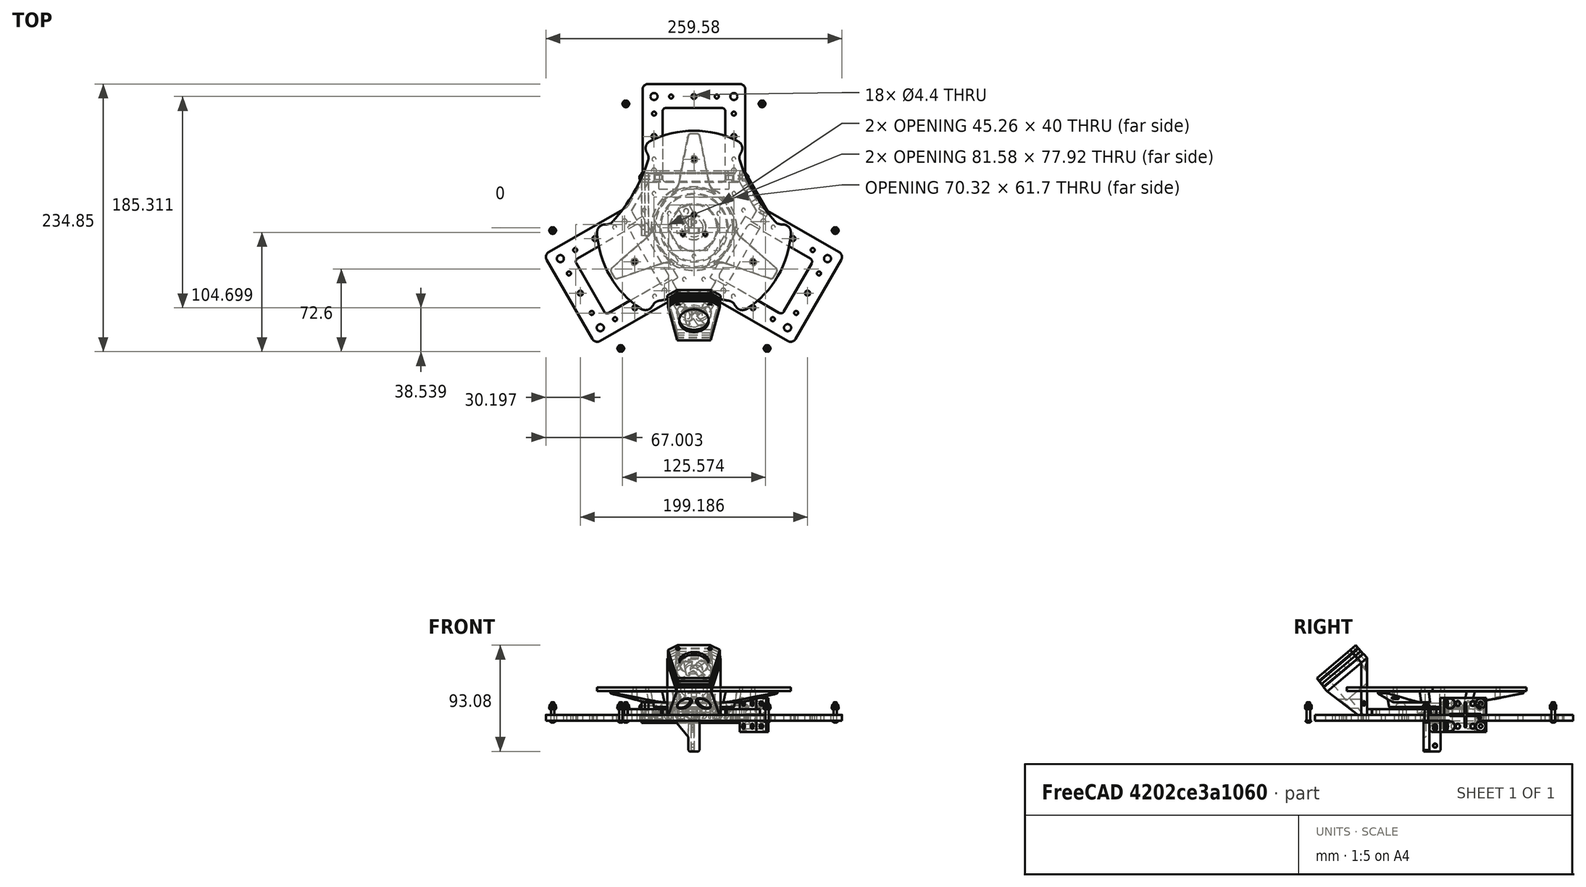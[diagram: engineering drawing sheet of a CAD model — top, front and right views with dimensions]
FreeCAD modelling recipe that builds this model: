
FCSTD DOCUMENT  (FreeCAD 2023.131R26244 +5365 (Git))
Label: structures
License: Creative Commons Attribution-NoDerivatives
LicenseURL: http://creativecommons.org/licenses/by-nd/4.0/
objects: Sketcher::SketchObject×48, PartDesign::Pad×27, PartDesign::Pocket×26, PartDesign::Chamfer×25, PartDesign::Fillet×20, PartDesign::Body×19, Part::FeaturePython×16, App::Link×15, TechDraw::DrawProjGroupItem×12, TechDraw::DrawProjGroup×12, App::Part×11, TechDraw::DrawSVGTemplate×9, TechDraw::DrawPage×9, PartDesign::Mirrored×7, PartDesign::SubShapeBinder×7, PartDesign::PolarPattern×6, App::DocumentObjectGroup×6, TechDraw::DrawViewDimension×5, Part::Mirroring×2, PartDesign::Draft×2, +8 more types
note: 505 computed .brp shape members not serialized (recipe doc carries the construction recipe); baked Part::Feature solids carry a one-line shape summary decoded from their .brp
EXTERNAL_REF file=generic-hardware.FCStd obj=Part035
EXTERNAL_REF file=generic-hardware.FCStd obj=Part036

FEATURE [Sketcher::SketchObject] Sketch032
  ArcFitTolerance = 0
  AttachmentSupport = -> [XY_Plane026]
  ExternalBSplineMaxDegree = 0
  ExternalBSplineTolerance = 0
  FullyConstrained = true
  InternalTolerance = 1e-06
  InvalidShape = false
  MakeInternals = false
  MapMode = 5
  Support = -> [XY_Plane026]
  TreeRank = 0
  ValidateShape = true
  sketch-geometry (56):
    g0: LineSegment StartX=-131.619 StartY=-24.0289 StartZ=0 EndX=-58.007 EndY=18.4711 EndZ=0
    g1: LineSegment StartX=-58.007 StartY=18.4711 StartZ=0 EndX=-45 EndY=41 EndZ=0
    g2: LineSegment StartX=-45 StartY=41 StartZ=0 EndX=-45 EndY=126 EndZ=0
    g3: LineSegment StartX=-45 StartY=126 StartZ=0 EndX=45 EndY=126 EndZ=0
    g4: LineSegment StartX=45 StartY=126 StartZ=0 EndX=45 EndY=41 EndZ=0
    g5: LineSegment StartX=45 StartY=41 StartZ=0 EndX=58.007 EndY=18.4711 EndZ=0
    g6: LineSegment StartX=58.007 StartY=18.4711 StartZ=0 EndX=131.619 EndY=-24.0289 EndZ=0
    g7: LineSegment StartX=131.619 StartY=-24.0289 StartZ=0 EndX=86.6192 EndY=-101.971 EndZ=0
    g8: LineSegment StartX=86.6192 StartY=-101.971 StartZ=0 EndX=13.007 EndY=-59.4711 EndZ=0
    g9: LineSegment StartX=13.007 StartY=-59.4711 StartZ=0 EndX=-13.007 EndY=-59.4711 EndZ=0
    g10: LineSegment StartX=-13.007 StartY=-59.4711 StartZ=0 EndX=-86.6192 EndY=-101.971 EndZ=0
    g11: LineSegment StartX=-86.6192 StartY=-101.971 StartZ=0 EndX=-131.619 EndY=-24.0289 EndZ=0
    g12: LineSegment [constr] StartX=-1e-16 StartY=1e-16 StartZ=0 EndX=-1e-16 EndY=126 EndZ=0
    g13: LineSegment [constr] StartX=-1e-16 StartY=1e-16 StartZ=0 EndX=-109.119 EndY=-63 EndZ=0
    g14: LineSegment [constr] StartX=-1e-16 StartY=1e-16 StartZ=0 EndX=109.119 EndY=-63 EndZ=0
    g15: LineSegment StartX=-27.5 StartY=40 StartZ=0 EndX=27.5 EndY=40 EndZ=0
    g16: LineSegment StartX=27.5 StartY=40 StartZ=0 EndX=27.5 EndY=105 EndZ=0
    g17: LineSegment StartX=27.5 StartY=105 StartZ=0 EndX=-27.5 EndY=105 EndZ=0
    g18: LineSegment StartX=-27.5 StartY=105 StartZ=0 EndX=-27.5 EndY=40 EndZ=0
    g19: LineSegment StartX=20.891 StartY=-43.8157 StartZ=0 EndX=48.391 EndY=3.8157 EndZ=0
    g20: LineSegment StartX=48.391 StartY=3.8157 StartZ=0 EndX=104.683 EndY=-28.6843 EndZ=0
    g21: LineSegment StartX=104.683 StartY=-28.6843 StartZ=0 EndX=77.1827 EndY=-76.3157 EndZ=0
    g22: LineSegment StartX=77.1827 StartY=-76.3157 StartZ=0 EndX=20.891 EndY=-43.8157 EndZ=0
    g23: LineSegment StartX=-104.683 StartY=-28.6843 StartZ=0 EndX=-77.1827 EndY=-76.3157 EndZ=0
    g24: LineSegment StartX=-77.1827 StartY=-76.3157 StartZ=0 EndX=-20.891 EndY=-43.8157 EndZ=0
    g25: LineSegment StartX=-20.891 StartY=-43.8157 StartZ=0 EndX=-48.391 EndY=3.8157 EndZ=0
    g26: LineSegment StartX=-48.391 StartY=3.8157 StartZ=0 EndX=-104.683 EndY=-28.6843 EndZ=0
    g27: Circle [constr] CenterX=-1e-16 CenterY=1e-16 CenterZ=0 NormalX=0 NormalY=0 NormalZ=1 AngleXU=0 Radius=48.5412
    g28: LineSegment StartX=-11.547 StartY=-20 StartZ=0 EndX=-23.094 EndY=0 EndZ=0
    g29: LineSegment StartX=-23.094 StartY=-1.3e-15 StartZ=0 EndX=-11.547 EndY=20 EndZ=0
    g30: LineSegment StartX=-11.547 StartY=20 StartZ=0 EndX=11.547 EndY=20 EndZ=0
    g31: LineSegment StartX=11.547 StartY=20 StartZ=0 EndX=23.094 EndY=0 EndZ=0
    g32: LineSegment StartX=23.094 StartY=9e-16 StartZ=0 EndX=11.547 EndY=-20 EndZ=0
    g33: LineSegment StartX=11.547 StartY=-20 StartZ=0 EndX=-11.547 EndY=-20 EndZ=0
    g34: Circle [constr] CenterX=-1e-16 CenterY=1e-16 CenterZ=0 NormalX=0 NormalY=0 NormalZ=1 AngleXU=0 Radius=23.094
    g35: Circle CenterX=-21.6506 CenterY=12.5 CenterZ=0 NormalX=0 NormalY=0 NormalZ=1 AngleXU=0 Radius=1.6
    g36: Circle CenterX=21.6506 CenterY=12.5 CenterZ=0 NormalX=0 NormalY=0 NormalZ=1 AngleXU=0 Radius=1.6
    g37: Circle CenterX=0 CenterY=-25 CenterZ=0 NormalX=0 NormalY=0 NormalZ=1 AngleXU=0 Radius=1.6
    g38: LineSegment [constr] StartX=0 StartY=-25 StartZ=0 EndX=-1e-16 EndY=0 EndZ=0
    g39: LineSegment [constr] StartX=-1e-16 StartY=1e-16 StartZ=0 EndX=21.6506 EndY=12.5 EndZ=0
    g40: LineSegment [constr] StartX=-1e-16 StartY=1e-16 StartZ=0 EndX=-21.6506 EndY=12.5 EndZ=0
    g41: LineSegment [constr] StartX=-45 StartY=126 StartZ=0 EndX=-131.619 EndY=-24.0289 EndZ=0
    g42: LineSegment [constr] StartX=-86.6192 StartY=-101.971 StartZ=0 EndX=86.6192 EndY=-101.971 EndZ=0
    g43: LineSegment [constr] StartX=131.619 StartY=-24.0289 StartZ=0 EndX=45 EndY=126 EndZ=0
    g44: LineSegment [constr] StartX=-45 StartY=126 StartZ=0 EndX=-55 EndY=108.679 EndZ=0
    g45: LineSegment [constr] StartX=-55 StartY=108.679 StartZ=0 EndX=-45 EndY=41 EndZ=0
    g46: LineSegment [constr] StartX=-58.007 StartY=18.4711 StartZ=0 EndX=-121.619 EndY=-6.70835 EndZ=0
    g47: LineSegment [constr] StartX=-121.619 StartY=-6.70835 StartZ=0 EndX=-131.619 EndY=-24.0289 EndZ=0
    g48: LineSegment [constr] StartX=-86.6192 StartY=-101.971 StartZ=0 EndX=-66.6192 EndY=-101.971 EndZ=0
    g49: LineSegment [constr] StartX=-66.6192 StartY=-101.971 StartZ=0 EndX=-13.007 EndY=-59.4711 EndZ=0
    g50: LineSegment [constr] StartX=13.007 StartY=-59.4711 StartZ=0 EndX=66.6192 EndY=-101.971 EndZ=0
    g51: LineSegment [constr] StartX=66.6192 StartY=-101.971 StartZ=0 EndX=86.6192 EndY=-101.971 EndZ=0
    g52: LineSegment [constr] StartX=131.619 StartY=-24.0289 StartZ=0 EndX=121.619 EndY=-6.70835 EndZ=0
    g53: LineSegment [constr] StartX=121.619 StartY=-6.70835 StartZ=0 EndX=58.007 EndY=18.4711 EndZ=0
    g54: LineSegment [constr] StartX=45 StartY=41 StartZ=0 EndX=55 EndY=108.679 EndZ=0
    g55: LineSegment [constr] StartX=55 StartY=108.679 StartZ=0 EndX=45 EndY=126 EndZ=0
  constraints (151):
    c: Coincident(g0,g1)
    c: Coincident(g1,g2)
    c: Vertical(g2)
    c: Coincident(g2,g3)
    c: Horizontal(g3)
    c: Coincident(g3,g4)
    c: Vertical(g4)
    c: Coincident(g4,g5)
    c: Coincident(g5,g6)
    c: Coincident(g6,g7)
    c: Coincident(g7,g8)
    c: Coincident(g8,g9)
    c: Horizontal(g9)
    c: Coincident(g9,g10)
    c: Coincident(g10,g11)
    c: Coincident(g11,g0)
    c: Parallel(g8,g6)
    c: Parallel(g10,g0)
    c: Equal(g4,g6)
    c: Equal(g6,g8)
    c: Equal(g8,g10)
    c: Equal(g10,g0)
    c: Equal(g0,g2)
    c: Perpendicular(g6,g7)
    c: Perpendicular(g11,g10)
    c: Coincident(g12,g-1)
    c: PointOnObject(g12,g3)
    c: Vertical(g12)
    c: Coincident(g13,g12)
    c: Coincident(g14,g12)
    c: Symmetric(g6,g7,g14)
    c: Symmetric(g10,g0,g13)
    c: Perpendicular(g13,g11)
    c: Perpendicular(g7,g14)
    c: DistanceX(g3,g3) = 90
    c: Equal(g9,g5)
    c: Equal(g5,g1)
    c: Angle(g14,g12) = 2.0944
    c: Angle(g12,g13) = 2.0944
    c: DistanceY(g12,g2) = 126
    c: DistanceX(g9,g9) = 26.0141
    c: Coincident(g15,g16)
    c: Coincident(g16,g17)
    c: Coincident(g17,g18)
    c: Coincident(g18,g15)
    c: Horizontal(g15)
    c: Vertical(g16)
    c: Vertical(g18)
    c: Symmetric(g16,g17,g12)
    c: DistanceX(g17,g17) = 55
    c: DistanceY(g16,g16) = 65
    c: Coincident(g19,g20)
    c: Coincident(g20,g21)
    c: Coincident(g21,g22)
    c: Coincident(g22,g19)
    c: Coincident(g23,g24)
    c: Coincident(g24,g25)
    c: Coincident(g25,g26)
    c: Coincident(g26,g23)
    c: Equal(g25,g23)
    c: Equal(g23,g19)
    c: Equal(g19,g21)
    c: Equal(g21,g15)
    c: Equal(g22,g20)
    c: Equal(g20,g16)
    c: Equal(g16,g26)
    c: Equal(g26,g24)
    c: Parallel(g24,g13)
    c: Parallel(g22,g14)
    c: Symmetric(g23,g23,g13)
    c: Symmetric(g21,g20,g14)
    c: Coincident(g27,g12)
    c: PointOnObject(g19,g27)
    c: PointOnObject(g24,g27)
    c: PointOnObject(g15,g27)
    c: Equal(g11,g7)
    c: Equal(g7,g3)
    c: Coincident(g28,g29)
    c: Coincident(g29,g30)
    c: Coincident(g30,g31)
    c: Coincident(g31,g32)
    c: Coincident(g32,g33)
    c: Coincident(g33,g28)
    c: Horizontal(g33)
    c: Horizontal(g30)
    c: Equal(g29,g30)
    c: Equal(g30,g31)
    c: Equal(g31,g32)
    c: Equal(g32,g33)
    c: Equal(g33,g28)
    c: Coincident(g34,g12)
    c: PointOnObject(g30,g34)
    c: PointOnObject(g31,g34)
    c: PointOnObject(g32,g34)
    c: PointOnObject(g28,g34)
    c: PointOnObject(g28,g34)
    c: DistanceY(g12,g30) = 20
    c: PointOnObject(g37,g-2)
    c: Equal(g37,g36)
    c: Equal(g36,g35)
    c: Diameter(g35) = 3.2
    c: Coincident(g38,g37)
    c: Coincident(g38,g12)
    c: Coincident(g39,g12)
    c: Coincident(g39,g36)
    c: Coincident(g40,g12)
    c: Coincident(g40,g35)
    c: Perpendicular(g29,g40)
    c: Perpendicular(g31,g39)
    c: Equal(g40,g38)
    c: Equal(g38,g39)
    c: DistanceY(g38,g38) = 25
    c: Coincident(g41,g3)
    c: Coincident(g41,g11)
    c: Coincident(g42,g11)
    c: Coincident(g42,g7)
    c: Coincident(g43,g7)
    c: Coincident(g43,g3)
    c: Coincident(g3,g44)
    c: PointOnObject(g44,g41)
    c: Coincident(g44,g45)
    c: Coincident(g45,g1)
    c: Coincident(g1,g46)
    c: PointOnObject(g46,g41)
    c: Coincident(g46,g47)
    c: Coincident(g47,g11)
    c: Coincident(g11,g48)
    c: Horizontal(g48)
    c: Coincident(g48,g49)
    c: Coincident(g49,g9)
    c: Coincident(g9,g50)
    c: PointOnObject(g50,g42)
    c: Coincident(g50,g51)
    c: Coincident(g51,g7)
    c: Coincident(g7,g52)
    c: PointOnObject(g52,g43)
    c: Coincident(g52,g53)
    c: Coincident(g53,g5)
    c: Coincident(g5,g54)
    c: PointOnObject(g54,g43)
    c: Coincident(g54,g55)
    c: Coincident(g55,g3)
    c: Equal(g55,g44)
    c: Equal(g44,g47)
    c: Equal(g47,g48)
    c: Equal(g48,g51)
    c: Equal(g55,g52)
    c: DistanceX(g48,g48) = 20
    c: DistanceY(g16) = 105
    c: DistanceY(g50,g12) = 101.971
    c: DistanceY(g4,g4) = 85
FEATURE [PartDesign::Pad] Pad020
  AddSubType = 0
  AutoTaperInnerAngle = false
  CheckUpToFaceLimits = true
  ClaimChildren = false
  Direction = (0,0,1)
  Fit = 0
  FitJoin = 0
  InnerFit = 0
  InnerFitJoin = 0
  InvalidShape = false
  Length = 5
  Length2 = 100
  Linearize = true
  NewSolid = false
  Profile = -> Sketch032
  Refine = true
  Reversed = true
  Suppress = false
  TaperInnerAngle = 0
  TaperInnerAngleRev = 0
  TreeRank = 0
  Type = 0
  ValidateShape = true
  _ProfileBasedVersion = 1
FEATURE [PartDesign::Fillet] Fillet008
  AddSubType = 0
  Base = -> Pad020 [Edge41,Edge44,Edge37,Edge38,Edge65,Edge62,Edge61,Edge68,Edge49,Edge50,Edge53,Edge56]
  BaseFeature = -> Pad020
  InvalidShape = false
  NewSolid = false
  Radius = 3
  Refine = true
  SupportTransform = false
  Suppress = false
  TreeRank = 0
  ValidateShape = true
FEATURE [PartDesign::Fillet] Fillet009
  AddSubType = 0
  Base = -> Fillet008 [Edge110,Edge99,Edge107,Edge106,Edge102,Edge103]
  BaseFeature = -> Fillet008
  InvalidShape = false
  NewSolid = false
  Radius = 5
  Refine = true
  SupportTransform = false
  Suppress = false
  TreeRank = 0
  ValidateShape = true
FEATURE [PartDesign::Fillet] Fillet010
  AddSubType = 0
  Base = -> Fillet009 [Edge53,Edge57,Edge67,Edge71,Edge77,Edge81]
  BaseFeature = -> Fillet009
  InvalidShape = false
  NewSolid = false
  Radius = 5
  Refine = true
  SupportTransform = false
  Suppress = false
  TreeRank = 0
  ValidateShape = true
FEATURE [Sketcher::SketchObject] Sketch033
  ArcFitTolerance = 0
  AttachmentSupport = -> [XY_Plane026]
  ExternalBSplineMaxDegree = 0
  ExternalBSplineTolerance = 0
  FullyConstrained = true
  InternalTolerance = 1e-06
  InvalidShape = false
  MakeInternals = false
  MapMode = 5
  Support = -> [XY_Plane026]
  TreeRank = 0
  ValidateShape = true
  sketch-geometry (13):
    g0: Circle CenterX=-20 CenterY=115 CenterZ=0 NormalX=0 NormalY=0 NormalZ=1 AngleXU=0 Radius=1.75
    g1: Circle CenterX=20 CenterY=115 CenterZ=0 NormalX=0 NormalY=0 NormalZ=1 AngleXU=0 Radius=1.75
    g2: Circle CenterX=-35 CenterY=60 CenterZ=0 NormalX=0 NormalY=0 NormalZ=1 AngleXU=0 Radius=1.75
    g3: Circle CenterX=-35 CenterY=100 CenterZ=0 NormalX=0 NormalY=0 NormalZ=1 AngleXU=0 Radius=1.75
    g4: Circle CenterX=35 CenterY=100 CenterZ=0 NormalX=0 NormalY=0 NormalZ=1 AngleXU=0 Radius=1.75
    g5: Circle CenterX=35 CenterY=60 CenterZ=0 NormalX=0 NormalY=0 NormalZ=1 AngleXU=0 Radius=1.75
    g6: Circle CenterX=-35 CenterY=115 CenterZ=0 NormalX=0 NormalY=0 NormalZ=1 AngleXU=0 Radius=3.1
    g7: Circle CenterX=35 CenterY=115 CenterZ=0 NormalX=0 NormalY=0 NormalZ=1 AngleXU=0 Radius=3.1
    g8: Circle CenterX=-35 CenterY=80 CenterZ=0 NormalX=0 NormalY=0 NormalZ=1 AngleXU=0 Radius=2.2
    g9: Circle CenterX=35 CenterY=80 CenterZ=0 NormalX=0 NormalY=0 NormalZ=1 AngleXU=0 Radius=2.2
    g10: Circle CenterX=-35 CenterY=50 CenterZ=0 NormalX=0 NormalY=0 NormalZ=1 AngleXU=0 Radius=2.2
    g11: Circle CenterX=35 CenterY=50 CenterZ=0 NormalX=0 NormalY=0 NormalZ=1 AngleXU=0 Radius=2.2
    g12: Circle CenterX=-1.0206e-12 CenterY=115 CenterZ=0 NormalX=0 NormalY=0 NormalZ=1 AngleXU=0 Radius=2.2
  constraints (31):
    c: Equal(g0,g3)
    c: Equal(g3,g2)
    c: Equal(g2,g1)
    c: Equal(g1,g4)
    c: Equal(g4,g5)
    c: Diameter(g0) = 3.5
    c: Symmetric(g1,g0,g-2)
    c: Symmetric(g3,g4,g-2)
    c: Symmetric(g2,g5,g-2)
    c: Vertical(g3,g2)
    c: DistanceX(g3,g4) = 70
    c: DistanceX(g0,g1) = 40
    c: DistanceY(g4,g1) = 15
    c: DistanceY(g5,g4) = 40
    c: DistanceY(g-1,g1) = 115
    c: Symmetric(g7,g6,g-2)
    c: Horizontal(g6,g0)
    c: Diameter(g7) = 6.2
    c: Equal(g7,g6)
    c: Vertical(g7,g4)
    c: Equal(g9,g8)
    c: Symmetric(g8,g9,g-2)
    c: Symmetric(g5,g4,g9)
    c: Diameter(g9) = 4.4
    c: Symmetric(g1,g0,g12)
    c: Equal(g12,g11)
    c: Equal(g11,g10)
    c: Equal(g10,g9)
    c: Vertical(g11,g5)
    c: Symmetric(g11,g10,g-2)
    c: DistanceY(g11,g5) = 10
FEATURE [PartDesign::Pocket] Pocket012
  AddSubType = 1
  AutoTaperInnerAngle = false
  BaseFeature = -> Fillet010
  CheckUpToFaceLimits = true
  ClaimChildren = false
  Fit = 0
  FitJoin = 0
  InnerFit = 0
  InnerFitJoin = 0
  InvalidShape = false
  Length = 5
  Length2 = 100
  Linearize = true
  NewSolid = false
  Profile = -> Sketch033
  Refine = true
  Suppress = false
  TaperInnerAngle = 0
  TaperInnerAngleRev = 0
  TreeRank = 0
  Type = 1
  ValidateShape = true
  _ProfileBasedVersion = 1
  _Version = 0
FEATURE [PartDesign::PolarPattern] PolarPattern013
  AddSubType = 0
  Angle = 360
  Axis = -> Sketch033 [N_Axis]
  BaseFeature = -> Pocket012
  CopyShape = false
  InvalidShape = false
  NewSolid = false
  Occurrences = 3
  OriginalSubs = -> [Pocket012]
  Originals = -> [Pocket012]
  ParallelTransform = true
  Refine = true
  SubTransform = true
  Suppress = false
  TreeRank = 0
  ValidateShape = true
  _Version = 0
FEATURE [PartDesign::Fillet] Fillet011
  AddSubType = 0
  Base = -> PolarPattern013 [Edge190,Edge189,Edge192,Edge196,Edge198,Edge194]
  BaseFeature = -> PolarPattern013
  InvalidShape = false
  NewSolid = false
  Radius = 3
  Refine = true
  SupportTransform = false
  Suppress = false
  TreeRank = 0
  ValidateShape = true
FEATURE [PartDesign::Body] Body019  label="Semelle"
  AutoGroupSolids = false
  ClaimAllChildren = false
  ExportMode = 0
  Group = -> [Sketch032,Pad020,Fillet008,Fillet009,Fillet010,Sketch033,Pocket012,PolarPattern013,Fillet011]
  InvalidShape = false
  Origin = -> Origin029
  SingleSolid = true
  Tip = -> Fillet011
  TreeRank = 0
  ValidateShape = true
  _ExportChildren = -> [Pad020,Fillet008,Fillet009,Fillet010,Pocket012,PolarPattern013,Fillet011]
  _GroupVersion = 1
FEATURE [Sketcher::SketchObject] Sketch034
  ArcFitTolerance = 0
  AttachmentSupport = -> [XY_Plane027]
  ExternalBSplineMaxDegree = 0
  ExternalBSplineTolerance = 0
  FullyConstrained = true
  InternalTolerance = 1e-06
  InvalidShape = false
  MakeInternals = false
  MapMode = 5
  Support = -> [XY_Plane027]
  TreeRank = 0
  ValidateShape = true
  sketch-geometry (33):
    g0: LineSegment StartX=-54.641 StartY=14.641 StartZ=0 EndX=-40 EndY=40 EndZ=0
    g1: LineSegment StartX=-40 StartY=40 StartZ=0 EndX=-31 EndY=40 EndZ=0
    g2: LineSegment StartX=-31 StartY=40 StartZ=0 EndX=-31 EndY=34 EndZ=0
    g3: LineSegment StartX=-31 StartY=34 StartZ=0 EndX=31 EndY=34 EndZ=0
    g4: LineSegment StartX=31 StartY=34 StartZ=0 EndX=31 EndY=40 EndZ=0
    g5: LineSegment StartX=31 StartY=40 StartZ=0 EndX=40 EndY=40 EndZ=0
    g6: LineSegment StartX=40 StartY=40 StartZ=0 EndX=54.641 EndY=14.641 EndZ=0
    g7: LineSegment StartX=54.641 StartY=14.641 StartZ=0 EndX=50.141 EndY=6.84679 EndZ=0
    g8: LineSegment StartX=50.141 StartY=6.84679 StartZ=0 EndX=44.9449 EndY=9.84679 EndZ=0
    g9: LineSegment StartX=44.9449 StartY=9.84679 StartZ=0 EndX=13.9449 EndY=-43.8468 EndZ=0
    g10: LineSegment StartX=13.9449 StartY=-43.8468 StartZ=0 EndX=19.141 EndY=-46.8468 EndZ=0
    g11: LineSegment StartX=19.141 StartY=-46.8468 StartZ=0 EndX=14.641 EndY=-54.641 EndZ=0
    g12: LineSegment StartX=14.641 StartY=-54.641 StartZ=0 EndX=-14.641 EndY=-54.641 EndZ=0
    g13: LineSegment StartX=-14.641 StartY=-54.641 StartZ=0 EndX=-19.141 EndY=-46.8468 EndZ=0
    g14: LineSegment StartX=-19.141 StartY=-46.8468 StartZ=0 EndX=-13.9449 EndY=-43.8468 EndZ=0
    g15: LineSegment StartX=-13.9449 StartY=-43.8468 StartZ=0 EndX=-44.9449 EndY=9.84679 EndZ=0
    g16: LineSegment StartX=-44.9449 StartY=9.84679 StartZ=0 EndX=-50.141 EndY=6.84679 EndZ=0
    g17: LineSegment StartX=-50.141 StartY=6.84679 StartZ=0 EndX=-54.641 EndY=14.641 EndZ=0
    g18: Circle [constr] CenterX=0 CenterY=0 CenterZ=0 NormalX=0 NormalY=0 NormalZ=1 AngleXU=0 Radius=56.5685
    g19: Circle [constr] CenterX=0 CenterY=0 CenterZ=0 NormalX=0 NormalY=0 NormalZ=1 AngleXU=0 Radius=25
    g20: Circle CenterX=-21.6506 CenterY=12.5 CenterZ=0 NormalX=0 NormalY=0 NormalZ=1 AngleXU=0 Radius=1.6
    g21: Circle CenterX=21.6506 CenterY=12.5 CenterZ=0 NormalX=0 NormalY=0 NormalZ=1 AngleXU=0 Radius=1.6
    g22: Circle CenterX=0 CenterY=-25 CenterZ=0 NormalX=0 NormalY=0 NormalZ=1 AngleXU=0 Radius=1.6
    g23: LineSegment [constr] StartX=0 StartY=0 StartZ=0 EndX=21.6506 EndY=12.5 EndZ=0
    g24: LineSegment [constr] StartX=0 StartY=0 StartZ=0 EndX=0 EndY=-25 EndZ=0
    g25: LineSegment [constr] StartX=0 StartY=0 StartZ=0 EndX=-21.6506 EndY=12.5 EndZ=0
    g26: LineSegment StartX=11.547 StartY=20 StartZ=0 EndX=-11.547 EndY=20 EndZ=0
    g27: LineSegment StartX=-11.547 StartY=20 StartZ=0 EndX=-23.094 EndY=1.0409e-12 EndZ=0
    g28: LineSegment StartX=-23.094 StartY=1.0409e-12 StartZ=0 EndX=-11.547 EndY=-20 EndZ=0
    g29: LineSegment StartX=-11.547 StartY=-20 StartZ=0 EndX=11.547 EndY=-20 EndZ=0
    g30: LineSegment StartX=11.547 StartY=-20 StartZ=0 EndX=23.094 EndY=1.0374e-12 EndZ=0
    g31: LineSegment StartX=23.094 StartY=1.0374e-12 StartZ=0 EndX=11.547 EndY=20 EndZ=0
    g32: Circle [constr] CenterX=0 CenterY=0 CenterZ=0 NormalX=0 NormalY=0 NormalZ=1 AngleXU=0 Radius=23.094
  constraints (88):
    c: Coincident(g0,g1)
    c: Horizontal(g1)
    c: Coincident(g1,g2)
    c: Vertical(g2)
    c: Coincident(g2,g3)
    c: Coincident(g3,g4)
    c: Vertical(g4)
    c: Coincident(g4,g5)
    c: Horizontal(g5)
    c: Coincident(g5,g6)
    c: Coincident(g6,g7)
    c: Coincident(g7,g8)
    c: Coincident(g8,g9)
    c: Coincident(g9,g10)
    c: Coincident(g10,g11)
    c: Coincident(g11,g12)
    c: Horizontal(g12)
    c: Coincident(g12,g13)
    c: Coincident(g13,g14)
    c: Coincident(g14,g15)
    c: Coincident(g15,g16)
    c: Coincident(g16,g17)
    c: Coincident(g17,g0)
    c: DistanceY(g-1,g1) = 40
    c: DistanceX(g1,g1) = 9
    c: Equal(g5,g1)
    c: Equal(g1,g17)
    c: Equal(g17,g13)
    c: Equal(g13,g11)
    c: Equal(g11,g7)
    c: Perpendicular(g10,g11)
    c: Perpendicular(g14,g13)
    c: Perpendicular(g15,g14)
    c: Perpendicular(g9,g10)
    c: Perpendicular(g9,g8)
    c: Perpendicular(g8,g7)
    c: Perpendicular(g17,g16)
    c: Perpendicular(g15,g16)
    c: DistanceY(g2,g2) = 6
    c: Equal(g8,g4)
    c: Equal(g4,g16)
    c: Equal(g0,g6)
    c: Equal(g6,g12)
    c: Coincident(g18,g-1)
    c: PointOnObject(g5,g18)
    c: PointOnObject(g6,g18)
    c: PointOnObject(g11,g18)
    c: PointOnObject(g12,g18)
    c: PointOnObject(g0,g18)
    c: PointOnObject(g0,g18)
    c: Symmetric(g3,g2,g-2)
    c: DistanceX(g3,g3) = 62
    c: Angle(g15,g3) = 1.0472
    c: Angle(g3,g9) = 1.0472
    c: Equal(g10,g8)
    c: Coincident(g19,g18)
    c: PointOnObject(g20,g19)
    c: PointOnObject(g21,g19)
    c: PointOnObject(g22,g19)
    c: PointOnObject(g22,g-2)
    c: Coincident(g23,g18)
    c: Coincident(g23,g21)
    c: Coincident(g24,g18)
    c: Coincident(g24,g22)
    c: Coincident(g25,g18)
    c: Coincident(g25,g20)
    c: Angle(g23,g25) = 2.0944
    c: Angle(g24,g23) = 2.0944
    c: DistanceY(g24,g24) = 25
    c: Equal(g21,g22)
    c: Equal(g22,g20)
    c: Diameter(g21) = 3.2
    c: Coincident(g26,g27)
    c: Coincident(g27,g28)
    c: Coincident(g28,g29)
    c: Coincident(g29,g30)
    c: Coincident(g30,g31)
    c: Coincident(g31,g26)
    c: Equal(g26, g27-g31) x5
    c: PointOnObject(g26,g32)
    c: PointOnObject(g27,g32)
    c: PointOnObject(g28,g32)
    c: PointOnObject(g29,g32)
    c: PointOnObject(g30,g32)
    c: PointOnObject(g31,g32)
    c: Coincident(g32,g18)
    c: Horizontal(g26)
    c: DistanceY(g26) = 20
FEATURE [PartDesign::Pad] Pad021
  AddSubType = 0
  AutoTaperInnerAngle = false
  CheckUpToFaceLimits = true
  ClaimChildren = false
  Direction = (1,1,1)
  Fit = 0
  FitJoin = 0
  InnerFit = 0
  InnerFitJoin = 0
  InvalidShape = false
  Length = 5
  Length2 = 100
  Linearize = true
  NewSolid = false
  Profile = -> Sketch034
  Refine = true
  Suppress = false
  TaperInnerAngle = 0
  TaperInnerAngleRev = 0
  TreeRank = 0
  Type = 0
  ValidateShape = true
  _ProfileBasedVersion = 1
FEATURE [PartDesign::Fillet] Fillet012
  AddSubType = 0
  Base = -> Pad021 [Edge59,Edge56,Edge68,Edge55,Edge65,Edge62]
  BaseFeature = -> Pad021
  InvalidShape = false
  NewSolid = false
  Radius = 3
  Refine = true
  SupportTransform = false
  Suppress = false
  TreeRank = 0
  ValidateShape = true
FEATURE [PartDesign::Fillet] Fillet013
  AddSubType = 0
  Base = -> Fillet012 [Edge94,Edge93,Edge95,Edge96,Edge81,Edge82,Edge84,Edge83,Edge88,Edge87,Edge86,Edge85,Edge80,Edge79,Edge92,Edge91,Edge90,Edge89]
  BaseFeature = -> Fillet012
  InvalidShape = false
  NewSolid = false
  Radius = 0.5
  Refine = true
  SupportTransform = false
  Suppress = false
  TreeRank = 0
  ValidateShape = true
FEATURE [PartDesign::Body] Body020  label="CaleCentrale"
  AutoGroupSolids = false
  ClaimAllChildren = false
  ExportMode = 0
  Group = -> [Sketch034,Pad021,Fillet012,Fillet013]
  InvalidShape = false
  Origin = -> Origin030
  SingleSolid = true
  Tip = -> Fillet013
  TreeRank = 0
  ValidateShape = true
  _ExportChildren = -> [Pad021,Fillet012,Fillet013]
  _GroupVersion = 1
FEATURE [Sketcher::SketchObject] Sketch043
  ArcFitTolerance = 0
  AttachmentSupport = -> [XY_Plane031]
  ExternalBSplineMaxDegree = 0
  ExternalBSplineTolerance = 0
  FullyConstrained = true
  InternalTolerance = 1e-06
  InvalidShape = false
  MakeInternals = false
  MapMode = 5
  Support = -> [XY_Plane031]
  TreeRank = 0
  ValidateShape = true
  sketch-geometry (13):
    g0: LineSegment StartX=0 StartY=0 StartZ=0 EndX=0 EndY=-54.641 EndZ=0
    g1: LineSegment StartX=0 StartY=-54.641 StartZ=0 EndX=-14.641 EndY=-54.641 EndZ=0
    g2: LineSegment StartX=-14.641 StartY=-54.641 StartZ=0 EndX=-19.641 EndY=-45.9808 EndZ=0
    g3: LineSegment StartX=-19.641 StartY=-45.9808 StartZ=0 EndX=-28.3013 EndY=-50.9808 EndZ=0
    g4: LineSegment StartX=-28.3013 StartY=-50.9808 StartZ=0 EndX=-58.3013 EndY=0.980762 EndZ=0
    g5: LineSegment StartX=-58.3013 StartY=0.980762 StartZ=0 EndX=-49.641 EndY=5.98076 EndZ=0
    g6: LineSegment StartX=-49.641 StartY=5.98076 StartZ=0 EndX=-54.641 EndY=14.641 EndZ=0
    g7: LineSegment StartX=-54.641 StartY=14.641 StartZ=0 EndX=-47.3205 EndY=27.3205 EndZ=0
    g8: LineSegment StartX=-47.3205 StartY=27.3205 StartZ=0 EndX=0 EndY=0 EndZ=0
    g9: LineSegment [constr] StartX=-49.641 StartY=5.98076 StartZ=0 EndX=-19.641 EndY=-45.9808 EndZ=0
    g10: Circle CenterX=-43.4808 CenterY=15.3109 CenterZ=0 NormalX=0 NormalY=0 NormalZ=1 AngleXU=0 Radius=1.6
    g11: Circle CenterX=-8.48076 CenterY=-45.3109 CenterZ=0 NormalX=0 NormalY=0 NormalZ=1 AngleXU=0 Radius=1.6
    g12: LineSegment [constr] StartX=0 StartY=0 StartZ=0 EndX=-43.3013 EndY=-25 EndZ=0
  constraints (35):
    c: Coincident(g0,g-1)
    c: PointOnObject(g0,g-2)
    c: Coincident(g1,g0)
    c: Horizontal(g1)
    c: Coincident(g1,g2)
    c: Coincident(g2,g3)
    c: Coincident(g3,g4)
    c: Coincident(g4,g5)
    c: Coincident(g5,g6)
    c: Coincident(g6,g7)
    c: Coincident(g7,g8)
    c: Coincident(g8,g0)
    c: Angle(g8,g0) = 2.0944
    c: Perpendicular(g7,g8)
    c: Perpendicular(g3,g2)
    c: Perpendicular(g4,g3)
    c: Perpendicular(g4,g5)
    c: Perpendicular(g6,g5)
    c: Equal(g7,g1)
    c: Coincident(g9,g5)
    c: Tangent(g9,g2) = 1.5708
    c: Equal(g2,g3)
    c: Equal(g5,g6)
    c: Distance(g6) = 10
    c: Equal(g0,g8)
    c: Distance(g4) = 60
    c: Distance(g0,g9) = 40
    c: Coincident(g12,g0)
    c: PointOnObject(g12,g4)
    c: Perpendicular(g4,g12)
    c: Symmetric(g11,g10,g12)
    c: Diameter(g10) = 3.2
    c: Equal(g10,g11)
    c: Distance(g11,g2) = 10
    c: Distance(g11,g12) = 35
FEATURE [PartDesign::Pad] Pad027
  AddSubType = 0
  AutoTaperInnerAngle = false
  CheckUpToFaceLimits = true
  ClaimChildren = false
  Direction = (1,1,1)
  Fit = 0
  FitJoin = 0
  InnerFit = 0
  InnerFitJoin = 0
  InvalidShape = false
  Length = 5
  Length2 = 100
  Linearize = true
  NewSolid = false
  Profile = -> Sketch043
  Refine = true
  Suppress = false
  TaperInnerAngle = 0
  TaperInnerAngleRev = 0
  TreeRank = 0
  Type = 0
  ValidateShape = true
  _ProfileBasedVersion = 1
FEATURE [PartDesign::PolarPattern] PolarPattern014
  AddSubType = 0
  Angle = 360
  Axis = -> Sketch043 [N_Axis]
  BaseFeature = -> Pad027
  CopyShape = false
  InvalidShape = false
  NewSolid = false
  Occurrences = 3
  OriginalSubs = -> [Pad027]
  Originals = -> [Pad027]
  ParallelTransform = true
  Refine = true
  SubTransform = true
  Suppress = false
  TreeRank = 0
  ValidateShape = true
  _Version = 2
FEATURE [Sketcher::SketchObject] Sketch044
  ArcFitTolerance = 0
  AttachmentSupport = -> [XY_Plane031]
  ExternalBSplineMaxDegree = 0
  ExternalBSplineTolerance = 0
  FullyConstrained = true
  InternalTolerance = 1e-06
  InvalidShape = false
  MakeInternals = false
  MapMode = 5
  Support = -> [XY_Plane031]
  TreeRank = 0
  ValidateShape = true
  sketch-geometry (5):
    g0: LineSegment StartX=-35.6218 StartY=8.30127 StartZ=0 EndX=-10.6218 EndY=-35 EndZ=0
    g1: LineSegment StartX=-10.6218 StartY=-35 StartZ=0 EndX=0 EndY=-35 EndZ=0
    g2: LineSegment StartX=0 StartY=-35 StartZ=0 EndX=0 EndY=0 EndZ=0
    g3: LineSegment StartX=0 StartY=0 StartZ=0 EndX=-30.3109 EndY=17.5 EndZ=0
    g4: LineSegment StartX=-30.3109 StartY=17.5 StartZ=0 EndX=-35.6218 EndY=8.30127 EndZ=0
  constraints (14):
    c: Coincident(g0,g1)
    c: PointOnObject(g1,g-2)
    c: Horizontal(g1)
    c: Coincident(g1,g2)
    c: Coincident(g2,g-1)
    c: Coincident(g2,g3)
    c: Coincident(g3,g4)
    c: Coincident(g4,g0)
    c: Perpendicular(g4,g3)
    c: Equal(g4,g1)
    c: Equal(g2,g3)
    c: Angle(g3,g2) = 2.0944
    c: Distance(g0) = 50
    c: DistanceY(g2,g2) = 35
FEATURE [PartDesign::Pocket] Pocket017
  AddSubType = 1
  AutoTaperInnerAngle = false
  BaseFeature = -> PolarPattern014
  CheckUpToFaceLimits = true
  ClaimChildren = false
  Fit = 0
  FitJoin = 0
  InnerFit = 0
  InnerFitJoin = 0
  InvalidShape = false
  Length = 5
  Length2 = 100
  Linearize = true
  NewSolid = false
  Profile = -> Sketch044
  Refine = true
  Reversed = true
  Suppress = false
  TaperInnerAngle = 0
  TaperInnerAngleRev = 0
  TreeRank = 0
  Type = 1
  ValidateShape = true
  _ProfileBasedVersion = 1
  _Version = 0
FEATURE [PartDesign::PolarPattern] PolarPattern015
  AddSubType = 0
  Angle = 360
  Axis = -> Sketch044 [N_Axis]
  BaseFeature = -> Pocket017
  CopyShape = false
  InvalidShape = false
  NewSolid = false
  Occurrences = 3
  OriginalSubs = -> [Pocket017]
  Originals = -> [Pocket017]
  ParallelTransform = true
  Refine = true
  SubTransform = true
  Suppress = false
  TreeRank = 0
  ValidateShape = true
  _Version = 2
FEATURE [PartDesign::Chamfer] Chamfer007
  AddSubType = 0
  Angle = 45
  Base = -> PolarPattern015 [Edge8,Edge66,Edge67,Edge68,Edge77,Edge78]
  BaseFeature = -> PolarPattern015
  ChamferType = 0
  FlipDirection = false
  InvalidShape = false
  NewSolid = false
  Refine = true
  Size = 1
  Size2 = 1
  SupportTransform = false
  Suppress = false
  TreeRank = 0
  ValidateShape = true
FEATURE [PartDesign::Fillet] Fillet014
  AddSubType = 0
  Base = -> Chamfer007 [Edge101,Edge103,Edge104,Edge105,Edge106,Edge102]
  BaseFeature = -> Chamfer007
  InvalidShape = false
  NewSolid = false
  Radius = 3
  Refine = true
  SupportTransform = false
  Suppress = false
  TreeRank = 0
  ValidateShape = true
FEATURE [PartDesign::Body] Body024  label="PlaqueIntermediaire"
  AutoGroupSolids = false
  ClaimAllChildren = false
  ExportMode = 0
  Group = -> [Sketch043,Pad027,PolarPattern014,Sketch044,Pocket017,PolarPattern015,Chamfer007,Fillet014]
  InvalidShape = false
  Origin = -> Origin036
  SingleSolid = true
  Tip = -> Fillet014
  TreeRank = 0
  ValidateShape = true
  _ExportChildren = -> [Pad027,PolarPattern014,Pocket017,PolarPattern015,Chamfer007,Fillet014]
  _GroupVersion = 1
FEATURE [Sketcher::SketchObject] Sketch037
  ArcFitTolerance = 0
  AttachmentSupport = -> [XZ_Plane030]
  ExternalBSplineMaxDegree = 0
  ExternalBSplineTolerance = 0
  FullyConstrained = true
  InternalTolerance = 1e-06
  InvalidShape = false
  MakeInternals = false
  MapMode = 5
  Placement = pos=(0,0,0) rot=(1,0,0;1.5708rad)
  Support = -> [XZ_Plane030]
  TreeRank = 0
  ValidateShape = true
  sketch-geometry (6):
    g0: LineSegment StartX=-5 StartY=0 StartZ=0 EndX=15 EndY=0 EndZ=0
    g1: LineSegment StartX=15 StartY=0 StartZ=0 EndX=15 EndY=-7 EndZ=0
    g2: LineSegment StartX=15 StartY=-7 StartZ=0 EndX=5 EndY=-7 EndZ=0
    g3: LineSegment StartX=5 StartY=-7 StartZ=0 EndX=5 EndY=-32 EndZ=0
    g4: LineSegment StartX=5 StartY=-32 StartZ=0 EndX=-5 EndY=-32 EndZ=0
    g5: LineSegment StartX=-5 StartY=-32 StartZ=0 EndX=-5 EndY=0 EndZ=0
  constraints (18):
    c: PointOnObject(g0,g-1)
    c: Horizontal(g0)
    c: Coincident(g0,g1)
    c: Vertical(g1)
    c: Coincident(g1,g2)
    c: Horizontal(g2)
    c: Coincident(g2,g3)
    c: Vertical(g3)
    c: Coincident(g3,g4)
    c: Horizontal(g4)
    c: Coincident(g4,g5)
    c: Coincident(g5,g0)
    c: Vertical(g5)
    c: DistanceY(g1,g1) = 7
    c: DistanceX(g-1,g2) = 5
    c: DistanceX(g2,g2) = 10
    c: DistanceY(g3,g3) = 25
    c: DistanceX(g0,g-1) = 5
FEATURE [PartDesign::Pad] Pad024
  AddSubType = 0
  AutoTaperInnerAngle = false
  CheckUpToFaceLimits = true
  ClaimChildren = false
  Direction = (1,1,1)
  Fit = 0
  FitJoin = 0
  InnerFit = 0
  InnerFitJoin = 0
  InvalidShape = false
  Length = 10
  Length2 = 100
  Linearize = true
  NewSolid = false
  Placement = pos=(0,0,0) rot=(1,0,0;1.5708rad)
  Profile = -> Sketch037
  Refine = true
  Reversed = true
  Suppress = false
  TaperInnerAngle = 0
  TaperInnerAngleRev = 0
  TreeRank = 0
  Type = 0
  ValidateShape = true
  _ProfileBasedVersion = 1
FEATURE [PartDesign::Pad] Pad025
  AddSubType = 0
  AutoTaperInnerAngle = false
  BaseFeature = -> Pad024
  CheckUpToFaceLimits = true
  ClaimChildren = false
  Direction = (1,1,1)
  Fit = 0
  FitJoin = 0
  InnerFit = 0
  InnerFitJoin = 0
  InvalidShape = false
  Length = 5
  Length2 = 100
  Linearize = true
  NewSolid = false
  Placement = pos=(0,0,0) rot=(1,0,0;1.5708rad)
  Profile = -> Sketch037
  Refine = true
  Suppress = false
  TaperInnerAngle = 0
  TaperInnerAngleRev = 0
  TreeRank = 0
  Type = 0
  ValidateShape = true
  _ProfileBasedVersion = 1
FEATURE [Sketcher::SketchObject] Sketch038
  ArcFitTolerance = 0
  AttachmentSupport = -> [XZ_Plane030]
  ExternalBSplineMaxDegree = 0
  ExternalBSplineTolerance = 0
  ExternalGeometry = -> [Pad025]
  FullyConstrained = true
  InternalTolerance = 1e-06
  InvalidShape = false
  MakeInternals = false
  MapMode = 5
  Placement = pos=(0,0,0) rot=(1,0,0;1.5708rad)
  Support = -> [XZ_Plane030]
  TreeRank = 0
  ValidateShape = true
  sketch-geometry (4):
    g0: LineSegment StartX=0 StartY=0 StartZ=0 EndX=-5 EndY=0 EndZ=0
    g1: LineSegment StartX=-5 StartY=0 StartZ=0 EndX=-5 EndY=-32 EndZ=0
    g2: LineSegment StartX=-5 StartY=-32 StartZ=0 EndX=0 EndY=-32 EndZ=0
    g3: LineSegment StartX=0 StartY=-32 StartZ=0 EndX=0 EndY=0 EndZ=0
  constraints (10):
    c: Coincident(g0,g1)
    c: Coincident(g1,g2)
    c: Coincident(g2,g3)
    c: Coincident(g3,g0)
    c: Horizontal(g0)
    c: Horizontal(g2)
    c: Vertical(g1)
    c: Vertical(g3)
    c: Coincident(g0,g-1)
    c: Coincident(g-3,g1)
FEATURE [PartDesign::Pocket] Pocket013
  AddSubType = 1
  AutoTaperInnerAngle = false
  BaseFeature = -> Pad025
  CheckUpToFaceLimits = true
  ClaimChildren = false
  Fit = 0
  FitJoin = 0
  InnerFit = 0
  InnerFitJoin = 0
  InvalidShape = false
  Length = 5
  Length2 = 100
  Linearize = true
  NewSolid = false
  Placement = pos=(0,0,0) rot=(1,0,0;1.5708rad)
  Profile = -> Sketch038
  Refine = true
  Suppress = false
  TaperInnerAngle = 0
  TaperInnerAngleRev = 0
  TreeRank = 0
  Type = 1
  ValidateShape = true
  _ProfileBasedVersion = 1
  _Version = 0
FEATURE [Sketcher::SketchObject] Sketch039
  ArcFitTolerance = 0
  AttachmentSupport = -> [Pocket013]
  ExternalBSplineMaxDegree = 0
  ExternalBSplineTolerance = 0
  ExternalGeometry = -> [Pocket013]
  FullyConstrained = true
  InternalTolerance = 1e-06
  InvalidShape = false
  MakeInternals = false
  MapMode = 5
  Placement = pos=(0,-5,-1.1e-15) rot=(1,0,0;1.5708rad)
  Support = -> [Pocket013]
  TreeRank = 0
  ValidateShape = true
  sketch-geometry (3):
    g0: LineSegment StartX=15 StartY=-7 StartZ=0 EndX=5 EndY=-19.5 EndZ=0
    g1: LineSegment StartX=5 StartY=-7 StartZ=0 EndX=5 EndY=-19.5 EndZ=0
    g2: LineSegment StartX=5 StartY=-7 StartZ=0 EndX=15 EndY=-7 EndZ=0
  constraints (6):
    c: Coincident(g0,g-3)
    c: Coincident(g1,g-4)
    c: Coincident(g1,g0)
    c: Coincident(g2,g1)
    c: Coincident(g2,g0)
    c: Symmetric(g1,g-4,g0)
FEATURE [PartDesign::Pad] Pad026
  AddSubType = 0
  AutoTaperInnerAngle = false
  BaseFeature = -> Pocket013
  CheckUpToFaceLimits = true
  ClaimChildren = false
  Direction = (1,1,1)
  Fit = 0
  FitJoin = 0
  InnerFit = 0
  InnerFitJoin = 0
  InvalidShape = false
  Length = 2
  Length2 = 100
  Linearize = true
  NewSolid = false
  Placement = pos=(0,0,0) rot=(1,0,0;1.5708rad)
  Profile = -> Sketch039
  Refine = true
  Reversed = true
  Suppress = false
  TaperInnerAngle = 0
  TaperInnerAngleRev = 0
  TreeRank = 0
  Type = 0
  ValidateShape = true
  _ProfileBasedVersion = 1
FEATURE [Sketcher::SketchObject] Sketch040
  ArcFitTolerance = 0
  AttachmentSupport = -> [XY_Plane030]
  ExternalBSplineMaxDegree = 0
  ExternalBSplineTolerance = 0
  ExternalGeometry = -> [Pad026]
  FullyConstrained = true
  InternalTolerance = 1e-06
  InvalidShape = false
  MakeInternals = false
  MapMode = 5
  Support = -> [XY_Plane030]
  TreeRank = 0
  ValidateShape = true
  sketch-geometry (1):
    g0: Circle CenterX=10 CenterY=5 CenterZ=0 NormalX=0 NormalY=0 NormalZ=1 AngleXU=0 Radius=2.05
  constraints (3):
    c: DistanceX(g0,g-3) = 5
    c: DistanceY(g0,g-3) = 5
    c: Diameter(g0) = 4.1
FEATURE [PartDesign::Pocket] Pocket014
  AddSubType = 1
  AutoTaperInnerAngle = false
  BaseFeature = -> Pad026
  CheckUpToFaceLimits = true
  ClaimChildren = false
  Fit = 0
  FitJoin = 0
  InnerFit = 0
  InnerFitJoin = 0
  InvalidShape = false
  Length = 5
  Length2 = 100
  Linearize = true
  NewSolid = false
  Placement = pos=(0,0,0) rot=(1,0,0;1.5708rad)
  Profile = -> Sketch040
  Refine = true
  Suppress = false
  TaperInnerAngle = 0
  TaperInnerAngleRev = 0
  TreeRank = 0
  Type = 1
  ValidateShape = true
  _ProfileBasedVersion = 1
  _Version = 0
FEATURE [Sketcher::SketchObject] Sketch041
  ArcFitTolerance = 0
  AttachmentSupport = -> [Pocket014]
  ExternalBSplineMaxDegree = 0
  ExternalBSplineTolerance = 0
  ExternalGeometry = -> [Pocket014]
  FullyConstrained = true
  InternalTolerance = 1e-06
  InvalidShape = false
  MakeInternals = false
  MapMode = 5
  Placement = pos=(5,0,0) rot=(0.707107,0,0.707107;3.14159rad)
  Support = -> [Pocket014]
  TreeRank = 0
  ValidateShape = true
  sketch-geometry (4):
    g0: Circle CenterX=-27 CenterY=-5 CenterZ=0 NormalX=0 NormalY=0 NormalZ=1 AngleXU=0 Radius=1.6
    g1: Circle CenterX=-12 CenterY=-5 CenterZ=0 NormalX=0 NormalY=0 NormalZ=1 AngleXU=0 Radius=1.6
    g2: LineSegment [constr] StartX=-32 StartY=-5 StartZ=0 EndX=-7 EndY=-5 EndZ=0
    g3: GeomPoint [constr] X=-19.5 Y=-5 Z=0
  constraints (10):
    c: Diameter(g0) = 3.2
    c: Equal(g0,g1)
    c: Horizontal(g1,g0)
    c: PointOnObject(g2,g-4)
    c: PointOnObject(g2,g-3)
    c: Horizontal(g2)
    c: DistanceY(g-5,g2) = 5
    c: Symmetric(g2,g2,g3)
    c: Symmetric(g0,g1,g3)
    c: DistanceX(g2,g0) = 5
FEATURE [PartDesign::Pocket] Pocket015
  AddSubType = 1
  AutoTaperInnerAngle = false
  BaseFeature = -> Pocket014
  CheckUpToFaceLimits = true
  ClaimChildren = false
  Fit = 0
  FitJoin = 0
  InnerFit = 0
  InnerFitJoin = 0
  InvalidShape = false
  Length = 5
  Length2 = 100
  Linearize = true
  NewSolid = false
  Placement = pos=(0,0,0) rot=(1,0,0;1.5708rad)
  Profile = -> Sketch041
  Refine = true
  Suppress = false
  TaperInnerAngle = 0
  TaperInnerAngleRev = 0
  TreeRank = 0
  Type = 1
  ValidateShape = true
  _ProfileBasedVersion = 1
  _Version = 0
FEATURE [Sketcher::SketchObject] Sketch042
  ArcFitTolerance = 0
  AttachmentSupport = -> [Pocket015]
  ExternalBSplineMaxDegree = 0
  ExternalBSplineTolerance = 0
  ExternalGeometry = -> [Pocket015]
  FullyConstrained = true
  InternalTolerance = 1e-06
  InvalidShape = false
  MakeInternals = false
  MapMode = 5
  Placement = pos=(5,0,0) rot=(0.707107,0,0.707107;3.14159rad)
  Support = -> [Pocket015]
  TreeRank = 0
  ValidateShape = true
  sketch-geometry (5):
    g0: LineSegment StartX=-32 StartY=-10 StartZ=0 EndX=-32 EndY=-0.75 EndZ=0
    g1: LineSegment StartX=-32 StartY=-10 StartZ=0 EndX=-7.75 EndY=-10 EndZ=0
    g2: LineSegment StartX=-7.75 StartY=-10 StartZ=0 EndX=-7.75 EndY=-5 EndZ=0
    g3: ArcOfCircle CenterX=-12 CenterY=-5 CenterZ=0 NormalX=0 NormalY=0 NormalZ=1 AngleXU=0 Radius=4.25 StartAngle=0 EndAngle=1.5708
    g4: LineSegment StartX=-32 StartY=-0.75 StartZ=0 EndX=-12 EndY=-0.75 EndZ=0
  constraints (12):
    c: Coincident(g0,g-4)
    c: PointOnObject(g0,g-3)
    c: Coincident(g1,g0)
    c: PointOnObject(g1,g-4)
    c: Coincident(g2,g1)
    c: Vertical(g2)
    c: Coincident(g4,g0)
    c: Horizontal(g4)
    c: Tangent(g4,g3) = 1.5708
    c: Tangent(g3,g2) = -1.5708
    c: Coincident(g3,g-5)
    c: Diameter(g3) = 8.5
FEATURE [PartDesign::Pocket] Pocket016
  AddSubType = 1
  AutoTaperInnerAngle = false
  BaseFeature = -> Pocket015
  CheckUpToFaceLimits = true
  ClaimChildren = false
  Fit = 0
  FitJoin = 0
  InnerFit = 0
  InnerFitJoin = 0
  InvalidShape = false
  Length = 2.5
  Length2 = 100
  Linearize = true
  NewSolid = false
  Placement = pos=(0,0,0) rot=(1,0,0;1.5708rad)
  Profile = -> Sketch042
  Refine = true
  Suppress = false
  TaperInnerAngle = 0
  TaperInnerAngleRev = 0
  TreeRank = 0
  Type = 0
  ValidateShape = true
  _ProfileBasedVersion = 1
  _Version = 0
FEATURE [PartDesign::Chamfer] Chamfer006
  AddSubType = 0
  Angle = 45
  Base = -> Pocket016 [Edge46,Edge41,Edge42,Edge39,Edge40,Edge36]
  BaseFeature = -> Pocket016
  ChamferType = 0
  FlipDirection = false
  InvalidShape = false
  NewSolid = false
  Placement = pos=(0,0,0) rot=(1,0,0;1.5708rad)
  Refine = true
  Size = 0.2
  Size2 = 1
  SupportTransform = false
  Suppress = false
  TreeRank = 0
  ValidateShape = true
FEATURE [PartDesign::Chamfer] Chamfer005
  AddSubType = 0
  Angle = 45
  Base = -> Chamfer006 [Edge9,Edge36,Edge45,Edge21,Edge13]
  BaseFeature = -> Chamfer006
  ChamferType = 0
  FlipDirection = false
  InvalidShape = false
  NewSolid = false
  Placement = pos=(0,0,0) rot=(1,0,0;1.5708rad)
  Refine = true
  Size = 1
  Size2 = 1
  SupportTransform = false
  Suppress = false
  TreeRank = 0
  ValidateShape = true
FEATURE [PartDesign::Body] Body023  label="BodySupport3DInter"
  AutoGroupSolids = false
  ClaimAllChildren = false
  ExportMode = 0
  Group = -> [Sketch037,Pad024,Pad025,Sketch038,Pocket013,Sketch039,Pad026,Sketch040,Pocket014,Sketch041,Pocket015,Sketch042,Pocket016,Chamfer006,Chamfer005]
  InvalidShape = false
  Origin = -> Origin034
  SingleSolid = true
  Tip = -> Chamfer005
  TreeRank = 0
  ValidateShape = true
  _ExportChildren = -> [Pad024,Pad025,Pocket013,Pad026,Pocket014,Pocket015,Pocket016,Chamfer006,Chamfer005]
  _GroupVersion = 1
FEATURE [Part::Mirroring] Part__Mirroring  label="BodySupport3DInter (Mirror #1)"
  Base = (0,0,0)
  InvalidShape = false
  Normal = (1,0,0)
  Source = -> Body023
  TreeRank = 0
  ValidateShape = true
FEATURE [App::Part] Part004  label="SupportGauche3D"
  ClaimAllChildren = false
  ExportMode = 1
  Group = -> [Body023,Part__Mirroring]
  Origin = -> Origin033
  TreeRank = 0
  _ExportChildren = -> [Part__Mirroring]
  _GroupVersion = 1
FEATURE [App::Link] Link054  label="Link054(BodySupport3DInter)"
  AutoLinkLabel = true
  AutoPlacement = true
  LinkedObject = -> Body023
  SyncGroupVisibility = false
  TreeRank = 0
  _LinkVersion = 1
FEATURE [App::Part] Part005  label="SupportDroit3D"
  ClaimAllChildren = false
  ExportMode = 1
  Group = -> [Link054]
  Origin = -> Origin035
  TreeRank = 0
  _ExportChildren = -> [Link054]
  _GroupVersion = 1
FEATURE [Sketcher::SketchObject] Sketch049
  ArcFitTolerance = 0
  AttachmentSupport = -> [XY_Plane033]
  ExternalBSplineMaxDegree = 0
  ExternalBSplineTolerance = 0
  FullyConstrained = true
  InternalTolerance = 1e-06
  InvalidShape = false
  MakeInternals = false
  MapMode = 5
  Support = -> [XY_Plane033]
  TreeRank = 0
  ValidateShape = true
  sketch-geometry (13):
    g0: LineSegment [constr] StartX=0 StartY=0 StartZ=0 EndX=0 EndY=12.5 EndZ=0
    g1: LineSegment StartX=0 StartY=12.5 StartZ=0 EndX=5 EndY=21.1603 EndZ=0
    g2: LineSegment StartX=5 StartY=21.1603 StartZ=0 EndX=13.6603 EndY=16.1603 EndZ=0
    g3: LineSegment StartX=13.6603 StartY=16.1603 StartZ=0 EndX=4.33013 EndY=0 EndZ=0
    g4: LineSegment StartX=4.33013 StartY=0 StartZ=0 EndX=0 EndY=0 EndZ=0
    g5: LineSegment StartX=0 StartY=12.5 StartZ=0 EndX=-2 EndY=12.5 EndZ=0
    g6: LineSegment StartX=-2 StartY=12.5 StartZ=0 EndX=-2 EndY=10 EndZ=0
    g7: LineSegment StartX=-2 StartY=10 StartZ=0 EndX=0 EndY=10 EndZ=0
    g8: LineSegment StartX=0 StartY=10 StartZ=0 EndX=0 EndY=6.25 EndZ=0
    g9: LineSegment StartX=0 StartY=6.25 StartZ=0 EndX=-2 EndY=6.25 EndZ=0
    g10: LineSegment StartX=-2 StartY=6.25 StartZ=0 EndX=-2 EndY=3.75 EndZ=0
    g11: LineSegment StartX=-2 StartY=3.75 StartZ=0 EndX=0 EndY=3.75 EndZ=0
    g12: LineSegment StartX=0 StartY=3.75 StartZ=0 EndX=0 EndY=0 EndZ=0
  constraints (37):
    c: Coincident(g-1,g0)
    c: PointOnObject(g0,g-2)
    c: Coincident(g1,g2)
    c: Coincident(g2,g3)
    c: PointOnObject(g3,g-1)
    c: Coincident(g3,g4)
    c: Coincident(g4,g0)
    c: Perpendicular(g2,g1)
    c: Perpendicular(g2,g3)
    c: DistanceY(g0,g0) = 12.5
    c: Distance(g2) = 10
    c: Distance(g1) = 10
    c: Horizontal(g5)
    c: Coincident(g6,g5)
    c: Vertical(g6)
    c: Coincident(g7,g6)
    c: PointOnObject(g7,g0)
    c: Horizontal(g7)
    c: Coincident(g8,g7)
    c: PointOnObject(g8,g0)
    c: Coincident(g9,g8)
    c: Coincident(g10,g9)
    c: Coincident(g11,g10)
    c: PointOnObject(g11,g0)
    c: Coincident(g12,g11)
    c: Coincident(g12,g4)
    c: Perpendicular(g10,g9)
    c: Perpendicular(g10,g11)
    c: Parallel(g10,g8)
    c: Equal(g8,g12)
    c: DistanceY(g4,g7) = 10
    c: DistanceY(g10,g10) = 2.5
    c: DistanceX(g9,g9) = 2
    c: DistanceX(g5,g5) = 2
    c: Coincident(g1,g5)
    c: Coincident(g1,g0)
    c: Angle(g1,g5) = 2.0944
FEATURE [PartDesign::Pad] Pad029
  AddSubType = 0
  AutoTaperInnerAngle = false
  CheckUpToFaceLimits = true
  ClaimChildren = false
  Direction = (1,1,1)
  Fit = 0
  FitJoin = 0
  InnerFit = 0
  InnerFitJoin = 0
  InvalidShape = false
  Length = 7
  Length2 = 100
  Linearize = true
  NewSolid = false
  Profile = -> Sketch049
  Refine = true
  Suppress = false
  TaperInnerAngle = 0
  TaperInnerAngleRev = 0
  TreeRank = 0
  Type = 0
  ValidateShape = true
  _ProfileBasedVersion = 1
FEATURE [Sketcher::SketchObject] Sketch051
  ArcFitTolerance = 0
  AttachmentSupport = -> [XY_Plane033]
  ExternalBSplineMaxDegree = 0
  ExternalBSplineTolerance = 0
  ExternalGeometry = -> [Pad029]
  FullyConstrained = true
  InternalTolerance = 1e-06
  InvalidShape = false
  MakeInternals = false
  MapMode = 5
  Support = -> [XY_Plane033]
  TreeRank = 0
  ValidateShape = true
  sketch-geometry (4):
    g0: LineSegment StartX=4.33013 StartY=10 StartZ=0 EndX=4.33013 EndY=0 EndZ=0
    g1: LineSegment StartX=0 StartY=6.25 StartZ=0 EndX=0 EndY=3.75 EndZ=0
    g2: LineSegment StartX=4.33013 StartY=10 StartZ=0 EndX=0 EndY=12.5 EndZ=0
    g3: LineSegment StartX=0 StartY=12.5 StartZ=0 EndX=-2 EndY=12.5 EndZ=0
  constraints (10):
    c: Vertical(g0)
    c: Coincident(g1,g-8)
    c: Coincident(g1,g-5)
    c: Coincident(g0,g-11)
    c: Coincident(g2,g0)
    c: PointOnObject(g2,g-12)
    c: Coincident(g3,g-10)
    c: Coincident(g2,g3)
    c: Horizontal(g3)
    c: Perpendicular(g-12,g2)
FEATURE [PartDesign::Pad] Pad030
  AddSubType = 0
  AutoTaperInnerAngle = false
  BaseFeature = -> Pad029
  CheckUpToFaceLimits = true
  ClaimChildren = false
  Direction = (1,1,1)
  Fit = 0
  FitJoin = 0
  InnerFit = 0
  InnerFitJoin = 0
  InvalidShape = false
  Length = 15
  Length2 = 100
  Linearize = true
  NewSolid = false
  Profile = -> Sketch051
  Refine = true
  Reversed = true
  Suppress = false
  TaperInnerAngle = 0
  TaperInnerAngleRev = 0
  TreeRank = 0
  Type = 0
  ValidateShape = true
  _ProfileBasedVersion = 1
FEATURE [Sketcher::SketchObject] Sketch052
  ArcFitTolerance = 0
  AttachmentSupport = -> [YZ_Plane033]
  ExternalBSplineMaxDegree = 0
  ExternalBSplineTolerance = 0
  ExternalGeometry = -> [Pad030]
  FullyConstrained = true
  InternalTolerance = 1e-06
  InvalidShape = false
  MakeInternals = false
  MapMode = 5
  Placement = pos=(0,0,0) rot=(0.57735,0.57735,0.57735;2.0944rad)
  Support = -> [YZ_Plane033]
  TreeRank = 0
  ValidateShape = true
  sketch-geometry (1):
    g0: Circle CenterX=5 CenterY=-10 CenterZ=0 NormalX=0 NormalY=0 NormalZ=1 AngleXU=0 Radius=1.6
  constraints (3):
    c: DistanceX(g0) = 5
    c: Diameter(g0) = 3.2
    c: DistanceY(g-3,g0) = 5
FEATURE [PartDesign::Pocket] Pocket020
  AddSubType = 1
  AutoTaperInnerAngle = false
  BaseFeature = -> Pad030
  CheckUpToFaceLimits = true
  ClaimChildren = false
  Fit = 0
  FitJoin = 0
  InnerFit = 0
  InnerFitJoin = 0
  InvalidShape = false
  Length = 5
  Length2 = 100
  Linearize = true
  NewSolid = false
  Profile = -> Sketch052
  Refine = true
  Reversed = true
  Suppress = false
  TaperInnerAngle = 0
  TaperInnerAngleRev = 0
  TreeRank = 0
  Type = 1
  ValidateShape = true
  _ProfileBasedVersion = 1
  _Version = 0
FEATURE [Sketcher::SketchObject] Sketch054
  ArcFitTolerance = 0
  AttachmentSupport = -> [XY_Plane033]
  ExternalBSplineMaxDegree = 0
  ExternalBSplineTolerance = 0
  ExternalGeometry = -> [Pocket020]
  FullyConstrained = true
  InternalTolerance = 1e-06
  InvalidShape = false
  MakeInternals = false
  MapMode = 5
  Support = -> [XY_Plane033]
  TreeRank = 0
  ValidateShape = true
  sketch-geometry (3):
    g0: Circle CenterX=6.83013 CenterY=14.3301 CenterZ=0 NormalX=0 NormalY=0 NormalZ=1 AngleXU=0 Radius=2.1
    g1: LineSegment [constr] StartX=9.33013 StartY=18.6603 StartZ=0 EndX=6.83013 EndY=14.3301 EndZ=0
    g2: LineSegment [constr] StartX=6.83013 StartY=14.3301 StartZ=0 EndX=11.1603 EndY=11.8301 EndZ=0
  constraints (11):
    c: Diameter(g0) = 4.2
    c: Coincident(g1,g0)
    c: Coincident(g1,g2)
    c: Perpendicular(g1,g2)
    c: Distance(g1) = 5
    c: Distance(g2) = 5
    c: PointOnObject(g2,g-4)
    c: PointOnObject(g1,g-3)
    c: Perpendicular(g-3,g1)
    c: DistanceX(g-1,g0) = 6.83013
    c: DistanceY(g-1,g0) = 14.3301
FEATURE [PartDesign::Pocket] Pocket022
  AddSubType = 1
  AutoTaperInnerAngle = false
  BaseFeature = -> Pocket020
  CheckUpToFaceLimits = true
  ClaimChildren = false
  Fit = 0
  FitJoin = 0
  InnerFit = 0
  InnerFitJoin = 0
  InvalidShape = false
  Length = 5
  Length2 = 100
  Linearize = true
  NewSolid = false
  Profile = -> Sketch054
  Refine = true
  Reversed = true
  Suppress = false
  TaperInnerAngle = 0
  TaperInnerAngleRev = 0
  TreeRank = 0
  Type = 1
  ValidateShape = true
  _ProfileBasedVersion = 1
  _Version = 0
FEATURE [Sketcher::SketchObject] Sketch055
  ArcFitTolerance = 0
  AttachmentSupport = -> [Pocket022]
  ExternalBSplineMaxDegree = 0
  ExternalBSplineTolerance = 0
  ExternalGeometry = -> [Pocket022]
  FullyConstrained = true
  InternalTolerance = 1e-06
  InvalidShape = false
  MakeInternals = false
  MapMode = 5
  Placement = pos=(4.33013,0,0) rot=(0.57735,0.57735,0.57735;2.0944rad)
  Support = -> [Pocket022]
  TreeRank = 0
  ValidateShape = true
  sketch-geometry (4):
    g0: LineSegment StartX=0 StartY=-15 StartZ=0 EndX=12.5 EndY=-15 EndZ=0
    g1: LineSegment StartX=12.5 StartY=-15 StartZ=0 EndX=12.5 EndY=-5 EndZ=0
    g2: LineSegment StartX=12.5 StartY=-5 StartZ=0 EndX=0 EndY=-5 EndZ=0
    g3: LineSegment StartX=0 StartY=-5 StartZ=0 EndX=0 EndY=-15 EndZ=0
  constraints (11):
    c: Coincident(g0,g1)
    c: Coincident(g1,g2)
    c: Coincident(g2,g3)
    c: Coincident(g3,g0)
    c: Horizontal(g0)
    c: Horizontal(g2)
    c: Vertical(g1)
    c: Vertical(g3)
    c: PointOnObject(g1,g-4)
    c: Coincident(g0,g-3)
    c: DistanceY(g3,g3) = 10
FEATURE [PartDesign::Pocket] Pocket023
  AddSubType = 1
  AutoTaperInnerAngle = false
  BaseFeature = -> Pocket022
  CheckUpToFaceLimits = true
  ClaimChildren = false
  Fit = 0
  FitJoin = 0
  InnerFit = 0
  InnerFitJoin = 0
  InvalidShape = false
  Length = 1.9
  Length2 = 100
  Linearize = true
  NewSolid = false
  Profile = -> Sketch055
  Refine = true
  Suppress = false
  TaperInnerAngle = 0
  TaperInnerAngleRev = 0
  TreeRank = 0
  Type = 0
  ValidateShape = true
  _ProfileBasedVersion = 1
  _Version = 0
FEATURE [Sketcher::SketchObject] Sketch056
  ArcFitTolerance = 0
  AttachmentSupport = -> [XY_Plane033]
  ExternalBSplineMaxDegree = 0
  ExternalBSplineTolerance = 0
  ExternalGeometry = -> [Pocket023]
  FullyConstrained = true
  InternalTolerance = 1e-06
  InvalidShape = false
  MakeInternals = false
  MapMode = 5
  Support = -> [XY_Plane033]
  TreeRank = 0
  ValidateShape = true
  sketch-geometry (3):
    g0: LineSegment StartX=4.33013 StartY=10 StartZ=0 EndX=4.33013 EndY=0 EndZ=0
    g1: LineSegment StartX=4.33013 StartY=0 StartZ=0 EndX=8.66025 EndY=7.5 EndZ=0
    g2: LineSegment StartX=8.66025 StartY=7.5 StartZ=0 EndX=4.33013 EndY=10 EndZ=0
  constraints (7):
    c: Coincident(g-5,g0)
    c: Coincident(g0,g-4)
    c: Coincident(g0,g1)
    c: PointOnObject(g1,g-4)
    c: Coincident(g1,g2)
    c: Coincident(g2,g0)
    c: Parallel(g2,g-5)
FEATURE [PartDesign::Pad] Pad031
  AddSubType = 0
  AutoTaperInnerAngle = false
  BaseFeature = -> Pocket023
  CheckUpToFaceLimits = true
  ClaimChildren = false
  Direction = (1,1,1)
  Fit = 0
  FitJoin = 0
  InnerFit = 0
  InnerFitJoin = 0
  InvalidShape = false
  Length = 10
  Length2 = 100
  Linearize = true
  NewSolid = false
  Profile = -> Sketch056
  Refine = true
  Reversed = true
  Suppress = false
  TaperInnerAngle = 0
  TaperInnerAngleRev = 0
  TreeRank = 0
  Type = 3
  UpToFace = -> Pocket023 [Face19]
  ValidateShape = true
  _ProfileBasedVersion = 1
FEATURE [PartDesign::Draft] Draft
  AddSubType = 0
  Angle = 38.5
  Base = -> Pad031 [Face20]
  BaseFeature = -> Pad031
  InvalidShape = false
  NeutralPlane = -> Pad031 [Face15]
  NewSolid = false
  Refine = true
  SupportTransform = false
  Suppress = false
  TreeRank = 0
  ValidateShape = true
FEATURE [PartDesign::Chamfer] Chamfer009
  AddSubType = 0
  Angle = 45
  Base = -> Draft [Edge26]
  BaseFeature = -> Draft
  ChamferType = 0
  FlipDirection = false
  InvalidShape = false
  NewSolid = false
  Refine = true
  Size = 2
  Size2 = 1
  SupportTransform = false
  Suppress = false
  TreeRank = 0
  ValidateShape = true
FEATURE [PartDesign::Draft] Draft001
  AddSubType = 0
  Angle = 66.5
  Base = -> Chamfer009 [Face16]
  BaseFeature = -> Chamfer009
  InvalidShape = false
  NeutralPlane = -> Chamfer009 [Face21]
  NewSolid = false
  Refine = true
  Reversed = true
  SupportTransform = false
  Suppress = false
  TreeRank = 0
  ValidateShape = true
FEATURE [PartDesign::Chamfer] Chamfer010
  AddSubType = 0
  Angle = 45
  Base = -> Draft001 [Edge51,Edge50,Edge54,Edge53]
  BaseFeature = -> Draft001
  ChamferType = 0
  FlipDirection = false
  InvalidShape = false
  NewSolid = false
  Refine = true
  Size = 0.4
  Size2 = 1
  SupportTransform = false
  Suppress = false
  TreeRank = 0
  ValidateShape = true
FEATURE [PartDesign::Chamfer] Chamfer011
  AddSubType = 0
  Angle = 45
  Base = -> Chamfer010 [Edge45]
  BaseFeature = -> Chamfer010
  ChamferType = 0
  FlipDirection = false
  InvalidShape = false
  NewSolid = false
  Refine = true
  Size = 1
  Size2 = 1
  SupportTransform = false
  Suppress = false
  TreeRank = 0
  ValidateShape = true
FEATURE [PartDesign::Chamfer] Chamfer012
  AddSubType = 0
  Angle = 45
  Base = -> Chamfer011 [Edge10,Edge19]
  BaseFeature = -> Chamfer011
  ChamferType = 0
  FlipDirection = false
  InvalidShape = false
  NewSolid = false
  Refine = true
  Size = 0.2
  Size2 = 1
  SupportTransform = false
  Suppress = false
  TreeRank = 0
  ValidateShape = true
FEATURE [PartDesign::Chamfer] Chamfer013
  AddSubType = 0
  Angle = 45
  Base = -> Chamfer012 [Edge64,Edge38]
  BaseFeature = -> Chamfer012
  ChamferType = 0
  FlipDirection = false
  InvalidShape = false
  NewSolid = false
  Refine = true
  Size = 1
  Size2 = 1
  SupportTransform = false
  Suppress = false
  TreeRank = 0
  ValidateShape = true
FEATURE [PartDesign::Fillet] Fillet016
  AddSubType = 0
  Base = -> Chamfer013 [Edge37]
  BaseFeature = -> Chamfer013
  InvalidShape = false
  NewSolid = false
  Radius = 2
  Refine = true
  SupportTransform = false
  Suppress = false
  TreeRank = 0
  ValidateShape = true
FEATURE [PartDesign::Chamfer] Chamfer014
  AddSubType = 0
  Angle = 45
  Base = -> Fillet016 [Edge20,Edge70,Edge79,Edge44]
  BaseFeature = -> Fillet016
  ChamferType = 0
  FlipDirection = false
  InvalidShape = false
  NewSolid = false
  Refine = true
  Size = 0.2
  Size2 = 1
  SupportTransform = false
  Suppress = false
  TreeRank = 0
  ValidateShape = true
FEATURE [Sketcher::SketchObject] Sketch057
  ArcFitTolerance = 0
  AttachmentSupport = -> [XY_Plane033]
  ExternalBSplineMaxDegree = 0
  ExternalBSplineTolerance = 0
  FullyConstrained = false
  InternalTolerance = 1e-06
  InvalidShape = false
  MakeInternals = false
  MapMode = 5
  Support = -> [XY_Plane033]
  TreeRank = 0
  ValidateShape = true
  sketch-geometry (4):
    g0: LineSegment StartX=0 StartY=15.6465 StartZ=0 EndX=-3.55109 EndY=15.6465 EndZ=0
    g1: LineSegment StartX=-3.55109 StartY=15.6465 StartZ=0 EndX=-3.55109 EndY=7.42705 EndZ=0
    g2: LineSegment StartX=-3.55109 StartY=7.42705 StartZ=0 EndX=0 EndY=7.42705 EndZ=0
    g3: LineSegment StartX=0 StartY=7.42705 StartZ=0 EndX=0 EndY=15.6465 EndZ=0
  constraints (9):
    c: Coincident(g0,g1)
    c: Coincident(g1,g2)
    c: Coincident(g2,g3)
    c: Coincident(g3,g0)
    c: Horizontal(g0)
    c: Horizontal(g2)
    c: Vertical(g1)
    c: Vertical(g3)
    c: PointOnObject(g0,g-2)
FEATURE [PartDesign::Pocket] Pocket024
  AddSubType = 1
  AutoTaperInnerAngle = false
  BaseFeature = -> Chamfer014
  CheckUpToFaceLimits = true
  ClaimChildren = false
  Fit = 0
  FitJoin = 0
  InnerFit = 0
  InnerFitJoin = 0
  InvalidShape = false
  Length = 39
  Length2 = 100
  Linearize = true
  Midplane = true
  NewSolid = false
  Profile = -> Sketch057
  Refine = true
  Suppress = false
  TaperInnerAngle = 0
  TaperInnerAngleRev = 0
  TreeRank = 0
  Type = 1
  ValidateShape = true
  _ProfileBasedVersion = 1
  _Version = 0
FEATURE [PartDesign::Chamfer] Chamfer015
  AddSubType = 0
  Angle = 45
  Base = -> Pocket024 [Edge69,Edge58,Edge54]
  BaseFeature = -> Pocket024
  ChamferType = 0
  FlipDirection = false
  InvalidShape = false
  NewSolid = false
  Refine = true
  Size = 0.5
  Size2 = 1
  SupportTransform = false
  Suppress = false
  TreeRank = 0
  ValidateShape = true
FEATURE [PartDesign::Body] Body026
  AutoGroupSolids = false
  ClaimAllChildren = false
  ExportMode = 0
  Group = -> [Sketch049,Sketch051,Sketch052,Sketch054,Pad029,Pad030,Pocket020,Pocket022,Sketch055,Pocket023,Sketch056,Pad031,Draft,Chamfer009,Draft001,Chamfer010,Chamfer011,Chamfer012,Chamfer013,Fillet016,Chamfer014,Sketch057,Pocket024,Chamfer015]
  InvalidShape = false
  Origin = -> Origin041
  SingleSolid = true
  Tip = -> Chamfer015
  TreeRank = 0
  ValidateShape = true
  _ExportChildren = -> [Pad029,Pad030,Pocket020,Pocket022,Pocket023,Pad031,Draft,Chamfer009,Draft001,Chamfer010,Chamfer011,Chamfer012,Chamfer013,Fillet016,Chamfer014,Pocket024,Chamfer015]
  _GroupVersion = 1
FEATURE [Part::Mirroring] Part__Mirroring001  label="Body026 (Mirror #2)"
  Base = (0,0,0)
  InvalidShape = false
  Normal = (1,0,0)
  Source = -> Body026
  TreeRank = 0
  ValidateShape = true
FEATURE [App::Part] Part008  label="SupportGauche120d"
  ClaimAllChildren = false
  ExportMode = 1
  Group = -> [Body026,Part__Mirroring001]
  Origin = -> Origin040
  TreeRank = 0
  _ExportChildren = -> [Part__Mirroring001]
  _GroupVersion = 1
FEATURE [App::Link] Link063  label="Link063(Body026)"
  AutoLinkLabel = true
  AutoPlacement = true
  LinkedObject = -> Body026
  SyncGroupVisibility = false
  TreeRank = 0
  _LinkVersion = 1
FEATURE [App::Part] Part009  label="SupportDroite120d"
  ClaimAllChildren = false
  ExportMode = 1
  Group = -> [Link063]
  Origin = -> Origin042
  TreeRank = 0
  _ExportChildren = -> [Link063]
  _GroupVersion = 1
FEATURE [Sketcher::SketchObject] Sketch045
  ArcFitTolerance = 0
  AttachmentSupport = -> [XY_Plane032]
  ExternalBSplineMaxDegree = 0
  ExternalBSplineTolerance = 0
  FullyConstrained = true
  InternalTolerance = 1e-06
  InvalidShape = false
  MakeInternals = false
  MapMode = 5
  Support = -> [XY_Plane032]
  TreeRank = 0
  ValidateShape = true
  sketch-geometry (6):
    g0: LineSegment StartX=40 StartY=50 StartZ=0 EndX=40 EndY=40 EndZ=0
    g1: LineSegment StartX=40 StartY=40 StartZ=0 EndX=47.3205 EndY=27.3205 EndZ=0
    g2: LineSegment [constr] StartX=0 StartY=0 StartZ=0 EndX=54.6506 EndY=31.5526 EndZ=0
    g3: LineSegment StartX=40 StartY=50 StartZ=0 EndX=44 EndY=50 EndZ=0
    g4: LineSegment StartX=44 StartY=50 StartZ=0 EndX=54.6506 EndY=31.5526 EndZ=0
    g5: LineSegment StartX=54.6506 StartY=31.5526 StartZ=0 EndX=47.3205 EndY=27.3205 EndZ=0
  constraints (17):
    c: Vertical(g0)
    c: Coincident(g1,g0)
    c: Coincident(g2,g-1)
    c: Angle(g2,g-2) = 1.0472
    c: PointOnObject(g1,g2)
    c: Coincident(g0,g3)
    c: Horizontal(g3)
    c: Coincident(g3,g4)
    c: Coincident(g4,g5)
    c: Coincident(g5,g1)
    c: Parallel(g1,g4)
    c: DistanceX(g2,g0) = 40
    c: DistanceY(g0,g0) = 10
    c: DistanceY(g0) = 40
    c: Perpendicular(g5,g1)
    c: DistanceX(g3,g3) = 4
    c: Coincident(g2,g4)
FEATURE [PartDesign::Plane] DatumPlane004
  AttachmentOffset = pos=(0,0,0) rot=(0,-1,0;1.0472rad)
  AttachmentSupport = -> [YZ_Plane032]
  InvalidShape = false
  Length = 81.5526
  MapMode = 5
  MinimumLength = 10
  MinimumWidth = 10
  Placement = pos=(0,0,0) rot=(0.935113,0.250563,0.250563;1.63783rad)
  ResizeMode = 0
  Support = -> [YZ_Plane032]
  TreeRank = 0
  ValidateShape = true
  Width = 30
FEATURE [PartDesign::Pad] Pad028
  AddSubType = 0
  AutoTaperInnerAngle = false
  CheckUpToFaceLimits = true
  ClaimChildren = false
  Direction = (1,1,1)
  Fit = 0
  FitJoin = 0
  InnerFit = 0
  InnerFitJoin = 0
  InvalidShape = false
  Length = 30
  Length2 = 100
  Linearize = true
  Midplane = true
  NewSolid = false
  Profile = -> Sketch045
  Refine = true
  Suppress = false
  TaperInnerAngle = 0
  TaperInnerAngleRev = 0
  TreeRank = 0
  Type = 0
  ValidateShape = true
  _ProfileBasedVersion = 1
FEATURE [PartDesign::Mirrored] Mirrored
  AddSubType = 0
  BaseFeature = -> Pad028
  CopyShape = false
  InvalidShape = false
  MirrorPlane = -> DatumPlane004
  NewSolid = false
  OriginalSubs = -> [Pad028]
  Originals = -> [Pad028]
  ParallelTransform = true
  Refine = true
  SubTransform = true
  Suppress = false
  TreeRank = 0
  ValidateShape = true
  _Version = 2
FEATURE [Sketcher::SketchObject] Sketch046
  ArcFitTolerance = 0
  AttachmentOffset = pos=(0,0,-10) rot=(0,0,1;0rad)
  AttachmentSupport = -> [Mirrored]
  ExternalBSplineMaxDegree = 0
  ExternalBSplineTolerance = 0
  ExternalGeometry = -> [Mirrored]
  FullyConstrained = true
  InternalTolerance = 1e-06
  InvalidShape = false
  MakeInternals = false
  MapMode = 5
  Placement = pos=(50,0,0) rot=(0.57735,-0.57735,-0.57735;2.0944rad)
  Support = -> [Mirrored]
  TreeRank = 0
  ValidateShape = true
  sketch-geometry (2):
    g0: Circle CenterX=-45 CenterY=10 CenterZ=0 NormalX=0 NormalY=0 NormalZ=1 AngleXU=0 Radius=1.5
    g1: LineSegment [constr] StartX=-45 StartY=15 StartZ=0 EndX=-45 EndY=-15 EndZ=0
  constraints (6):
    c: Diameter(g0) = 3
    c: DistanceY(g0) = 10
    c: PointOnObject(g1,g-4)
    c: Vertical(g1)
    c: Symmetric(g-3,g-3,g1)
    c: PointOnObject(g0,g1)
FEATURE [PartDesign::Hole] Hole
  AddSubType = 1
  BaseFeature = -> Mirrored
  ClaimChildren = false
  CustomThreadClearance = 0
  Depth = 25
  DepthType = 0
  Diameter = 3.2
  DrillForDepth = false
  DrillPoint = 1
  DrillPointAngle = 118
  Fit = 0
  FitJoin = 0
  HoleCutCountersinkAngle = 90
  HoleCutCustomValues = false
  HoleCutDepth = 7.5
  HoleCutDiameter = 8.5
  HoleCutType = 1
  InnerFit = 0
  InnerFitJoin = 0
  InvalidShape = false
  ModelThread = false
  NewSolid = false
  Profile = -> Sketch046
  Refine = true
  Reversed = true
  Suppress = false
  Tapered = false
  TaperedAngle = 90
  ThreadClass = 0
  ThreadDepth = 23.5
  ThreadDepthType = 0
  ThreadDirection = 0
  ThreadFit = 0
  ThreadSize = 0
  ThreadType = 0
  Threaded = false
  TreeRank = 0
  UseCustomThreadClearance = false
  ValidateShape = true
  _ProfileBasedVersion = 1
FEATURE [PartDesign::Mirrored] Mirrored001
  AddSubType = 0
  CopyShape = false
  InvalidShape = false
  MirrorPlane = -> XY_Plane032
  NewSolid = false
  ParallelTransform = true
  Refine = true
  SubTransform = true
  Suppress = false
  TreeRank = 0
  ValidateShape = true
  _Version = 2
FEATURE [PartDesign::Mirrored] Mirrored002
  AddSubType = 0
  CopyShape = false
  InvalidShape = false
  MirrorPlane = -> DatumPlane004
  NewSolid = false
  ParallelTransform = true
  Refine = true
  SubTransform = true
  Suppress = false
  TreeRank = 0
  ValidateShape = true
  _Version = 2
FEATURE [PartDesign::MultiTransform] MultiTransform002
  AddSubType = 0
  BaseFeature = -> Hole
  CopyShape = false
  InvalidShape = false
  NewSolid = false
  OriginalSubs = -> [Hole]
  Originals = -> [Hole]
  ParallelTransform = true
  Refine = true
  SubTransform = true
  Suppress = false
  Transformations = -> [Mirrored001,Mirrored002]
  TreeRank = 0
  ValidateShape = true
  _Version = 2
FEATURE [Sketcher::SketchObject] Sketch047
  ArcFitTolerance = 0
  AttachmentSupport = -> [MultiTransform002]
  ExternalBSplineMaxDegree = 0
  ExternalBSplineTolerance = 0
  FullyConstrained = true
  InternalTolerance = 1e-06
  InvalidShape = false
  MakeInternals = false
  MapMode = 5
  Placement = pos=(54.6506,31.5526,-6.3e-15) rot=(0.377964,0.654654,0.654654;2.41886rad)
  Support = -> [MultiTransform002]
  TreeRank = 0
  ValidateShape = true
  sketch-geometry (1):
    g0: Circle CenterX=7.5 CenterY=10 CenterZ=0 NormalX=0 NormalY=0 NormalZ=1 AngleXU=0 Radius=2.05
  constraints (3):
    c: Diameter(g0) = 4.1
    c: DistanceY(g-1,g0) = 10
    c: DistanceX(g-1,g0) = 7.5
FEATURE [PartDesign::Pocket] Pocket018
  AddSubType = 1
  AutoTaperInnerAngle = false
  BaseFeature = -> MultiTransform002
  CheckUpToFaceLimits = true
  ClaimChildren = false
  Fit = 0
  FitJoin = 0
  InnerFit = 0
  InnerFitJoin = 0
  InvalidShape = false
  Length = 5
  Length2 = 100
  Linearize = true
  NewSolid = false
  Profile = -> Sketch047
  Refine = true
  Suppress = false
  TaperInnerAngle = 0
  TaperInnerAngleRev = 0
  TreeRank = 0
  Type = 1
  ValidateShape = true
  _ProfileBasedVersion = 1
  _Version = 0
FEATURE [PartDesign::Mirrored] Mirrored003
  AddSubType = 0
  CopyShape = false
  InvalidShape = false
  MirrorPlane = -> DatumPlane004
  NewSolid = false
  ParallelTransform = true
  Refine = true
  SubTransform = true
  Suppress = false
  TreeRank = 0
  ValidateShape = true
  _Version = 2
FEATURE [PartDesign::Mirrored] Mirrored004
  AddSubType = 0
  CopyShape = false
  InvalidShape = false
  MirrorPlane = -> XY_Plane032
  NewSolid = false
  ParallelTransform = true
  Refine = true
  SubTransform = true
  Suppress = false
  TreeRank = 0
  ValidateShape = true
  _Version = 2
FEATURE [PartDesign::MultiTransform] MultiTransform003
  AddSubType = 0
  BaseFeature = -> Pocket018
  CopyShape = false
  InvalidShape = false
  NewSolid = false
  OriginalSubs = -> [Pocket018]
  Originals = -> [Pocket018]
  ParallelTransform = true
  Refine = true
  SubTransform = true
  Suppress = false
  Transformations = -> [Mirrored003,Mirrored004]
  TreeRank = 0
  ValidateShape = true
  _Version = 2
FEATURE [PartDesign::Chamfer] Chamfer008
  AddSubType = 0
  Angle = 45
  Base = -> MultiTransform003 [Edge5,Edge6,Edge38,Edge37,Edge21,Edge19,Edge20,Edge22,Edge30,Edge29,Edge33,Edge34,Edge32,Edge28,Edge35,Edge31]
  BaseFeature = -> MultiTransform003
  ChamferType = 0
  FlipDirection = false
  InvalidShape = false
  NewSolid = false
  Refine = true
  Size = 0.2
  Size2 = 1
  SupportTransform = false
  Suppress = false
  TreeRank = 0
  ValidateShape = true
FEATURE [Sketcher::SketchObject] Sketch048
  ArcFitTolerance = 0
  AttachmentSupport = -> [Chamfer008]
  ExternalBSplineMaxDegree = 0
  ExternalBSplineTolerance = 0
  FullyConstrained = true
  InternalTolerance = 1e-06
  InvalidShape = false
  MakeInternals = false
  MapMode = 5
  Placement = pos=(54.6506,31.5526,-6.3e-15) rot=(0.377964,0.654654,0.654654;2.41886rad)
  Support = -> [Chamfer008]
  TreeRank = 0
  ValidateShape = true
  sketch-geometry (16):
    g0: ArcOfCircle CenterX=-15 CenterY=0 CenterZ=0 NormalX=0 NormalY=0 NormalZ=1 AngleXU=0 Radius=1 StartAngle=1.5708 EndAngle=4.71239
    g1: ArcOfCircle CenterX=15 CenterY=0 CenterZ=0 NormalX=0 NormalY=0 NormalZ=1 AngleXU=0 Radius=1 StartAngle=4.71239 EndAngle=7.85398
    g2: LineSegment [constr] StartX=-15 StartY=-1 StartZ=0 EndX=15 EndY=-1 EndZ=0
    g3: LineSegment [constr] StartX=-15 StartY=1 StartZ=0 EndX=15 EndY=1 EndZ=0
    g4: ArcOfCircle CenterX=2.81924e-11 CenterY=-10 CenterZ=0 NormalX=0 NormalY=0 NormalZ=1 AngleXU=0 Radius=1 StartAngle=3.14159 EndAngle=6.28319
    g5: ArcOfCircle CenterX=-2.81924e-11 CenterY=10 CenterZ=0 NormalX=0 NormalY=0 NormalZ=1 AngleXU=0 Radius=1 StartAngle=0 EndAngle=3.14159
    g6: LineSegment [constr] StartX=1 StartY=-10 StartZ=0 EndX=1 EndY=10 EndZ=0
    g7: LineSegment [constr] StartX=-1 StartY=-10 StartZ=0 EndX=-1 EndY=10 EndZ=0
    g8: LineSegment StartX=-15 StartY=1 StartZ=0 EndX=-1 EndY=1 EndZ=0
    g9: LineSegment StartX=-1 StartY=1 StartZ=0 EndX=-1 EndY=10 EndZ=0
    g10: LineSegment StartX=1 StartY=10 StartZ=0 EndX=1 EndY=1 EndZ=0
    g11: LineSegment StartX=1 StartY=1 StartZ=0 EndX=15 EndY=1 EndZ=0
    g12: LineSegment StartX=-15 StartY=-1 StartZ=0 EndX=-1 EndY=-1 EndZ=0
    g13: LineSegment StartX=-1 StartY=-1 StartZ=0 EndX=-1 EndY=-10 EndZ=0
    g14: LineSegment StartX=1 StartY=-10 StartZ=0 EndX=1 EndY=-1 EndZ=0
    g15: LineSegment StartX=1 StartY=-1 StartZ=0 EndX=15 EndY=-1 EndZ=0
  constraints (36):
    c: Tangent(g0,g3) = 1.5708
    c: Tangent(g0,g2) = -1.5708
    c: Tangent(g2,g1) = -1.5708
    c: Tangent(g3,g1) = 1.5708
    c: Horizontal(g2)
    c: Equal(g0,g1)
    c: Tangent(g4,g7) = 1.5708
    c: Tangent(g4,g6) = -1.5708
    c: Tangent(g6,g5) = -1.5708
    c: Tangent(g7,g5) = 1.5708
    c: Vertical(g6)
    c: Equal(g4,g5)
    c: Equal(g5,g0)
    c: Symmetric(g0,g1,g-1)
    c: Symmetric(g4,g5,g-1)
    c: Diameter(g0) = 2
    c: DistanceX(g0,g1) = 30
    c: DistanceY(g4,g5) = 20
    c: Tangent(g0,g8) = 1.5708
    c: Coincident(g8,g9)
    c: Coincident(g9,g5)
    c: Vertical(g9)
    c: Tangent(g5,g10) = 1.5708
    c: Coincident(g11,g10)
    c: Coincident(g11,g1)
    c: Horizontal(g11)
    c: Coincident(g12,g0)
    c: PointOnObject(g12,g7)
    c: Horizontal(g12)
    c: Coincident(g13,g12)
    c: Coincident(g13,g4)
    c: Coincident(g14,g4)
    c: PointOnObject(g14,g2)
    c: Vertical(g14)
    c: Coincident(g15,g14)
    c: Coincident(g15,g1)
FEATURE [PartDesign::Pocket] Pocket019
  AddSubType = 1
  AutoTaperInnerAngle = false
  BaseFeature = -> Chamfer008
  CheckUpToFaceLimits = true
  ClaimChildren = false
  Fit = 0
  FitJoin = 0
  InnerFit = 0
  InnerFitJoin = 0
  InvalidShape = false
  Length = 0.7
  Length2 = 100
  Linearize = true
  NewSolid = false
  Profile = -> Sketch048
  Refine = true
  Suppress = false
  TaperInnerAngle = 0
  TaperInnerAngleRev = 0
  TreeRank = 0
  Type = 0
  ValidateShape = true
  _ProfileBasedVersion = 1
  _Version = 0
FEATURE [PartDesign::Fillet] Fillet015
  AddSubType = 0
  Base = -> Pocket019 [Edge97,Edge79,Edge85,Edge91]
  BaseFeature = -> Pocket019
  InvalidShape = false
  NewSolid = false
  Radius = 0.5
  Refine = true
  SupportTransform = false
  Suppress = false
  TreeRank = 0
  ValidateShape = true
FEATURE [PartDesign::Body] Body025  label="BodyPartSide"
  AutoGroupSolids = false
  ClaimAllChildren = false
  ExportMode = 0
  Group = -> [Sketch045,DatumPlane004,Pad028,Mirrored,Sketch046,Hole,MultiTransform002,Mirrored001,Mirrored002,Sketch047,Pocket018,MultiTransform003,Chamfer008,Mirrored003,Mirrored004,Sketch048,Pocket019,Fillet015]
  InvalidShape = false
  Origin = -> Origin038
  SingleSolid = true
  Tip = -> Fillet015
  TreeRank = 0
  ValidateShape = true
  _ExportChildren = -> [DatumPlane004,Pad028,Mirrored,Hole,MultiTransform002,Pocket018,MultiTransform003,Chamfer008,Pocket019,Fillet015]
  _GroupVersion = 1
FEATURE [App::Part] Part006  label="PartSideModule"
  ClaimAllChildren = false
  ExportMode = 1
  Group = -> [Body025]
  Origin = -> Origin037
  TreeRank = 0
  _ExportChildren = -> [Body025]
  _GroupVersion = 1
FEATURE [Part::Part2DObjectPython] ShapeString  # Draft 2D object (typed FeaturePython)
  FontFile = <userpath>/Downloads/baveuse/baveuse.ttf
  InvalidShape = false
  Placement = pos=(-35.5,-8,-3) rot=(1,0,0;1.5708rad)
  Size = 5
  String = KARIBOUS
  Tracking = 0
  TreeRank = 0
  ValidateShape = true
FEATURE [Sketcher::SketchObject] Sketch
  ArcFitTolerance = 0
  AttachmentSupport = -> [XZ_Plane]
  ExternalBSplineMaxDegree = 0
  ExternalBSplineTolerance = 0
  FullyConstrained = true
  InternalTolerance = 1e-06
  InvalidShape = false
  MakeInternals = false
  MapMode = 5
  Placement = pos=(0,0,0) rot=(1,0,0;1.5708rad)
  Support = -> [XZ_Plane]
  TreeRank = 0
  ValidateShape = true
  sketch-geometry (4):
    g0: LineSegment StartX=-40 StartY=11 StartZ=0 EndX=40 EndY=11 EndZ=0
    g1: LineSegment StartX=40 StartY=11 StartZ=0 EndX=40 EndY=-7 EndZ=0
    g2: LineSegment StartX=40 StartY=-7 StartZ=0 EndX=-40 EndY=-7 EndZ=0
    g3: LineSegment StartX=-40 StartY=-7 StartZ=0 EndX=-40 EndY=11 EndZ=0
  constraints (11):
    c: Coincident(g0,g1)
    c: Coincident(g1,g2)
    c: Coincident(g2,g3)
    c: Coincident(g3,g0)
    c: Horizontal(g0)
    c: Vertical(g1)
    c: Vertical(g3)
    c: Symmetric(g1,g2,g-2)
    c: DistanceY(g0) = 11
    c: DistanceY(g1,g-1) = 7
    c: DistanceX(g0,g0) = 80
FEATURE [PartDesign::Pad] Pad
  AddSubType = 0
  AutoTaperInnerAngle = false
  CheckUpToFaceLimits = true
  ClaimChildren = false
  Direction = (1,1,1)
  Fit = 0
  FitJoin = 0
  InnerFit = 0
  InnerFitJoin = 0
  InvalidShape = false
  Length = 8
  Length2 = 100
  Linearize = true
  NewSolid = false
  Placement = pos=(0,0,0) rot=(1,0,0;1.5708rad)
  Profile = -> Sketch
  Refine = true
  Suppress = false
  TaperInnerAngle = 0
  TaperInnerAngleRev = 0
  TreeRank = 0
  Type = 0
  ValidateShape = true
  _ProfileBasedVersion = 1
FEATURE [Sketcher::SketchObject] Sketch001
  ArcFitTolerance = 0
  AttachmentSupport = -> [Pad]
  ExternalBSplineMaxDegree = 0
  ExternalBSplineTolerance = 0
  ExternalGeometry = -> [Pad]
  FullyConstrained = true
  InternalTolerance = 1e-06
  InvalidShape = false
  MakeInternals = false
  MapMode = 5
  Placement = pos=(40,0,0) rot=(0.707107,0,0.707107;3.14159rad)
  Support = -> [Pad]
  TreeRank = 0
  ValidateShape = true
  sketch-geometry (4):
    g0: Circle CenterX=-2.5 CenterY=4 CenterZ=0 NormalX=0 NormalY=0 NormalZ=1 AngleXU=0 Radius=2.05
    g1: Circle CenterX=6.5 CenterY=4 CenterZ=0 NormalX=0 NormalY=0 NormalZ=1 AngleXU=0 Radius=2.05
    g2: LineSegment [constr] StartX=-7 StartY=4 StartZ=0 EndX=11 EndY=4 EndZ=0
    g3: LineSegment [constr] StartX=2 StartY=8 StartZ=0 EndX=2 EndY=0 EndZ=0
  constraints (10):
    c: Horizontal(g1,g0)
    c: PointOnObject(g2,g-5)
    c: Horizontal(g2)
    c: PointOnObject(g3,g-1)
    c: Symmetric(g-4,g-4,g2)
    c: Symmetric(g-4,g-5,g3)
    c: Equal(g0,g1)
    c: Symmetric(g0,g1,g3)
    c: Diameter(g1) = 4.1
    c: Symmetric(g-5,g3,g0)
FEATURE [PartDesign::Pocket] Pocket
  AddSubType = 1
  AutoTaperInnerAngle = false
  BaseFeature = -> Pad
  CheckUpToFaceLimits = true
  ClaimChildren = false
  Fit = 0
  FitJoin = 0
  InnerFit = 0
  InnerFitJoin = 0
  InvalidShape = false
  Length = 12
  Length2 = 100
  Linearize = true
  NewSolid = false
  Placement = pos=(0,0,0) rot=(1,0,0;1.5708rad)
  Profile = -> Sketch001
  Refine = true
  Suppress = false
  TaperInnerAngle = 0
  TaperInnerAngleRev = 0
  TreeRank = 0
  Type = 0
  ValidateShape = true
  _ProfileBasedVersion = 1
  _Version = 1
FEATURE [PartDesign::Mirrored] Mirrored005
  AddSubType = 0
  BaseFeature = -> Pocket
  CopyShape = false
  InvalidShape = false
  MirrorPlane = -> YZ_Plane
  NewSolid = false
  OriginalSubs = -> [Pocket]
  Originals = -> [Pocket]
  ParallelTransform = true
  Placement = pos=(0,0,0) rot=(1,0,0;1.5708rad)
  Refine = true
  SubTransform = true
  Suppress = false
  TreeRank = 0
  ValidateShape = true
  _Version = 3
FEATURE [PartDesign::Chamfer] Chamfer
  AddSubType = 0
  Angle = 45
  Base = -> Mirrored005 [Edge9,Edge8,Edge13,Edge14]
  BaseFeature = -> Mirrored005
  ChamferType = 0
  FlipDirection = false
  InvalidShape = false
  NewSolid = false
  Placement = pos=(0,0,0) rot=(1,0,0;1.5708rad)
  Refine = true
  Size = 0.4
  Size2 = 1
  SupportTransform = false
  Suppress = false
  TreeRank = 0
  ValidateShape = true
FEATURE [PartDesign::Chamfer] Chamfer001
  AddSubType = 0
  Angle = 45
  Base = -> Chamfer [Edge11,Edge10,Edge12]
  BaseFeature = -> Chamfer
  ChamferType = 0
  FlipDirection = false
  InvalidShape = false
  NewSolid = false
  Placement = pos=(0,0,0) rot=(1,0,0;1.5708rad)
  Refine = true
  Size = 0.4
  Size2 = 1
  SupportTransform = false
  Suppress = false
  TreeRank = 0
  ValidateShape = true
FEATURE [PartDesign::Fillet] Fillet
  AddSubType = 0
  Base = -> Chamfer001 [Edge20]
  BaseFeature = -> Chamfer001
  InvalidShape = false
  NewSolid = false
  Placement = pos=(0,0,0) rot=(1,0,0;1.5708rad)
  Radius = 2
  Refine = true
  SupportTransform = false
  Suppress = false
  TreeRank = 0
  ValidateShape = true
FEATURE [PartDesign::Pocket] Pocket001
  AddSubType = 1
  AutoTaperInnerAngle = false
  BaseFeature = -> Fillet
  CheckUpToFaceLimits = true
  ClaimChildren = false
  Fit = 0
  FitJoin = 0
  InnerFit = 0
  InnerFitJoin = 0
  InvalidShape = false
  Length = 0.5
  Length2 = 100
  Linearize = true
  NewSolid = false
  Placement = pos=(0,0,0) rot=(1,0,0;1.5708rad)
  Profile = -> ShapeString
  Refine = true
  Suppress = false
  TaperInnerAngle = 0
  TaperInnerAngleRev = 0
  TreeRank = 0
  Type = 0
  ValidateShape = true
  _ProfileBasedVersion = 1
  _Version = 1
FEATURE [PartDesign::Body] Body  label="Front"
  AutoGroupSolids = false
  ClaimAllChildren = false
  ExportMode = 0
  Group = -> [Sketch,Pad,Sketch001,Pocket,Mirrored005,Chamfer,Chamfer001,Fillet,ShapeString,Pocket001]
  InvalidShape = false
  Origin = -> Origin
  Placement = pos=(-6.99382e-06,40,0) rot=(0,0,1;3.14159rad)
  SingleSolid = true
  Tip = -> Pocket001
  TreeRank = 0
  ValidateShape = true
  _ExportChildren = -> [Pad,Pocket,Mirrored005,Chamfer,Chamfer001,Fillet,Pocket001]
  _GroupVersion = 1
FEATURE [Sketcher::SketchObject] Sketch058
  ArcFitTolerance = 0
  AttachmentSupport = -> [YZ_Plane034]
  ExternalBSplineMaxDegree = 0
  ExternalBSplineTolerance = 0
  FullyConstrained = true
  InternalTolerance = 1e-06
  InvalidShape = false
  MakeInternals = false
  MapMode = 5
  Placement = pos=(0,0,0) rot=(0.57735,0.57735,0.57735;2.0944rad)
  Support = -> [YZ_Plane034]
  TreeRank = 0
  ValidateShape = true
  sketch-geometry (10):
    g0: LineSegment StartX=-8 StartY=-7 StartZ=0 EndX=-8 EndY=11 EndZ=0
    g1: LineSegment StartX=-8 StartY=11 StartZ=0 EndX=0 EndY=11 EndZ=0
    g2: LineSegment StartX=0 StartY=11 StartZ=0 EndX=47 EndY=7 EndZ=0
    g3: LineSegment StartX=47 StartY=7 StartZ=0 EndX=47 EndY=-7 EndZ=0
    g4: LineSegment StartX=47 StartY=-7 StartZ=0 EndX=-8 EndY=-7 EndZ=0
    g5: Circle CenterX=40 CenterY=0 CenterZ=0 NormalX=0 NormalY=0 NormalZ=1 AngleXU=0 Radius=4
    g6: Circle CenterX=-4 CenterY=6.5 CenterZ=0 NormalX=0 NormalY=0 NormalZ=1 AngleXU=0 Radius=1.6
    g7: Circle CenterX=-4 CenterY=-2.5 CenterZ=0 NormalX=0 NormalY=0 NormalZ=1 AngleXU=0 Radius=1.6
    g8: LineSegment [constr] StartX=-4 StartY=11 StartZ=0 EndX=-4 EndY=-7 EndZ=0
    g9: LineSegment [constr] StartX=-8 StartY=2 StartZ=0 EndX=0 EndY=2 EndZ=0
  constraints (27):
    c: Vertical(g0)
    c: Coincident(g0,g1)
    c: PointOnObject(g1,g-2)
    c: Horizontal(g1)
    c: Coincident(g1,g2)
    c: Coincident(g2,g3)
    c: Coincident(g3,g4)
    c: Coincident(g4,g0)
    c: Horizontal(g4)
    c: DistanceY(g0) = -7
    c: DistanceY(g0) = 11
    c: PointOnObject(g5,g-1)
    c: DistanceX(g5) = 40
    c: Symmetric(g2,g3,g-1)
    c: Diameter(g5) = 8
    c: DistanceX(g2) = 47
    c: DistanceX(g1,g1) = 8
    c: Vertical(g7,g6)
    c: PointOnObject(g8,g4)
    c: Vertical(g8)
    c: PointOnObject(g9,g-2)
    c: Symmetric(g0,g0,g9)
    c: Symmetric(g0,g1,g8)
    c: Symmetric(g6,g7,g9)
    c: Diameter(g6) = 3.2
    c: Equal(g6,g7)
    c: Symmetric(g9,g1,g6)
FEATURE [PartDesign::Pad] Pad032
  AddSubType = 0
  AutoTaperInnerAngle = false
  CheckUpToFaceLimits = true
  ClaimChildren = false
  Direction = (1,1,1)
  Fit = 0
  FitJoin = 0
  InnerFit = 0
  InnerFitJoin = 0
  InvalidShape = false
  Length = 3
  Length2 = 100
  Linearize = true
  NewSolid = false
  Placement = pos=(0,0,0) rot=(0.57735,0.57735,0.57735;2.0944rad)
  Profile = -> Sketch058
  Refine = true
  Suppress = false
  TaperInnerAngle = 0
  TaperInnerAngleRev = 0
  TreeRank = 0
  Type = 0
  ValidateShape = true
  _ProfileBasedVersion = 1
FEATURE [PartDesign::Fillet] Fillet017
  AddSubType = 0
  Base = -> Pad032 [Edge2]
  BaseFeature = -> Pad032
  InvalidShape = false
  NewSolid = false
  Placement = pos=(0,0,0) rot=(0.57735,0.57735,0.57735;2.0944rad)
  Radius = 2
  Refine = true
  SupportTransform = false
  Suppress = false
  TreeRank = 0
  ValidateShape = true
FEATURE [PartDesign::Fillet] Fillet020
  AddSubType = 0
  Base = -> Fillet017 [Edge24,Edge15]
  BaseFeature = -> Fillet017
  InvalidShape = false
  NewSolid = false
  Placement = pos=(0,0,0) rot=(0.57735,0.57735,0.57735;2.0944rad)
  Radius = 7.1
  Refine = true
  SupportTransform = false
  Suppress = false
  TreeRank = 0
  ValidateShape = true
FEATURE [PartDesign::Chamfer] Chamfer016
  AddSubType = 0
  Angle = 45
  Base = -> Fillet020 [Edge13]
  BaseFeature = -> Fillet020
  ChamferType = 0
  FlipDirection = false
  InvalidShape = false
  NewSolid = false
  Placement = pos=(0,0,0) rot=(0.57735,0.57735,0.57735;2.0944rad)
  Refine = true
  Size = 0.4
  Size2 = 1
  SupportTransform = false
  Suppress = false
  TreeRank = 0
  ValidateShape = true
FEATURE [PartDesign::Body] Body027  label="Lateral"
  AutoGroupSolids = false
  ClaimAllChildren = false
  ExportMode = 0
  Group = -> [Sketch058,Pad032,Fillet017,Fillet020,Chamfer016]
  InvalidShape = false
  Origin = -> Origin044
  Placement = pos=(-40,40,0) rot=(0,0,1;3.14159rad)
  SingleSolid = true
  Tip = -> Chamfer016
  TreeRank = 0
  ValidateShape = true
  _ExportChildren = -> [Pad032,Fillet017,Fillet020,Chamfer016]
  _GroupVersion = 1
FEATURE [Sketcher::SketchObject] Sketch059
  ArcFitTolerance = 0
  AttachmentSupport = -> [YZ_Plane035]
  ExternalBSplineMaxDegree = 0
  ExternalBSplineTolerance = 0
  FullyConstrained = true
  InternalTolerance = 1e-06
  InvalidShape = false
  MakeInternals = false
  MapMode = 5
  Placement = pos=(0,0,0) rot=(0.57735,0.57735,0.57735;2.0944rad)
  Support = -> [YZ_Plane035]
  TreeRank = 0
  ValidateShape = true
  sketch-geometry (10):
    g0: LineSegment StartX=-8 StartY=-7 StartZ=0 EndX=-8 EndY=11 EndZ=0
    g1: LineSegment StartX=-8 StartY=11 StartZ=0 EndX=0 EndY=11 EndZ=0
    g2: LineSegment StartX=0 StartY=11 StartZ=0 EndX=47 EndY=7 EndZ=0
    g3: LineSegment StartX=47 StartY=7 StartZ=0 EndX=47 EndY=-7 EndZ=0
    g4: LineSegment StartX=47 StartY=-7 StartZ=0 EndX=-8 EndY=-7 EndZ=0
    g5: Circle CenterX=40 CenterY=0 CenterZ=0 NormalX=0 NormalY=0 NormalZ=1 AngleXU=0 Radius=1.7
    g6: Circle CenterX=-4 CenterY=6.5 CenterZ=0 NormalX=0 NormalY=0 NormalZ=1 AngleXU=0 Radius=1.6
    g7: Circle CenterX=-4 CenterY=-2.5 CenterZ=0 NormalX=0 NormalY=0 NormalZ=1 AngleXU=0 Radius=1.6
    g8: LineSegment [constr] StartX=-4 StartY=11 StartZ=0 EndX=-4 EndY=-7 EndZ=0
    g9: LineSegment [constr] StartX=-8 StartY=2 StartZ=0 EndX=0 EndY=2 EndZ=0
  constraints (27):
    c: Vertical(g0)
    c: Coincident(g0,g1)
    c: PointOnObject(g1,g-2)
    c: Horizontal(g1)
    c: Coincident(g1,g2)
    c: Coincident(g2,g3)
    c: Coincident(g3,g4)
    c: Coincident(g4,g0)
    c: Horizontal(g4)
    c: DistanceY(g0) = -7
    c: DistanceY(g0) = 11
    c: PointOnObject(g5,g-1)
    c: DistanceX(g5) = 40
    c: Symmetric(g2,g3,g-1)
    c: Diameter(g5) = 3.4
    c: DistanceX(g2) = 47
    c: DistanceX(g1,g1) = 8
    c: Vertical(g7,g6)
    c: PointOnObject(g8,g4)
    c: Vertical(g8)
    c: PointOnObject(g9,g-2)
    c: Symmetric(g0,g0,g9)
    c: Symmetric(g0,g1,g8)
    c: Symmetric(g6,g7,g9)
    c: Diameter(g6) = 3.2
    c: Equal(g6,g7)
    c: Symmetric(g9,g1,g6)
FEATURE [PartDesign::Pad] Pad033
  AddSubType = 0
  AutoTaperInnerAngle = false
  CheckUpToFaceLimits = true
  ClaimChildren = false
  Direction = (1,1,1)
  Fit = 0
  FitJoin = 0
  InnerFit = 0
  InnerFitJoin = 0
  InvalidShape = false
  Length = 3
  Length2 = 100
  Linearize = true
  NewSolid = false
  Placement = pos=(0,0,0) rot=(0.57735,0.57735,0.57735;2.0944rad)
  Profile = -> Sketch059
  Refine = true
  Suppress = false
  TaperInnerAngle = 0
  TaperInnerAngleRev = 0
  TreeRank = 0
  Type = 0
  ValidateShape = true
  _ProfileBasedVersion = 1
FEATURE [PartDesign::Fillet] Fillet021
  AddSubType = 0
  Base = -> Pad033 [Edge2]
  BaseFeature = -> Pad033
  InvalidShape = false
  NewSolid = false
  Placement = pos=(0,0,0) rot=(0.57735,0.57735,0.57735;2.0944rad)
  Radius = 2
  Refine = true
  SupportTransform = false
  Suppress = false
  TreeRank = 0
  ValidateShape = true
FEATURE [PartDesign::Fillet] Fillet022
  AddSubType = 0
  Base = -> Fillet021 [Edge24,Edge15]
  BaseFeature = -> Fillet021
  InvalidShape = false
  NewSolid = false
  Placement = pos=(0,0,0) rot=(0.57735,0.57735,0.57735;2.0944rad)
  Radius = 7.1
  Refine = true
  SupportTransform = false
  Suppress = false
  TreeRank = 0
  ValidateShape = true
FEATURE [PartDesign::Chamfer] Chamfer017
  AddSubType = 0
  Angle = 45
  Base = -> Fillet022 [Edge13]
  BaseFeature = -> Fillet022
  ChamferType = 0
  FlipDirection = false
  InvalidShape = false
  NewSolid = false
  Placement = pos=(0,0,0) rot=(0.57735,0.57735,0.57735;2.0944rad)
  Refine = true
  Size = 0.4
  Size2 = 1
  SupportTransform = false
  Suppress = false
  TreeRank = 0
  ValidateShape = true
FEATURE [PartDesign::Body] Body028  label="Lateral001"
  AutoGroupSolids = false
  ClaimAllChildren = false
  ExportMode = 0
  Group = -> [Sketch059,Pad033,Fillet021,Fillet022,Chamfer017]
  InvalidShape = false
  Origin = -> Origin045
  Placement = pos=(-43,40,-8.9e-15) rot=(0,0,1;3.14159rad)
  SingleSolid = true
  Tip = -> Chamfer017
  TreeRank = 0
  ValidateShape = true
  _ExportChildren = -> [Pad033,Fillet021,Fillet022,Chamfer017]
  _GroupVersion = 1
FEATURE [App::Link] Link  label="Link(Lateral)"
  AutoLinkLabel = true
  AutoPlacement = true
  LinkPlacement = pos=(43,40,0) rot=(0,0,1;3.14159rad)
  LinkedObject = -> Body027
  Placement = pos=(43,40,0) rot=(0,0,1;3.14159rad)
  SyncGroupVisibility = false
  TreeRank = 0
  _LinkVersion = 1
FEATURE [App::Link] Link064  label="Link064(Lateral001)"
  AutoLinkLabel = true
  AutoPlacement = true
  LinkPlacement = pos=(46,40,0) rot=(0,0,1;3.14159rad)
  LinkedObject = -> Body028
  Placement = pos=(46,40,0) rot=(0,0,1;3.14159rad)
  SyncGroupVisibility = false
  TreeRank = 0
  _LinkVersion = 1
FEATURE [TechDraw::DrawSVGTemplate] Template
  Height = 210
  Orientation = 1
  TreeRank = 0
  Width = 297
FEATURE [TechDraw::DrawProjGroupItem] ProjItem  label="Front001"
  CoarseView = false
  Direction = (1,0,0)
  Focus = 100
  HardHidden = false
  IsoCount = 0
  IsoHidden = false
  IsoVisible = false
  LockPosition = true
  Perspective = false
  Rotation = 0
  RotationVector = (0,-1,0)
  ScaleType = 2
  SeamHidden = false
  SeamVisible = true
  SmoothHidden = false
  SmoothVisible = true
  Source = -> [Chamfer016]
  TreeRank = 0
  Type = 0
  X = 0
  XDirection = (0,-1,0)
  Y = 0
FEATURE [TechDraw::DrawProjGroup] ProjGroup
  Anchor = -> ProjItem
  AutoDistribute = true
  LockPosition = false
  ProjectionType = 0
  Rotation = 0
  ScaleType = 0
  Source = -> [Chamfer016]
  TreeRank = 0
  Views = -> [ProjItem]
  X = 148.5
  Y = 105
  spacingX = 15
  spacingY = 15
FEATURE [TechDraw::DrawProjGroupItem] ProjItem001  label="Front002"
  CoarseView = false
  Direction = (1,0,0)
  Focus = 100
  HardHidden = false
  IsoCount = 0
  IsoHidden = false
  IsoVisible = false
  LockPosition = true
  Perspective = false
  Rotation = 0
  RotationVector = (0,-1,0)
  ScaleType = 2
  SeamHidden = false
  SeamVisible = true
  SmoothHidden = false
  SmoothVisible = true
  Source = -> [Chamfer017]
  TreeRank = 0
  Type = 0
  X = 0
  XDirection = (0,-1,0)
  Y = 0
FEATURE [TechDraw::DrawProjGroup] ProjGroup001
  Anchor = -> ProjItem001
  AutoDistribute = true
  LockPosition = false
  ProjectionType = 0
  Rotation = 0
  ScaleType = 0
  Source = -> [Chamfer017]
  TreeRank = 0
  Views = -> [ProjItem001]
  X = 148.5
  Y = 84.6454
  spacingX = 15
  spacingY = 15
FEATURE [TechDraw::DrawPage] Page  label="Laser3mmPoignee"
  KeepUpdated = true
  NextBalloonIndex = 1
  ProjectionType = 0
  Template = -> Template
  TreeRank = 0
  Views = -> [ProjGroup,ProjGroup001]
FEATURE [Part::FeaturePython] Screw  label="M3x12-Screw"  # Fasteners workbench fastener (typed FeaturePython)
  InvalidShape = false
  Placement = pos=(-46,44,6.5) rot=(0,-1,0;1.5708rad)
  TreeRank = 0
  ValidateShape = true
  baseObject = -> Body028 [Edge36]
  diameter = 1
  invert = false
  leftHanded = false
  length = 3
  lengthCustom = 12
  matchOuter = false
  offset = 0
  thread = false
  type = 40
FEATURE [Part::FeaturePython] Screw001  label="M3x12-Screw020"  # Fasteners workbench fastener (typed FeaturePython)
  InvalidShape = false
  Placement = pos=(-46,44,-2.5) rot=(0,-1,0;1.5708rad)
  TreeRank = 0
  ValidateShape = true
  baseObject = -> Body028 [Edge34]
  diameter = 1
  invert = false
  leftHanded = false
  length = 3
  lengthCustom = 12
  matchOuter = false
  offset = 0
  thread = false
  type = 40
FEATURE [Part::FeaturePython] Screw002  label="M3x12-Screw018"  # Fasteners workbench fastener (typed FeaturePython)
  InvalidShape = false
  Placement = pos=(46,44,6.5) rot=(0.707107,0,0.707107;3.14159rad)
  TreeRank = 0
  ValidateShape = true
  diameter = 1
  invert = false
  leftHanded = false
  length = 3
  lengthCustom = 12
  matchOuter = false
  offset = 0
  thread = false
  type = 40
FEATURE [Part::FeaturePython] Screw003  label="M3x12-Screw019"  # Fasteners workbench fastener (typed FeaturePython)
  InvalidShape = false
  Placement = pos=(46,44,-2.5) rot=(0.707107,0,0.707107;3.14159rad)
  TreeRank = 0
  ValidateShape = true
  diameter = 1
  invert = false
  leftHanded = false
  length = 3
  lengthCustom = 12
  matchOuter = false
  offset = 0
  thread = false
  type = 40
FEATURE [App::DocumentObjectGroup] Group001  label="Visserie"
  ClaimAllChildren = true
  ExportMode = 1
  Group = -> [Screw,Screw001,Screw002,Screw003]
  TreeRank = 0
  _GroupVersion = 1
FEATURE [App::Part] Part  label="Poignee"
  ClaimAllChildren = false
  ExportMode = 1
  Group = -> [Body,Body027,Body028,Link,Link064,Screw,Screw001,Screw002,Screw003,Group001]
  Origin = -> Origin043
  TreeRank = 0
  _ExportChildren = -> [Body,Body027,Body028,Link,Link064,Group001]
  _GroupVersion = 1
FEATURE [Sketcher::SketchObject] Sketch060
  ArcFitTolerance = 0
  AttachmentSupport = -> [XY_Plane037]
  ExternalBSplineMaxDegree = 0
  ExternalBSplineTolerance = 0
  FullyConstrained = true
  InternalTolerance = 1e-06
  InvalidShape = false
  MakeInternals = false
  MapMode = 5
  Support = -> [XY_Plane037]
  TreeRank = 0
  ValidateShape = true
  sketch-geometry (10):
    g0: LineSegment [constr] StartX=0 StartY=0 StartZ=0 EndX=34.641 EndY=-20 EndZ=0
    g1: LineSegment [constr] StartX=0 StartY=0 StartZ=0 EndX=-34.641 EndY=-20 EndZ=0
    g2: LineSegment [constr] StartX=-34.641 StartY=-20 StartZ=0 EndX=-14.641 EndY=-54.641 EndZ=0
    g3: LineSegment [constr] StartX=34.641 StartY=-20 StartZ=0 EndX=14.641 EndY=-54.641 EndZ=0
    g4: LineSegment StartX=-14.641 StartY=-54.641 StartZ=0 EndX=-23.3013 EndY=-59.641 EndZ=0
    g5: LineSegment StartX=14.641 StartY=-54.641 StartZ=0 EndX=23.3013 EndY=-59.641 EndZ=0
    g6: LineSegment StartX=-23.3013 StartY=-59.641 StartZ=0 EndX=-15 EndY=-89.641 EndZ=0
    g7: LineSegment StartX=23.3013 StartY=-59.641 StartZ=0 EndX=15 EndY=-89.641 EndZ=0
    g8: LineSegment StartX=-14.641 StartY=-54.641 StartZ=0 EndX=14.641 EndY=-54.641 EndZ=0
    g9: LineSegment StartX=-15 StartY=-89.641 StartZ=0 EndX=15 EndY=-89.641 EndZ=0
  constraints (24):
    c: Coincident(g0,g-1)
    c: Coincident(g1,g0)
    c: Symmetric(g0,g1,g-2)
    c: Angle(g1,g0) = 2.0944
    c: Coincident(g2,g1)
    c: Perpendicular(g1,g2)
    c: Coincident(g3,g0)
    c: Symmetric(g3,g2,g-2)
    c: Distance(g2) = 40
    c: Distance(g0) = 40
    c: Coincident(g4,g2)
    c: Coincident(g5,g3)
    c: Perpendicular(g3,g5)
    c: Symmetric(g4,g5,g-2)
    c: Distance(g5) = 10
    c: Coincident(g6,g4)
    c: Coincident(g7,g5)
    c: Symmetric(g7,g6,g-2)
    c: DistanceY(g7,g3) = 35
    c: Coincident(g8,g4)
    c: Coincident(g8,g5)
    c: Coincident(g9,g6)
    c: Coincident(g9,g7)
    c: DistanceX(g9,g9) = 30
FEATURE [PartDesign::Pad] Pad034
  AddSubType = 0
  AutoTaperInnerAngle = false
  CheckUpToFaceLimits = true
  ClaimChildren = false
  Direction = (1,1,1)
  Fit = 0
  FitJoin = 0
  InnerFit = 0
  InnerFitJoin = 0
  InvalidShape = false
  Length = 50
  Length2 = 100
  Linearize = true
  NewSolid = false
  Profile = -> Sketch060
  Refine = true
  Suppress = false
  TaperInnerAngle = 0
  TaperInnerAngleRev = 0
  TreeRank = 0
  Type = 0
  ValidateShape = true
  _ProfileBasedVersion = 1
FEATURE [Sketcher::SketchObject] Sketch061
  ArcFitTolerance = 0
  AttachmentSupport = -> [YZ_Plane037]
  ExternalBSplineMaxDegree = 0
  ExternalBSplineTolerance = 0
  ExternalGeometry = -> [Pad034]
  FullyConstrained = true
  InternalTolerance = 1e-06
  InvalidShape = false
  MakeInternals = false
  MapMode = 5
  Placement = pos=(0,0,0) rot=(0.57735,0.57735,0.57735;2.0944rad)
  Support = -> [YZ_Plane037]
  TreeRank = 0
  ValidateShape = true
  sketch-geometry (4):
    g0: LineSegment StartX=-62.641 StartY=0 StartZ=0 EndX=-89.641 EndY=20.6315 EndZ=0
    g1: LineSegment StartX=-62.641 StartY=0 StartZ=0 EndX=-89.641 EndY=0 EndZ=0
    g2: LineSegment StartX=-89.641 StartY=0 StartZ=0 EndX=-89.641 EndY=20.6315 EndZ=0
    g3: LineSegment [constr] StartX=-89.641 StartY=20.6315 StartZ=0 EndX=-54.641 EndY=50 EndZ=0
  constraints (11):
    c: PointOnObject(g0,g-4)
    c: PointOnObject(g0,g-1)
    c: DistanceX(g0,g-3) = 3
    c: Coincident(g0,g1)
    c: PointOnObject(g1,g-4)
    c: Horizontal(g1)
    c: Coincident(g1,g2)
    c: Coincident(g2,g0)
    c: Coincident(g3,g0)
    c: Coincident(g3,g-5)
    c: Angle(g-4,g3) = 2.26893
FEATURE [PartDesign::Pocket] Pocket025
  AddSubType = 1
  AutoTaperInnerAngle = false
  BaseFeature = -> Pad034
  CheckUpToFaceLimits = true
  ClaimChildren = false
  Fit = 0
  FitJoin = 0
  InnerFit = 0
  InnerFitJoin = 0
  InvalidShape = false
  Length = 5
  Length2 = 100
  Linearize = true
  Midplane = true
  NewSolid = false
  Profile = -> Sketch061
  Refine = true
  Suppress = false
  TaperInnerAngle = 0
  TaperInnerAngleRev = 0
  TreeRank = 0
  Type = 1
  ValidateShape = true
  _ProfileBasedVersion = 1
  _Version = 1
FEATURE [Sketcher::SketchObject] Sketch062
  ArcFitTolerance = 0
  AttachmentSupport = -> [YZ_Plane037]
  ExternalBSplineMaxDegree = 0
  ExternalBSplineTolerance = 0
  ExternalGeometry = -> [Pocket025]
  FullyConstrained = true
  InternalTolerance = 1e-06
  InvalidShape = false
  MakeInternals = false
  MapMode = 5
  Placement = pos=(0,0,0) rot=(0.57735,0.57735,0.57735;2.0944rad)
  Support = -> [YZ_Plane037]
  TreeRank = 0
  ValidateShape = true
  sketch-geometry (3):
    g0: LineSegment StartX=-89.641 StartY=50 StartZ=0 EndX=-89.641 EndY=20.6315 EndZ=0
    g1: LineSegment StartX=-89.641 StartY=20.6315 StartZ=0 EndX=-54.641 EndY=50 EndZ=0
    g2: LineSegment StartX=-89.641 StartY=50 StartZ=0 EndX=-54.641 EndY=50 EndZ=0
  constraints (6):
    c: Coincident(g1,g0)
    c: Coincident(g-3,g0)
    c: Coincident(g-3,g0)
    c: Coincident(g2,g0)
    c: Coincident(g2,g1)
    c: Coincident(g1,g-5)
FEATURE [PartDesign::Pocket] Pocket026
  AddSubType = 1
  AutoTaperInnerAngle = false
  BaseFeature = -> Pocket025
  CheckUpToFaceLimits = true
  ClaimChildren = false
  Fit = 0
  FitJoin = 0
  InnerFit = 0
  InnerFitJoin = 0
  InvalidShape = false
  Length = 5
  Length2 = 100
  Linearize = true
  Midplane = true
  NewSolid = false
  Profile = -> Sketch062
  Refine = true
  Suppress = false
  TaperInnerAngle = 0
  TaperInnerAngleRev = 0
  TreeRank = 0
  Type = 1
  ValidateShape = true
  _ProfileBasedVersion = 1
  _Version = 1
FEATURE [PartDesign::Plane] DatumPlane
  AttachmentOffset = pos=(0,0,-30) rot=(0,0,1;0rad)
  AttachmentSupport = -> [Pocket026]
  InvalidShape = false
  Length = 67.9904
  MapMode = 5
  MinimumLength = 10
  MinimumWidth = 10
  Placement = pos=(-35,-60.6218,3.3e-15) rot=(0.186157,0.694747,0.694747;2.77349rad)
  ResizeMode = 0
  Support = -> [Pocket026]
  TreeRank = 0
  ValidateShape = true
  Width = 50
FEATURE [Sketcher::SketchObject] Sketch063
  ArcFitTolerance = 0
  AttachmentSupport = -> [DatumPlane]
  ExternalBSplineMaxDegree = 0
  ExternalBSplineTolerance = 0
  ExternalGeometry = -> [Pocket026]
  FullyConstrained = true
  InternalTolerance = 1e-06
  InvalidShape = false
  MakeInternals = false
  MapMode = 5
  Placement = pos=(-35,-60.6218,3.3e-15) rot=(0.186157,0.694747,0.694747;2.77349rad)
  Support = -> [DatumPlane]
  TreeRank = 0
  ValidateShape = true
  sketch-geometry (2):
    g0: Circle CenterX=-45 CenterY=10 CenterZ=0 NormalX=0 NormalY=0 NormalZ=1 AngleXU=0 Radius=1.6
    g1: LineSegment [constr] StartX=-50 StartY=10 StartZ=0 EndX=-40 EndY=10 EndZ=0
  constraints (6):
    c: PointOnObject(g1,g-3)
    c: PointOnObject(g1,g-4)
    c: Horizontal(g1)
    c: Symmetric(g1,g1,g0)
    c: Diameter(g0) = 3.2
    c: Distance(g-3,g1) = 10
FEATURE [PartDesign::Hole] Hole001
  AddSubType = 1
  BaseFeature = -> Pocket026
  ClaimChildren = false
  CustomThreadClearance = 0
  Depth = 39
  DepthType = 0
  Diameter = 3.2
  DrillForDepth = false
  DrillPoint = 1
  DrillPointAngle = 118
  Fit = 0
  FitJoin = 0
  HoleCutCountersinkAngle = 90
  HoleCutCustomValues = true
  HoleCutDepth = 27
  HoleCutDiameter = 8
  HoleCutType = 1
  InnerFit = 0
  InnerFitJoin = 0
  InvalidShape = false
  ModelThread = false
  NewSolid = false
  Profile = -> Sketch063
  Refine = true
  Reversed = true
  Suppress = false
  Tapered = false
  TaperedAngle = 90
  ThreadClass = 0
  ThreadDepth = 39
  ThreadDepthType = 0
  ThreadDirection = 0
  ThreadFit = 0
  ThreadSize = 0
  ThreadType = 0
  Threaded = false
  TreeRank = 0
  UseCustomThreadClearance = false
  ValidateShape = true
  _ProfileBasedVersion = 1
FEATURE [PartDesign::Mirrored] Mirrored006
  AddSubType = 0
  BaseFeature = -> Hole001
  CopyShape = false
  InvalidShape = false
  MirrorPlane = -> YZ_Plane037
  NewSolid = false
  OriginalSubs = -> [Hole001]
  Originals = -> [Hole001]
  ParallelTransform = true
  Refine = true
  SubTransform = true
  Suppress = false
  TreeRank = 0
  ValidateShape = true
  _Version = 3
FEATURE [Sketcher::SketchObject] Sketch064
  ArcFitTolerance = 0
  AttachmentSupport = -> [Mirrored006]
  ExternalBSplineMaxDegree = 0
  ExternalBSplineTolerance = 0
  ExternalGeometry = -> [Mirrored006]
  FullyConstrained = true
  InternalTolerance = 1e-06
  InvalidShape = false
  MakeInternals = false
  MapMode = 5
  Placement = pos=(-2.64e-14,-47.1965,56.2467) rot=(1,0,0;0.698132rad)
  Support = -> [Mirrored006]
  TreeRank = 0
  ValidateShape = true
  sketch-geometry (2):
    g0: Circle CenterX=-14 CenterY=-14.7181 CenterZ=0 NormalX=0 NormalY=0 NormalZ=1 AngleXU=0 Radius=2.05
    g1: Circle CenterX=14 CenterY=-14.7181 CenterZ=0 NormalX=0 NormalY=0 NormalZ=1 AngleXU=0 Radius=2.05
  constraints (5):
    c: Symmetric(g1,g0,g-2)
    c: Diameter(g0) = 4.1
    c: Equal(g0,g1)
    c: DistanceX(g0,g1) = 28
    c: DistanceY(g0,g-3) = 5
FEATURE [PartDesign::Pocket] Pocket027
  AddSubType = 1
  AutoTaperInnerAngle = false
  BaseFeature = -> Mirrored006
  CheckUpToFaceLimits = true
  ClaimChildren = false
  Fit = 0
  FitJoin = 0
  InnerFit = 0
  InnerFitJoin = 0
  InvalidShape = false
  Length = 5
  Length2 = 100
  Linearize = true
  NewSolid = false
  Profile = -> Sketch064
  Refine = true
  Suppress = false
  TaperInnerAngle = 0
  TaperInnerAngleRev = 0
  TreeRank = 0
  Type = 1
  ValidateShape = true
  _ProfileBasedVersion = 1
  _Version = 1
FEATURE [Sketcher::SketchObject] Sketch065
  ArcFitTolerance = 0
  AttachmentSupport = -> [Pocket027]
  ExternalBSplineMaxDegree = 0
  ExternalBSplineTolerance = 0
  ExternalGeometry = -> [Pocket027]
  FullyConstrained = true
  InternalTolerance = 1e-06
  InvalidShape = false
  MakeInternals = false
  MapMode = 5
  Placement = pos=(-2.64e-14,-47.1965,56.2467) rot=(1,0,0;0.698132rad)
  Support = -> [Pocket027]
  TreeRank = 0
  ValidateShape = true
  sketch-geometry (3):
    g0: Circle CenterX=0 CenterY=-32.5627 CenterZ=0 NormalX=0 NormalY=0 NormalZ=1 AngleXU=0 Radius=15
    g1: GeomPoint [constr] X=2e-16 Y=-55.4073 Z=0
    g2: GeomPoint [constr] X=0 Y=-9.71807 Z=0
  constraints (6):
    c: PointOnObject(g0,g-2)
    c: Diameter(g0) = 30
    c: PointOnObject(g2,g-2)
    c: PointOnObject(g2,g-3)
    c: PointOnObject(g1,g-4)
    c: Symmetric(g1,g2,g0)
FEATURE [PartDesign::Pocket] Pocket028
  AddSubType = 1
  AutoTaperInnerAngle = false
  BaseFeature = -> Pocket027
  CheckUpToFaceLimits = true
  ClaimChildren = false
  Fit = 0
  FitJoin = 0
  InnerFit = 0
  InnerFitJoin = 0
  InvalidShape = false
  Length = 17
  Length2 = 100
  Linearize = true
  NewSolid = false
  Profile = -> Sketch065
  Refine = true
  Suppress = false
  TaperInnerAngle = 0
  TaperInnerAngleRev = 0
  TreeRank = 0
  Type = 0
  ValidateShape = true
  _ProfileBasedVersion = 1
  _Version = 1
FEATURE [Sketcher::SketchObject] Sketch066
  ArcFitTolerance = 0
  AttachmentSupport = -> [Pocket028]
  ExternalBSplineMaxDegree = 0
  ExternalBSplineTolerance = 0
  ExternalGeometry = -> [Pocket028]
  FullyConstrained = true
  InternalTolerance = 1e-06
  InvalidShape = false
  MakeInternals = false
  MapMode = 5
  Placement = pos=(-2.64e-14,-47.1965,56.2467) rot=(1,0,0;0.698132rad)
  Support = -> [Pocket028]
  TreeRank = 0
  ValidateShape = true
  sketch-geometry (4):
    g0: ArcOfCircle CenterX=0 CenterY=-32.5627 CenterZ=0 NormalX=0 NormalY=0 NormalZ=1 AngleXU=0 Radius=11.5 StartAngle=3.22982 EndAngle=6.19496
    g1: LineSegment StartX=-11.4553 StartY=-33.576 StartZ=0 EndX=-12.3039 EndY=-23.9828 EndZ=0
    g2: LineSegment StartX=12.3039 StartY=-23.9828 StartZ=0 EndX=11.4553 EndY=-33.576 EndZ=0
    g3: LineSegment StartX=-12.3039 StartY=-23.9828 StartZ=0 EndX=12.3039 EndY=-23.9828 EndZ=0
  constraints (8):
    c: Coincident(g0,g-3)
    c: Diameter(g0) = 23
    c: Coincident(g1,g-4)
    c: Coincident(g2,g-4)
    c: Coincident(g3,g1)
    c: Coincident(g3,g2)
    c: Tangent(g1,g0) = 1.5708
    c: Tangent(g2,g0) = 1.5708
FEATURE [PartDesign::Pocket] Pocket029
  AddSubType = 1
  AutoTaperInnerAngle = false
  BaseFeature = -> Pocket028
  CheckUpToFaceLimits = true
  ClaimChildren = false
  Fit = 0
  FitJoin = 0
  InnerFit = 0
  InnerFitJoin = 0
  InvalidShape = false
  Length = 5
  Length2 = 100
  Linearize = true
  NewSolid = false
  Profile = -> Sketch066
  Refine = true
  Suppress = false
  TaperInnerAngle = 0
  TaperInnerAngleRev = 0
  TreeRank = 0
  Type = 1
  ValidateShape = true
  _ProfileBasedVersion = 1
  _Version = 1
FEATURE [PartDesign::Chamfer] Chamfer018
  AddSubType = 0
  Angle = 45
  Base = -> Pocket029 [Edge44,Edge31]
  BaseFeature = -> Pocket029
  ChamferType = 0
  FlipDirection = false
  InvalidShape = false
  NewSolid = false
  Refine = true
  Size = 0.4
  Size2 = 1
  SupportTransform = false
  Suppress = false
  TreeRank = 0
  ValidateShape = true
FEATURE [App::Link] Link065  label="Link065(CoinStandard)"
  AutoLinkLabel = true
  AutoPlacement = true
  LinkedObject = -> Body029
  SyncGroupVisibility = false
  TreeRank = 0
  _LinkVersion = 1
FEATURE [PartDesign::SubShapeBinder] Binder  label="Binder(Chamfer023)"
  BindCopyOnChange = 0
  BindMode = 0
  ClaimChildren = false
  Context = -> Part010 [Body030.Binder.]
  EdgeTolerance = 1e-06
  FillStyle = 0
  Fuse = false
  InvalidShape = false
  MakeFace = true
  MergeEdges = true
  OffsetFill = false
  OffsetIntersection = false
  OffsetJoinType = 0
  OffsetOpenResult = false
  Outline = false
  PartialLoad = false
  Refine = true
  Relative = true
  SplitEdges = false
  Support = -> [Chamfer023[Face30]]
  TightBound = false
  TreeRank = 0
  ValidateShape = true
  _Version = 8
FEATURE [Sketcher::SketchObject] Sketch067
  ArcFitTolerance = 0
  AttachmentSupport = -> [Binder]
  ExternalBSplineMaxDegree = 0
  ExternalBSplineTolerance = 0
  ExternalGeometry = -> [Binder]
  FullyConstrained = true
  InternalTolerance = 1e-06
  InvalidShape = false
  MakeInternals = false
  MapMode = 5
  Placement = pos=(-2.82e-14,-50.4105,60.0769) rot=(1,0,0;0.698132rad)
  Support = -> [Binder]
  TreeRank = 0
  ValidateShape = true
  sketch-geometry (3):
    g0: Circle CenterX=-2e-16 CenterY=-32.5627 CenterZ=0 NormalX=0 NormalY=0 NormalZ=1 AngleXU=0 Radius=8
    g1: Circle CenterX=14 CenterY=-14.7181 CenterZ=0 NormalX=0 NormalY=0 NormalZ=1 AngleXU=0 Radius=1.6
    g2: Circle CenterX=-14 CenterY=-14.7181 CenterZ=0 NormalX=0 NormalY=0 NormalZ=1 AngleXU=0 Radius=1.6
  constraints (6):
    c: Coincident(g0,g-9)
    c: Diameter(g0) = 16
    c: Coincident(g1,g-10)
    c: Coincident(g2,g-11)
    c: Diameter(g2) = 3.2
    c: Equal(g2,g1)
FEATURE [PartDesign::Pad] Pad035
  AddSubType = 0
  AutoTaperInnerAngle = false
  CheckUpToFaceLimits = true
  ClaimChildren = false
  Direction = (-4e-16,-0.642788,0.766044)
  Fit = 0
  FitJoin = 0
  InnerFit = 0
  InnerFitJoin = 0
  InvalidShape = false
  Length = 3
  Length2 = 100
  Linearize = true
  NewSolid = false
  Profile = -> Sketch067
  Refine = true
  Suppress = false
  TaperInnerAngle = 0
  TaperInnerAngleRev = 0
  TreeRank = 0
  Type = 0
  ValidateShape = true
  _ProfileBasedVersion = 1
FEATURE [PartDesign::Chamfer] Chamfer021
  AddSubType = 0
  Angle = 45
  Base = -> Pad035 [Edge8,Edge11,Edge5,Edge1,Edge14,Edge2]
  BaseFeature = -> Pad035
  ChamferType = 0
  FlipDirection = false
  InvalidShape = false
  NewSolid = false
  Refine = true
  Size = 0.4
  Size2 = 1
  SupportTransform = false
  Suppress = false
  TreeRank = 0
  ValidateShape = true
FEATURE [PartDesign::Body] Body030  label="PlateBAU"
  AutoGroupSolids = false
  ClaimAllChildren = false
  ExportMode = 0
  Group = -> [Binder,Sketch067,Pad035,Chamfer021]
  InvalidShape = false
  Origin = -> Origin048
  SingleSolid = true
  Tip = -> Chamfer021
  TreeRank = 0
  ValidateShape = true
  _ExportChildren = -> [Binder,Pad035,Chamfer021]
  _GroupVersion = 1
FEATURE [TechDraw::DrawSVGTemplate] Template001
  Height = 210
  Orientation = 1
  TreeRank = 0
  Width = 297
FEATURE [TechDraw::DrawProjGroupItem] ProjItem002  label="Front003"
  CoarseView = false
  Direction = (0,-0.643,0.766)
  Focus = 100
  HardHidden = false
  IsoCount = 0
  IsoHidden = false
  IsoVisible = false
  LockPosition = true
  Perspective = false
  Rotation = 0
  RotationVector = (-1,0,0)
  ScaleType = 2
  SeamHidden = false
  SeamVisible = true
  SmoothHidden = false
  SmoothVisible = true
  Source = -> [Chamfer021]
  TreeRank = 0
  Type = 0
  X = 0
  XDirection = (-1,0,0)
  Y = 0
FEATURE [TechDraw::DrawProjGroup] ProjGroup002
  Anchor = -> ProjItem002
  AutoDistribute = true
  LockPosition = false
  ProjectionType = 0
  Rotation = 0
  ScaleType = 0
  Source = -> [Chamfer021]
  TreeRank = 0
  Views = -> [ProjItem002]
  X = 23.7819
  Y = 186.665
  spacingX = 15
  spacingY = 15
FEATURE [TechDraw::DrawPage] Page001  label="Laser3mmPlateBau"
  KeepUpdated = true
  NextBalloonIndex = 1
  ProjectionType = 0
  Template = -> Template001
  TreeRank = 0
  Views = -> [ProjGroup002]
FEATURE [PartDesign::Pad] Pad036
  AddSubType = 0
  AutoTaperInnerAngle = false
  BaseFeature = -> Chamfer018
  CheckUpToFaceLimits = true
  ClaimChildren = false
  Direction = (1,1,1)
  Fit = 0
  FitJoin = 0
  InnerFit = 0
  InnerFitJoin = 0
  InvalidShape = false
  Length = 5
  Length2 = 100
  Linearize = true
  NewSolid = false
  Profile = -> Chamfer018 [Face5]
  Refine = true
  Suppress = false
  TaperInnerAngle = 0
  TaperInnerAngleRev = 0
  TreeRank = 0
  Type = 0
  ValidateShape = true
  _ProfileBasedVersion = 1
FEATURE [PartDesign::Chamfer] Chamfer022
  AddSubType = 0
  Angle = 45
  Base = -> Pad036 [Face15]
  BaseFeature = -> Pad036
  ChamferType = 0
  FlipDirection = false
  InvalidShape = false
  NewSolid = false
  Refine = true
  Size = 0.4
  Size2 = 1
  SupportTransform = false
  Suppress = false
  TreeRank = 0
  ValidateShape = true
FEATURE [PartDesign::Chamfer] Chamfer023
  AddSubType = 0
  Angle = 45
  Base = -> Chamfer022 [Edge64,Edge63]
  BaseFeature = -> Chamfer022
  ChamferType = 0
  FlipDirection = false
  InvalidShape = false
  NewSolid = false
  Refine = true
  Size = 1
  Size2 = 1
  SupportTransform = false
  Suppress = false
  TreeRank = 0
  ValidateShape = true
FEATURE [PartDesign::Body] Body029  label="CoinStandard"
  AutoGroupSolids = false
  ClaimAllChildren = false
  ExportMode = 0
  Group = -> [Sketch060,Pad034,Sketch061,Pocket025,Sketch062,Pocket026,DatumPlane,Sketch063,Hole001,Mirrored006,Sketch064,Pocket027,Sketch065,Pocket028,Sketch066,Pocket029,Chamfer018,Pad036,Chamfer022,Chamfer023]
  InvalidShape = false
  Origin = -> Origin046
  SingleSolid = true
  Tip = -> Chamfer023
  TreeRank = 0
  ValidateShape = true
  _ExportChildren = -> [Pad034,Pocket025,Pocket026,DatumPlane,Hole001,Mirrored006,Pocket027,Pocket028,Pocket029,Chamfer018,Pad036,Chamfer022,Chamfer023]
  _GroupVersion = 1
FEATURE [App::Link] Link066  label="Link066(CoinStandard)"
  AutoLinkLabel = true
  AutoPlacement = true
  LinkedObject = -> Body029
  SyncGroupVisibility = false
  TreeRank = 0
  _LinkVersion = 1
FEATURE [PartDesign::FeatureBase] Clone
  BaseFeature = -> Body030
  InvalidShape = false
  NewSolid = false
  Suppress = false
  TreeRank = 0
  ValidateShape = true
FEATURE [Sketcher::SketchObject] Sketch068
  ArcFitTolerance = 0
  AttachmentSupport = -> [Clone]
  ExternalBSplineMaxDegree = 0
  ExternalBSplineTolerance = 0
  ExternalGeometry = -> [Clone]
  FullyConstrained = true
  InternalTolerance = 1e-06
  InvalidShape = false
  MakeInternals = false
  MapMode = 5
  Placement = pos=(-3.09e-14,-52.3388,62.375) rot=(1,0,0;0.698132rad)
  Support = -> [Clone]
  TreeRank = 0
  ValidateShape = true
  sketch-geometry (2):
    g0: Circle CenterX=0 CenterY=-32.5627 CenterZ=0 NormalX=0 NormalY=0 NormalZ=1 AngleXU=0 Radius=3
    g1: Circle CenterX=0 CenterY=-32.5627 CenterZ=0 NormalX=0 NormalY=0 NormalZ=1 AngleXU=0 Radius=15
  constraints (4):
    c: Coincident(g0,g-3)
    c: Coincident(g1,g0)
    c: Diameter(g1) = 30
    c: Diameter(g0) = 6
FEATURE [PartDesign::Pad] Pad037
  AddSubType = 0
  AutoTaperInnerAngle = false
  BaseFeature = -> Clone
  CheckUpToFaceLimits = true
  ClaimChildren = false
  Direction = (-4e-16,-0.642788,0.766044)
  Fit = 0
  FitJoin = 0
  InnerFit = 0
  InnerFitJoin = 0
  InvalidShape = false
  Length = 10
  Length2 = 100
  Linearize = true
  NewSolid = false
  Profile = -> Sketch068
  Refine = true
  Suppress = false
  TaperInnerAngle = 0
  TaperInnerAngleRev = 0
  TreeRank = 0
  Type = 3
  UpToFace = -> Clone [Face2]
  ValidateShape = true
  _ProfileBasedVersion = 1
FEATURE [PartDesign::Body] Body032  label="PlateTirette_1"
  AutoGroupSolids = false
  BaseFeature = -> Body030
  ClaimAllChildren = false
  ExportMode = 0
  Group = -> [Clone,Sketch068,Pad037]
  InvalidShape = false
  Origin = -> Origin051
  SingleSolid = true
  Tip = -> Pad037
  TreeRank = 0
  ValidateShape = true
  _ExportChildren = -> [Clone,Pad037]
  _GroupVersion = 1
FEATURE [PartDesign::SubShapeBinder] Binder001  label="Binder001(Pad037)"
  BindCopyOnChange = 0
  BindMode = 2
  ClaimChildren = false
  Context = -> Part011 [Body033.Binder001.]
  EdgeTolerance = 1e-06
  FillStyle = 0
  Fuse = false
  InvalidShape = false
  MakeFace = true
  MergeEdges = true
  OffsetFill = false
  OffsetIntersection = false
  OffsetJoinType = 0
  OffsetOpenResult = false
  Outline = false
  PartialLoad = false
  Refine = true
  Relative = true
  SplitEdges = false
  TightBound = false
  TreeRank = 0
  ValidateShape = true
  _Version = 8
FEATURE [PartDesign::Pad] Pad038
  AddSubType = 0
  AutoTaperInnerAngle = false
  CheckUpToFaceLimits = true
  ClaimChildren = false
  Direction = (-4e-16,-0.642788,0.766044)
  Fit = 0
  FitJoin = 0
  InnerFit = 0
  InnerFitJoin = 0
  InvalidShape = false
  Length = 3
  Length2 = 100
  Linearize = true
  NewSolid = false
  Profile = -> Binder001
  Refine = true
  Suppress = false
  TaperInnerAngle = 0
  TaperInnerAngleRev = 0
  TreeRank = 0
  Type = 0
  ValidateShape = true
  _ProfileBasedVersion = 1
FEATURE [Sketcher::SketchObject] Sketch069
  ArcFitTolerance = 0
  AttachmentSupport = -> [Pad038]
  ExternalBSplineMaxDegree = 0
  ExternalBSplineTolerance = 0
  ExternalGeometry = -> [Pad038]
  FullyConstrained = true
  InternalTolerance = 1e-06
  InvalidShape = false
  MakeInternals = false
  MapMode = 5
  Placement = pos=(-3.46e-14,-54.2672,64.6731) rot=(1,0,0;0.698132rad)
  Support = -> [Pad038]
  TreeRank = 0
  ValidateShape = true
  sketch-geometry (1):
    g0: Circle CenterX=0 CenterY=-32.5627 CenterZ=0 NormalX=0 NormalY=0 NormalZ=1 AngleXU=0 Radius=12
  constraints (2):
    c: Coincident(g0,g-3)
    c: Diameter(g0) = 24
FEATURE [PartDesign::Pocket] Pocket030
  AddSubType = 1
  AutoTaperInnerAngle = false
  BaseFeature = -> Pad038
  CheckUpToFaceLimits = true
  ClaimChildren = false
  Fit = 0
  FitJoin = 0
  InnerFit = 0
  InnerFitJoin = 0
  InvalidShape = false
  Length = 5
  Length2 = 100
  Linearize = true
  NewSolid = false
  Profile = -> Sketch069
  Refine = true
  Suppress = false
  TaperInnerAngle = 0
  TaperInnerAngleRev = 0
  TreeRank = 0
  Type = 1
  ValidateShape = true
  _ProfileBasedVersion = 1
  _Version = 1
FEATURE [PartDesign::Body] Body033  label="PlateTirette_2"
  AutoGroupSolids = false
  ClaimAllChildren = false
  ExportMode = 0
  Group = -> [Binder001,Pad038,Sketch069,Pocket030]
  InvalidShape = false
  Origin = -> Origin052
  SingleSolid = true
  Tip = -> Pocket030
  TreeRank = 0
  ValidateShape = true
  _ExportChildren = -> [Pad038,Pocket030]
  _GroupVersion = 1
FEATURE [PartDesign::SubShapeBinder] Binder002  label="Binder002(Pocket030)"
  BindCopyOnChange = 0
  BindMode = 0
  ClaimChildren = false
  Context = -> Part011 [Body034.Binder002.]
  EdgeTolerance = 1e-06
  FillStyle = 0
  Fuse = false
  InvalidShape = false
  MakeFace = true
  MergeEdges = true
  OffsetFill = false
  OffsetIntersection = false
  OffsetJoinType = 0
  OffsetOpenResult = false
  Outline = false
  PartialLoad = false
  Refine = true
  Relative = true
  SplitEdges = false
  Support = -> [Body033[Pocket030.Face5]]
  TightBound = false
  TreeRank = 0
  ValidateShape = true
  _Version = 8
FEATURE [PartDesign::Pad] Pad039
  AddSubType = 0
  AutoTaperInnerAngle = false
  CheckUpToFaceLimits = true
  ClaimChildren = false
  Direction = (-4e-16,-0.642788,0.766044)
  Fit = 0
  FitJoin = 0
  InnerFit = 0
  InnerFitJoin = 0
  InvalidShape = false
  Length = 0.8
  Length2 = 100
  Linearize = true
  NewSolid = false
  Profile = -> Binder002
  Refine = true
  Suppress = false
  TaperInnerAngle = 0
  TaperInnerAngleRev = 0
  TreeRank = 0
  Type = 0
  ValidateShape = true
  _ProfileBasedVersion = 1
FEATURE [Sketcher::SketchObject] Sketch070
  ArcFitTolerance = 0
  AttachmentSupport = -> [Pad039]
  ExternalBSplineMaxDegree = 0
  ExternalBSplineTolerance = 0
  ExternalGeometry = -> [Pad039]
  FullyConstrained = true
  InternalTolerance = 1e-06
  InvalidShape = false
  MakeInternals = false
  MapMode = 5
  Placement = pos=(-3.49e-14,-54.7814,65.286) rot=(1,0,0;0.698132rad)
  Support = -> [Pad039]
  TreeRank = 0
  ValidateShape = true
  sketch-geometry (1):
    g0: Circle CenterX=0 CenterY=-32.5627 CenterZ=0 NormalX=0 NormalY=0 NormalZ=1 AngleXU=0 Radius=15
  constraints (2):
    c: Coincident(g0,g-3)
    c: Diameter(g0) = 30
FEATURE [PartDesign::Pad] Pad040
  AddSubType = 0
  AutoTaperInnerAngle = false
  BaseFeature = -> Pad039
  CheckUpToFaceLimits = true
  ClaimChildren = false
  Direction = (-4e-16,-0.642788,0.766044)
  Fit = 0
  FitJoin = 0
  InnerFit = 0
  InnerFitJoin = 0
  InvalidShape = false
  Length = 10
  Length2 = 100
  Linearize = true
  NewSolid = false
  Profile = -> Sketch070
  Refine = true
  Reversed = true
  Suppress = false
  TaperInnerAngle = 0
  TaperInnerAngleRev = 0
  TreeRank = 0
  Type = 3
  UpToFace = -> Pad039 [Face16]
  ValidateShape = true
  _ProfileBasedVersion = 1
FEATURE [PartDesign::Body] Body034  label="InterPlateTirette"
  AutoGroupSolids = false
  ClaimAllChildren = false
  ExportMode = 0
  Group = -> [Binder002,Pad039,Sketch070,Pad040]
  InvalidShape = false
  Origin = -> Origin053
  SingleSolid = true
  Tip = -> Pad040
  TreeRank = 0
  ValidateShape = true
  _ExportChildren = -> [Pad039,Pad040]
  _GroupVersion = 1
FEATURE [PartDesign::SubShapeBinder] Binder003  label="Binder003(Pad040)"
  BindCopyOnChange = 0
  BindMode = 2
  ClaimChildren = false
  Context = -> Part011 [Body035.Binder003.]
  EdgeTolerance = 1e-06
  FillStyle = 0
  Fuse = false
  InvalidShape = false
  MakeFace = true
  MergeEdges = true
  OffsetFill = false
  OffsetIntersection = false
  OffsetJoinType = 0
  OffsetOpenResult = false
  Outline = false
  PartialLoad = false
  Refine = true
  Relative = true
  SplitEdges = false
  TightBound = false
  TreeRank = 0
  ValidateShape = true
  _Version = 8
FEATURE [PartDesign::Pad] Pad041
  AddSubType = 0
  AutoTaperInnerAngle = false
  CheckUpToFaceLimits = true
  ClaimChildren = false
  Direction = (-4e-16,-0.642788,0.766044)
  Fit = 0
  FitJoin = 0
  InnerFit = 0
  InnerFitJoin = 0
  InvalidShape = false
  Length = 3
  Length2 = 100
  Linearize = true
  NewSolid = false
  Profile = -> Binder003
  Refine = true
  Suppress = false
  TaperInnerAngle = 0
  TaperInnerAngleRev = 0
  TreeRank = 0
  Type = 0
  ValidateShape = true
  _ProfileBasedVersion = 1
FEATURE [Part::SubShapeBinder] Import  label="Import(Pocket030)"
  BindCopyOnChange = 0
  BindMode = 0
  ClaimChildren = false
  Context = -> Part011 [Body035.Import.]
  EdgeTolerance = 1e-06
  FillStyle = 0
  Fuse = false
  InvalidShape = false
  MakeFace = false
  MergeEdges = true
  OffsetFill = false
  OffsetIntersection = false
  OffsetJoinType = 0
  OffsetOpenResult = false
  Outline = false
  PartialLoad = false
  Refine = true
  Relative = true
  SplitEdges = false
  Support = -> [Body033[Pocket030.]]
  TightBound = false
  TreeRank = 0
  ValidateShape = true
  _Version = 8
FEATURE [Sketcher::SketchObject] Sketch071
  ArcFitTolerance = 0
  AttachmentSupport = -> [Pad041]
  ExternalBSplineMaxDegree = 0
  ExternalBSplineTolerance = 0
  ExternalGeometry = -> [Import]
  FullyConstrained = true
  InternalTolerance = 1e-06
  InvalidShape = false
  MakeInternals = false
  MapMode = 5
  Placement = pos=(-3.62e-14,-56.7098,67.5841) rot=(1,0,0;0.698132rad)
  Support = -> [Pad041]
  TreeRank = 0
  ValidateShape = true
  sketch-geometry (2):
    g0: Circle CenterX=0 CenterY=-32.5627 CenterZ=0 NormalX=0 NormalY=0 NormalZ=1 AngleXU=0 Radius=13
    g1: LineSegment [constr] StartX=-1.96e-14 StartY=-55.0073 StartZ=0 EndX=1.98e-14 EndY=-10.1181 EndZ=0
  constraints (5):
    c: PointOnObject(g0,g-2)
    c: Diameter(g0) = 26
    c: PointOnObject(g1,g-4)
    c: Symmetric(g-3,g-3,g1)
    c: Symmetric(g1,g1,g0)
FEATURE [PartDesign::Pocket] Pocket031
  AddSubType = 1
  AutoTaperInnerAngle = false
  BaseFeature = -> Pad041
  CheckUpToFaceLimits = true
  ClaimChildren = false
  Fit = 0
  FitJoin = 0
  InnerFit = 0
  InnerFitJoin = 0
  InvalidShape = false
  Length = 5
  Length2 = 100
  Linearize = true
  NewSolid = false
  Profile = -> Sketch071
  Refine = true
  Suppress = false
  TaperInnerAngle = 0
  TaperInnerAngleRev = 0
  TreeRank = 0
  Type = 1
  ValidateShape = true
  _ProfileBasedVersion = 1
  _Version = 1
FEATURE [PartDesign::Body] Body035  label="PlateTirette_3"
  AutoGroupSolids = false
  ClaimAllChildren = false
  ExportMode = 0
  Group = -> [Binder003,Pad041,Sketch071,Import,Pocket031]
  InvalidShape = false
  Origin = -> Origin054
  SingleSolid = true
  Tip = -> Pocket031
  TreeRank = 0
  ValidateShape = true
  _ExportChildren = -> [Pad041,Import,Pocket031]
  _GroupVersion = 1
FEATURE [App::Part] Part011  label="CoinTirette"
  ClaimAllChildren = false
  ExportMode = 1
  Group = -> [Link066,Body032,Body033,Body034,Body035]
  Origin = -> Origin049
  TreeRank = 0
  _ExportChildren = -> [Link066,Body032,Body033,Body034,Body035]
  _GroupVersion = 1
FEATURE [TechDraw::DrawSVGTemplate] Template002
  Height = 210
  Orientation = 1
  TreeRank = 0
  Width = 297
FEATURE [TechDraw::DrawProjGroupItem] ProjItem003  label="Front004"
  CoarseView = false
  Direction = (0,-0.643,0.766)
  Focus = 100
  HardHidden = false
  IsoCount = 0
  IsoHidden = false
  IsoVisible = false
  LockPosition = true
  Perspective = false
  Rotation = 0
  RotationVector = (-1,0,0)
  ScaleType = 2
  SeamHidden = false
  SeamVisible = true
  SmoothHidden = false
  SmoothVisible = true
  Source = -> [Pad037]
  TreeRank = 0
  Type = 0
  X = 0
  XDirection = (-1,0,0)
  Y = 0
FEATURE [TechDraw::DrawProjGroup] ProjGroup003
  Anchor = -> ProjItem003
  AutoDistribute = true
  LockPosition = false
  ProjectionType = 0
  Rotation = 0
  ScaleType = 0
  Source = -> [Pad037]
  TreeRank = 0
  Views = -> [ProjItem003]
  X = 25.296
  Y = 185.829
  spacingX = 15
  spacingY = 15
FEATURE [TechDraw::DrawProjGroupItem] ProjItem004  label="Front005"
  CoarseView = false
  Direction = (0,-0.643,0.766)
  Focus = 100
  HardHidden = false
  IsoCount = 0
  IsoHidden = false
  IsoVisible = false
  LockPosition = true
  Perspective = false
  Rotation = 0
  RotationVector = (-1,0,0)
  ScaleType = 2
  SeamHidden = false
  SeamVisible = true
  SmoothHidden = false
  SmoothVisible = true
  Source = -> [Pocket030]
  TreeRank = 0
  Type = 0
  X = 0
  XDirection = (-1,0,0)
  Y = 0
FEATURE [TechDraw::DrawProjGroup] ProjGroup004
  Anchor = -> ProjItem004
  AutoDistribute = true
  LockPosition = false
  ProjectionType = 0
  Rotation = 0
  ScaleType = 0
  Source = -> [Pocket030]
  TreeRank = 0
  Views = -> [ProjItem004]
  X = 74.5095
  Y = 185.806
  spacingX = 15
  spacingY = 15
FEATURE [TechDraw::DrawProjGroupItem] ProjItem006  label="Front007"
  CoarseView = false
  Direction = (0,-0.643,0.766)
  Focus = 100
  HardHidden = false
  IsoCount = 0
  IsoHidden = false
  IsoVisible = false
  LockPosition = true
  Perspective = false
  Rotation = 0
  RotationVector = (-1,0,0)
  ScaleType = 2
  SeamHidden = false
  SeamVisible = true
  SmoothHidden = false
  SmoothVisible = true
  Source = -> [Pocket031]
  TreeRank = 0
  Type = 0
  X = 0
  XDirection = (-1,0,0)
  Y = 0
FEATURE [TechDraw::DrawProjGroup] ProjGroup006
  Anchor = -> ProjItem006
  AutoDistribute = true
  LockPosition = false
  ProjectionType = 0
  Rotation = 0
  ScaleType = 0
  Source = -> [Pocket031]
  TreeRank = 0
  Views = -> [ProjItem006]
  X = 123.484
  Y = 185.606
  spacingX = 15
  spacingY = 15
FEATURE [TechDraw::DrawPage] Page002  label="Laser3mmPlateTirette"
  KeepUpdated = true
  NextBalloonIndex = 1
  ProjectionType = 0
  Template = -> Template002
  TreeRank = 0
  Views = -> [ProjGroup003,ProjGroup004,ProjGroup006]
FEATURE [TechDraw::DrawSVGTemplate] Template003
  Height = 210
  Orientation = 1
  TreeRank = 0
  Width = 297
FEATURE [TechDraw::DrawProjGroupItem] ProjItem007  label="Front008"
  CoarseView = false
  Direction = (0,-0.643,0.766)
  Focus = 100
  HardHidden = false
  IsoCount = 0
  IsoHidden = false
  IsoVisible = false
  LockPosition = true
  Perspective = false
  Rotation = 0
  RotationVector = (-1,0,0)
  ScaleType = 2
  SeamHidden = false
  SeamVisible = true
  SmoothHidden = false
  SmoothVisible = true
  Source = -> [Pad040]
  TreeRank = 0
  Type = 0
  X = 0
  XDirection = (-1,0,0)
  Y = 0
FEATURE [TechDraw::DrawProjGroup] ProjGroup007
  Anchor = -> ProjItem007
  AutoDistribute = true
  LockPosition = false
  ProjectionType = 0
  Rotation = 0
  ScaleType = 0
  Source = -> [Pad040]
  TreeRank = 0
  Views = -> [ProjItem007]
  X = 25.1312
  Y = 184.681
  spacingX = 15
  spacingY = 15
FEATURE [TechDraw::DrawPage] Page003  label="LaserPetg"
  KeepUpdated = true
  NextBalloonIndex = 1
  ProjectionType = 0
  Template = -> Template003
  TreeRank = 0
  Views = -> [ProjGroup007]
FEATURE [App::Link] Link067  label="Link067(CoinStandard)"
  AutoLinkLabel = true
  AutoPlacement = true
  LinkedObject = -> Body029
  SyncGroupVisibility = false
  TreeRank = 0
  _LinkVersion = 1
FEATURE [PartDesign::SubShapeBinder] Binder004  label="Binder004(Chamfer023)"
  BindCopyOnChange = 0
  BindMode = 0
  ClaimChildren = false
  Context = -> Part012 [Body036.Binder004.]
  EdgeTolerance = 1e-06
  FillStyle = 0
  Fuse = false
  InvalidShape = false
  MakeFace = true
  MergeEdges = true
  OffsetFill = false
  OffsetIntersection = false
  OffsetJoinType = 0
  OffsetOpenResult = false
  Outline = false
  PartialLoad = false
  Refine = true
  Relative = true
  SplitEdges = false
  Support = -> [Chamfer023[Face30]]
  TightBound = false
  TreeRank = 0
  ValidateShape = true
  _Version = 8
FEATURE [Sketcher::SketchObject] Sketch072
  ArcFitTolerance = 0
  AttachmentSupport = -> [Binder004]
  ExternalBSplineMaxDegree = 0
  ExternalBSplineTolerance = 0
  ExternalGeometry = -> [Binder004]
  FullyConstrained = true
  InternalTolerance = 1e-06
  InvalidShape = false
  MakeInternals = false
  MapMode = 5
  Placement = pos=(-2.82e-14,-50.4105,60.0769) rot=(1,0,0;0.698132rad)
  Support = -> [Binder004]
  TreeRank = 0
  ValidateShape = true
  sketch-geometry (2):
    g0: Circle CenterX=-14 CenterY=-14.7181 CenterZ=0 NormalX=0 NormalY=0 NormalZ=1 AngleXU=0 Radius=1.6
    g1: Circle CenterX=14 CenterY=-14.7181 CenterZ=0 NormalX=0 NormalY=0 NormalZ=1 AngleXU=0 Radius=1.6
  constraints (4):
    c: Coincident(g0,g-10)
    c: Coincident(g1,g-9)
    c: Diameter(g1) = 3.2
    c: Equal(g1,g0)
FEATURE [PartDesign::Pad] Pad042
  AddSubType = 0
  AutoTaperInnerAngle = false
  CheckUpToFaceLimits = true
  ClaimChildren = false
  Direction = (1,1,1)
  Fit = 0
  FitJoin = 0
  InnerFit = 0
  InnerFitJoin = 0
  InvalidShape = false
  Length = 3
  Length2 = 100
  Linearize = true
  NewSolid = false
  Profile = -> Sketch072
  Refine = true
  Suppress = false
  TaperInnerAngle = 0
  TaperInnerAngleRev = 0
  TreeRank = 0
  Type = 0
  ValidateShape = true
  _ProfileBasedVersion = 1
FEATURE [App::FeaturePython] WPProxy  # WARN: FeaturePython — macro-defined, semantics opaque (R4)
  Placement = pos=(-1.1e-15,-76.5169,42.0872) rot=(1,0,0;0.698132rad)
  TreeRank = 0
FEATURE [Part::Part2DObjectPython] ShapeString001  # Draft 2D object (typed FeaturePython)
  FontFile = <userpath>/Downloads/baveuse/baveuse.ttf
  InvalidShape = false
  Placement = pos=(-9,-91.52,42.09) rot=(1,0,0;0.698132rad)
  Size = 10
  String = K
  Tracking = 0
  TreeRank = 0
  ValidateShape = true
FEATURE [PartDesign::SubShapeBinder] Import001  label="Import001(ShapeString001)"
  BindCopyOnChange = 0
  BindMode = 0
  ClaimChildren = false
  Context = -> Part012 [Body036.Import001.]
  EdgeTolerance = 1e-06
  FillStyle = 0
  Fuse = false
  InvalidShape = false
  MakeFace = false
  MergeEdges = true
  OffsetFill = false
  OffsetIntersection = false
  OffsetJoinType = 0
  OffsetOpenResult = false
  Outline = false
  PartialLoad = false
  Refine = true
  Relative = true
  SplitEdges = false
  Support = -> [ShapeString001]
  TightBound = false
  TreeRank = 0
  ValidateShape = true
  _Version = 8
FEATURE [PartDesign::Pocket] Pocket032
  AddSubType = 1
  AutoTaperInnerAngle = false
  BaseFeature = -> Pad042
  CheckUpToFaceLimits = true
  ClaimChildren = false
  Fit = 0
  FitJoin = 0
  InnerFit = 0
  InnerFitJoin = 0
  InvalidShape = false
  Length = 10
  Length2 = 100
  Linearize = true
  NewSolid = false
  Profile = -> Import001
  Refine = true
  Suppress = false
  TaperInnerAngle = 0
  TaperInnerAngleRev = 0
  TreeRank = 0
  Type = 0
  ValidateShape = true
  _ProfileBasedVersion = 1
  _Version = 1
FEATURE [PartDesign::Chamfer] Chamfer024
  AddSubType = 0
  Angle = 45
  Base = -> Pocket032 [Edge48,Edge49,Edge8,Edge5,Edge1,Edge2]
  BaseFeature = -> Pocket032
  ChamferType = 0
  FlipDirection = false
  InvalidShape = false
  NewSolid = false
  Refine = true
  Size = 0.4
  Size2 = 1
  SupportTransform = false
  Suppress = false
  TreeRank = 0
  ValidateShape = true
FEATURE [PartDesign::Body] Body036  label="PlateLogo"
  AutoGroupSolids = false
  ClaimAllChildren = false
  ExportMode = 0
  Group = -> [Binder004,Sketch072,Pad042,ShapeString001,Import001,Pocket032,Chamfer024]
  InvalidShape = false
  Origin = -> Origin056
  SingleSolid = true
  Tip = -> Chamfer024
  TreeRank = 0
  ValidateShape = true
  _ExportChildren = -> [Binder004,Pad042,ShapeString001,Pocket032,Chamfer024]
  _GroupVersion = 1
FEATURE [PartDesign::FeatureBase] Clone001
  BaseFeature = -> Pad042
  InvalidShape = false
  NewSolid = false
  Suppress = false
  TreeRank = 10
  ValidateShape = true
FEATURE [Sketcher::SketchObject] Sketch073
  ArcFitTolerance = 0
  AttachmentSupport = -> [Clone001]
  ExternalBSplineMaxDegree = 0
  ExternalBSplineTolerance = 0
  ExternalGeometry = -> [Clone001]
  FullyConstrained = true
  InternalTolerance = 1e-06
  InvalidShape = false
  MakeInternals = false
  MapMode = 5
  Placement = pos=(-3.18e-14,-52.3388,62.375) rot=(1,0,0;0.698132rad)
  Support = -> [Clone001]
  TreeRank = 12
  ValidateShape = true
  sketch-geometry (1):
    g0: Circle CenterX=0 CenterY=-32.5673 CenterZ=0 NormalX=0 NormalY=0 NormalZ=1 AngleXU=0 Radius=7.5
  constraints (3):
    c: PointOnObject(g0,g-2)
    c: DistanceY(g-3,g0) = 22.44
    c: Diameter(g0) = 15
FEATURE [PartDesign::Pocket] Pocket033
  AddSubType = 1
  AutoTaperInnerAngle = false
  BaseFeature = -> Clone001
  CheckUpToFaceLimits = true
  ClaimChildren = false
  Fit = 0
  FitJoin = 0
  InnerFit = 0
  InnerFitJoin = 0
  InvalidShape = false
  Length = 5
  Length2 = 100
  Linearize = true
  NewSolid = false
  Profile = -> Sketch073
  Refine = true
  Suppress = false
  TaperInnerAngle = 0
  TaperInnerAngleRev = 0
  TreeRank = 13
  Type = 1
  ValidateShape = true
  _ProfileBasedVersion = 1
  _Version = 1
FEATURE [PartDesign::Body] Body037  label="PlateInit"
  AutoGroupSolids = false
  BaseFeature = -> Pad042
  ClaimAllChildren = false
  ExportMode = 0
  Group = -> [Clone001,Sketch073,Pocket033]
  InvalidShape = false
  Origin = -> Origin057
  SingleSolid = true
  Tip = -> Pocket033
  TreeRank = 11
  ValidateShape = true
  _ExportChildren = -> [Clone001,Pocket033]
  _GroupVersion = 1
FEATURE [App::Part] Part012  label="CoinLogo"
  ClaimAllChildren = false
  ExportMode = 1
  Group = -> [Link067,Body036,WPProxy,ShapeString001,Body037]
  Origin = -> Origin055
  TreeRank = 0
  _ExportChildren = -> [Link067,Body036,WPProxy,ShapeString001,Body037]
  _GroupVersion = 1
FEATURE [TechDraw::DrawSVGTemplate] Template004
  Height = 210
  Orientation = 1
  TreeRank = 15
  Width = 297
FEATURE [TechDraw::DrawProjGroupItem] ProjItem008  label="Front009"
  CoarseView = false
  Direction = (0,-0.643,0.766)
  Focus = 100
  HardHidden = false
  IsoCount = 0
  IsoHidden = false
  IsoVisible = false
  LockPosition = true
  Perspective = false
  Rotation = 0
  RotationVector = (-1,0,0)
  ScaleType = 2
  SeamHidden = false
  SeamVisible = true
  SmoothHidden = false
  SmoothVisible = true
  Source = -> [Pocket033]
  TreeRank = 18
  Type = 0
  X = 0
  XDirection = (-1,0,0)
  Y = 0
FEATURE [TechDraw::DrawProjGroup] ProjGroup008
  Anchor = -> ProjItem008
  AutoDistribute = true
  LockPosition = false
  ProjectionType = 0
  Rotation = 0
  ScaleType = 0
  Source = -> [Pocket033]
  TreeRank = 19
  Views = -> [ProjItem008]
  X = 24.3999
  Y = 186.325
  spacingX = 15
  spacingY = 15
FEATURE [TechDraw::DrawPage] Page004  label="Laser3mmPlateInit"
  KeepUpdated = true
  NextBalloonIndex = 1
  ProjectionType = 0
  Template = -> Template004
  TreeRank = 16
  Views = -> [ProjGroup008]
FEATURE [TechDraw::DrawSVGTemplate] Template005
  Height = 210
  Orientation = 1
  TreeRank = 21
  Width = 297
FEATURE [TechDraw::DrawProjGroupItem] ProjItem009  label="Front010"
  CoarseView = false
  Direction = (0,0,1)
  Focus = 100
  HardHidden = false
  IsoCount = 0
  IsoHidden = false
  IsoVisible = false
  LockPosition = true
  Perspective = false
  Rotation = 0
  RotationVector = (0,1,0)
  ScaleType = 2
  SeamHidden = false
  SeamVisible = true
  SmoothHidden = false
  SmoothVisible = true
  Source = -> [Fillet013]
  TreeRank = 24
  Type = 0
  X = 0
  XDirection = (0,1,0)
  Y = 0
FEATURE [TechDraw::DrawProjGroup] ProjGroup009
  Anchor = -> ProjItem009
  AutoDistribute = true
  LockPosition = false
  ProjectionType = 0
  Rotation = 0
  ScaleType = 0
  Source = -> [Fillet013]
  TreeRank = 23
  Views = -> [ProjItem009]
  X = 49.3207
  Y = 152.885
  spacingX = 15
  spacingY = 15
FEATURE [TechDraw::DrawPage] Page005  label="Laser5mmCaleCentrale"
  KeepUpdated = true
  NextBalloonIndex = 1
  ProjectionType = 0
  Template = -> Template005
  TreeRank = 26
  Views = -> [ProjGroup009]
FEATURE [App::Link] Link068  label="Link068(633ZZ)"
  AutoLinkLabel = true
  AutoPlacement = true
  LinkPlacement = pos=(-123.877,-2.56104,0) rot=(0,0,1;0rad)
  LinkedObject = -> <external generic-hardware.FCStd>#Part035
  Placement = pos=(-123.877,-2.56104,0) rot=(0,0,1;0rad)
  SyncGroupVisibility = false
  TreeRank = 27
  _LinkVersion = 1
FEATURE [App::Link] Link069  label="Link069(*633ZZ)"
  AutoLinkLabel = true
  AutoPlacement = true
  LinkPlacement = pos=(59.7205,108.561,0) rot=(0,0,1;0rad)
  LinkedObject = -> Link068
  Placement = pos=(59.7205,108.561,0) rot=(0,0,1;0rad)
  SyncGroupVisibility = false
  TreeRank = 28
  _LinkVersion = 1
FEATURE [App::Link] Link070  label="Link070(*633ZZ)"
  AutoLinkLabel = true
  AutoPlacement = true
  LinkPlacement = pos=(123.877,-2.56104,0) rot=(0,0,1;0rad)
  LinkedObject = -> Link068
  Placement = pos=(123.877,-2.56104,0) rot=(0,0,1;0rad)
  SyncGroupVisibility = false
  TreeRank = 29
  _LinkVersion = 1
FEATURE [App::Link] Link071  label="Link071(*633ZZ)"
  AutoLinkLabel = true
  AutoPlacement = true
  LinkPlacement = pos=(-59.7205,108.561,0) rot=(0,0,1;0rad)
  LinkedObject = -> Link068
  Placement = pos=(-59.7205,108.561,0) rot=(0,0,1;0rad)
  SyncGroupVisibility = false
  TreeRank = 30
  _LinkVersion = 1
FEATURE [App::Link] Link072  label="Link072(*633ZZ)"
  AutoLinkLabel = true
  AutoPlacement = true
  LinkPlacement = pos=(64.1564,-106,0) rot=(0,0,1;0rad)
  LinkedObject = -> Link068
  Placement = pos=(64.1564,-106,0) rot=(0,0,1;0rad)
  SyncGroupVisibility = false
  TreeRank = 31
  _LinkVersion = 1
FEATURE [App::Link] Link073  label="Link073(*633ZZ)"
  AutoLinkLabel = true
  AutoPlacement = true
  LinkPlacement = pos=(-64.1564,-106,0) rot=(0,0,1;0rad)
  LinkedObject = -> Link068
  Placement = pos=(-64.1564,-106,0) rot=(0,0,1;0rad)
  SyncGroupVisibility = false
  TreeRank = 32
  _LinkVersion = 1
FEATURE [App::DocumentObjectGroup] Group003  label="Roulement"
  ClaimAllChildren = true
  ExportMode = 1
  Group = -> [Link068,Link069,Link070,Link071,Link072,Link073]
  TreeRank = 33
  _GroupVersion = 1
FEATURE [Part::FeaturePython] Screw004  label="M3x16-Screw"  # Fasteners workbench fastener (typed FeaturePython)
  InvalidShape = false
  Placement = pos=(59.7205,108.561,-5) rot=(-1,0,0;3.14159rad)
  TreeRank = 40
  ValidateShape = true
  baseObject = -> Body019 [?Edge333]
  diameter = 1
  invert = true
  leftHanded = false
  length = 5
  lengthCustom = 16
  matchOuter = false
  offset = 0
  thread = false
  type = 40
FEATURE [Part::FeaturePython] Screw005  label="M3x16-Screw041"  # Fasteners workbench fastener (typed FeaturePython)
  InvalidShape = false
  Placement = pos=(-59.7205,108.561,-5) rot=(-1,0,0;3.14159rad)
  TreeRank = 41
  ValidateShape = true
  baseObject = -> Body019 [?Edge297]
  diameter = 1
  invert = true
  leftHanded = false
  length = 5
  lengthCustom = 16
  matchOuter = false
  offset = 0
  thread = false
  type = 40
FEATURE [Part::FeaturePython] Screw006  label="M3x16-Screw042"  # Fasteners workbench fastener (typed FeaturePython)
  InvalidShape = false
  Placement = pos=(-123.877,-2.56104,-5) rot=(-1,0,0;3.14159rad)
  TreeRank = 42
  ValidateShape = true
  baseObject = -> Body019 [?Edge243]
  diameter = 1
  invert = true
  leftHanded = false
  length = 5
  lengthCustom = 16
  matchOuter = false
  offset = 0
  thread = false
  type = 40
FEATURE [Part::FeaturePython] Screw007  label="M3x16-Screw043"  # Fasteners workbench fastener (typed FeaturePython)
  InvalidShape = false
  Placement = pos=(-64.1564,-106,-5) rot=(-1,0,0;3.14159rad)
  TreeRank = 43
  ValidateShape = true
  baseObject = -> Body019 [?Edge209]
  diameter = 1
  invert = true
  leftHanded = false
  length = 5
  lengthCustom = 16
  matchOuter = false
  offset = 0
  thread = false
  type = 40
FEATURE [Part::FeaturePython] Screw008  label="M3x16-Screw044"  # Fasteners workbench fastener (typed FeaturePython)
  InvalidShape = false
  Placement = pos=(64.1564,-106,-5) rot=(-1,0,0;3.14159rad)
  TreeRank = 44
  ValidateShape = true
  baseObject = -> Body019 [?Edge251]
  diameter = 1
  invert = true
  leftHanded = false
  length = 5
  lengthCustom = 16
  matchOuter = false
  offset = 0
  thread = false
  type = 40
FEATURE [Part::FeaturePython] Screw009  label="M3x16-Screw045"  # Fasteners workbench fastener (typed FeaturePython)
  InvalidShape = false
  Placement = pos=(123.877,-2.56104,-5) rot=(-1,0,0;3.14159rad)
  TreeRank = 45
  ValidateShape = true
  baseObject = -> Body019 [?Edge285]
  diameter = 1
  invert = true
  leftHanded = false
  length = 5
  lengthCustom = 16
  matchOuter = false
  offset = 0
  thread = false
  type = 40
FEATURE [Part::FeaturePython] Nut  label="M3-Nut"  # Fasteners workbench fastener (typed FeaturePython)
  InvalidShape = false
  Placement = pos=(123.877,-2.56104,5) rot=(0,0,1;0rad)
  TreeRank = 59
  ValidateShape = true
  baseObject = -> Body019 [?Edge87]
  diameter = 1
  invert = false
  leftHanded = false
  matchOuter = false
  offset = 5
  thread = false
  type = 5
FEATURE [Part::FeaturePython] Nut001  label="M3-Nut051"  # Fasteners workbench fastener (typed FeaturePython)
  InvalidShape = false
  Placement = pos=(64.1564,-106,5) rot=(0,0,1;0rad)
  TreeRank = 60
  ValidateShape = true
  baseObject = -> Body019 [?Edge70]
  diameter = 1
  invert = false
  leftHanded = false
  matchOuter = false
  offset = 5
  thread = false
  type = 5
FEATURE [Part::FeaturePython] Nut002  label="M3-Nut052"  # Fasteners workbench fastener (typed FeaturePython)
  InvalidShape = false
  Placement = pos=(-64.1564,-106,5) rot=(0,0,1;0rad)
  TreeRank = 61
  ValidateShape = true
  baseObject = -> Body019 [?Edge49]
  diameter = 1
  invert = false
  leftHanded = false
  matchOuter = false
  offset = 5
  thread = false
  type = 5
FEATURE [Part::FeaturePython] Nut003  label="M3-Nut053"  # Fasteners workbench fastener (typed FeaturePython)
  InvalidShape = false
  Placement = pos=(-123.877,-2.56104,5) rot=(0,0,1;0rad)
  TreeRank = 62
  ValidateShape = true
  baseObject = -> Body019 [?Edge66]
  diameter = 1
  invert = false
  leftHanded = false
  matchOuter = false
  offset = 5
  thread = false
  type = 5
FEATURE [Part::FeaturePython] Nut004  label="M3-Nut054"  # Fasteners workbench fastener (typed FeaturePython)
  InvalidShape = false
  Placement = pos=(-59.7205,108.561,5) rot=(0,0,1;0rad)
  TreeRank = 63
  ValidateShape = true
  baseObject = -> Body019 [?Edge93]
  diameter = 1
  invert = false
  leftHanded = false
  matchOuter = false
  offset = 5
  thread = false
  type = 5
FEATURE [Part::FeaturePython] Nut005  label="M3-Nut055"  # Fasteners workbench fastener (typed FeaturePython)
  InvalidShape = false
  Placement = pos=(59.7205,108.561,5) rot=(0,0,1;0rad)
  TreeRank = 64
  ValidateShape = true
  baseObject = -> Body019 [?Edge111]
  diameter = 1
  invert = false
  leftHanded = false
  matchOuter = false
  offset = 5
  thread = false
  type = 5
FEATURE [App::DocumentObjectGroup] Group004  label="Visserie001"
  ClaimAllChildren = true
  ExportMode = 1
  Group = -> [Screw004,Screw005,Screw006,Screw007,Screw008,Screw009,Nut,Nut001,Nut002,Nut003,Nut004,Nut005]
  TreeRank = 46
  _GroupVersion = 1
FEATURE [App::Part] Part007  label="EnsembleSemelle"
  ClaimAllChildren = false
  ExportMode = 1
  Group = -> [Body019,Body020,Link068,Link069,Link070,Link071,Link072,Link073,Group003,Group004,Screw004,Screw008,Screw005,Screw006,Screw007,Screw009,Nut,Nut001,Nut002,Nut003,Nut004,Nut005]
  Origin = -> Origin039
  TreeRank = 0
  _ExportChildren = -> [Body019,Body020,Group003,Group004]
  _GroupVersion = 1
FEATURE [App::Link] Link074  label="Link074(BAU-2195813)"
  AutoLinkLabel = true
  AutoPlacement = true
  LinkPlacement = pos=(-3.01e-14,-76.5631,42.1127) rot=(1,0,0;0.696386rad)
  LinkedObject = -> <external generic-hardware.FCStd>#Part036
  Placement = pos=(-3.01e-14,-76.5631,42.1127) rot=(1,0,0;0.696386rad)
  SyncGroupVisibility = false
  TreeRank = 65
  _LinkVersion = 1
FEATURE [App::Part] Part010  label="CoinBAU"
  ClaimAllChildren = false
  ExportMode = 1
  Group = -> [Link065,Body030,Link074]
  Origin = -> Origin047
  TreeRank = 0
  _ExportChildren = -> [Link065,Body030,Link074]
  _GroupVersion = 1
FEATURE [TechDraw::DrawSVGTemplate] Template006
  Height = 210
  Orientation = 1
  TreeRank = 68
  Width = 297
FEATURE [TechDraw::DrawProjGroupItem] ProjItem010  label="Front011"
  CoarseView = false
  Direction = (0,0,1)
  Focus = 100
  HardHidden = false
  IsoCount = 0
  IsoHidden = false
  IsoVisible = false
  LockPosition = true
  Perspective = false
  Rotation = 0
  RotationVector = (1,0,0)
  Scale = 0.5
  ScaleType = 2
  SeamHidden = false
  SeamVisible = true
  SmoothHidden = false
  SmoothVisible = true
  Source = -> [Part007]
  TreeRank = 71
  Type = 0
  X = 0
  XDirection = (1,0,0)
  Y = 0
FEATURE [TechDraw::DrawProjGroup] ProjGroup010
  Anchor = -> ProjItem010
  AutoDistribute = true
  LockPosition = false
  ProjectionType = 0
  Rotation = 0
  Scale = 0.5
  ScaleType = 2
  Source = -> [Part007]
  TreeRank = 72
  Views = -> [ProjItem010]
  X = 148.5
  Y = 105
  spacingX = 15
  spacingY = 15
FEATURE [TechDraw::DrawViewDimension] Dimension001
  Arbitrary = false
  ArbitraryTolerances = false
  EqualTolerance = true
  FormatSpec = %.2f
  FormatSpecOverTolerance = %+.2f
  FormatSpecUnderTolerance = %+.2f
  Inverted = false
  LockPosition = false
  MeasureType = 1
  OverTolerance = 0
  References2D = -> [ProjItem010]
  Rotation = 0
  ScaleType = 0
  TheoreticalExact = false
  TreeRank = 74
  Type = 2
  UnderTolerance = 0
  X = -105.201
  Y = 7.2116
FEATURE [TechDraw::DrawViewDimension] Dimension
  Arbitrary = false
  ArbitraryTolerances = false
  EqualTolerance = true
  FormatSpec = %.2f
  FormatSpecOverTolerance = %+.2f
  FormatSpecUnderTolerance = %+.2f
  Inverted = false
  LockPosition = false
  MeasureType = 1
  OverTolerance = 0
  References2D = -> [ProjItem010]
  Rotation = 0
  ScaleType = 0
  TheoreticalExact = false
  TreeRank = 75
  Type = 2
  UnderTolerance = 0
  X = -120.317
  Y = 3.82914
FEATURE [TechDraw::DrawViewDimension] Dimension002
  Arbitrary = false
  ArbitraryTolerances = false
  EqualTolerance = true
  FormatSpec = %.2f
  FormatSpecOverTolerance = %+.2f
  FormatSpecUnderTolerance = %+.2f
  Inverted = false
  LockPosition = false
  MeasureType = 1
  OverTolerance = 0
  References2D = -> [ProjItem010]
  Rotation = 0
  ScaleType = 0
  TheoreticalExact = false
  TreeRank = 76
  Type = 2
  UnderTolerance = 0
  X = -88.6226
  Y = -26.0434
FEATURE [TechDraw::DrawViewDimension] Dimension003
  Arbitrary = false
  ArbitraryTolerances = false
  EqualTolerance = true
  FormatSpec = %.2f
  FormatSpecOverTolerance = %+.2f
  FormatSpecUnderTolerance = %+.2f
  Inverted = false
  LockPosition = false
  MeasureType = 1
  OverTolerance = 0
  References2D = -> [ProjItem010]
  Rotation = 0
  ScaleType = 0
  TheoreticalExact = false
  TreeRank = 77
  Type = 2
  UnderTolerance = 0
  X = -88.471
  Y = 25.2924
FEATURE [TechDraw::DrawViewDimension] Dimension004
  Arbitrary = false
  ArbitraryTolerances = false
  EqualTolerance = true
  FormatSpec = %.2f
  FormatSpecOverTolerance = %+.2f
  FormatSpecUnderTolerance = %+.2f
  Inverted = false
  LockPosition = false
  MeasureType = 1
  OverTolerance = 0
  References2D = -> [ProjItem010]
  Rotation = 0
  ScaleType = 0
  TheoreticalExact = false
  TreeRank = 78
  Type = 2
  UnderTolerance = 0
  X = 80.7437
  Y = -25.2392
FEATURE [TechDraw::DrawPage] Page006  label="PlanSemelle"
  KeepUpdated = true
  NextBalloonIndex = 1
  ProjectionType = 0
  Template = -> Template006
  TreeRank = 69
  Views = -> [ProjGroup010,Dimension001,Dimension,Dimension002,Dimension003,Dimension004]
FEATURE [App::DocumentObjectGroup] Group005  label="Plans"
  ClaimAllChildren = true
  ExportMode = 1
  Group = -> [Page006]
  TreeRank = 66
  _GroupVersion = 1
FEATURE [TechDraw::DrawSVGTemplate] Template007
  Height = 210
  Orientation = 1
  TreeRank = 80
  Width = 297
FEATURE [TechDraw::DrawProjGroupItem] ProjItem011  label="Front012"
  CoarseView = false
  Direction = (0,0,1)
  Focus = 100
  HardHidden = false
  IsoCount = 0
  IsoHidden = false
  IsoVisible = false
  LockPosition = true
  Perspective = false
  Rotation = 0
  RotationVector = (0,1,0)
  ScaleType = 2
  SeamHidden = false
  SeamVisible = true
  SmoothHidden = false
  SmoothVisible = true
  Source = -> [Fillet011]
  TreeRank = 83
  Type = 0
  X = 0
  XDirection = (0,1,0)
  Y = 0
FEATURE [TechDraw::DrawProjGroup] ProjGroup011
  Anchor = -> ProjItem011
  AutoDistribute = true
  LockPosition = false
  ProjectionType = 0
  Rotation = 0
  ScaleType = 0
  Source = -> [Fillet011]
  TreeRank = 84
  Views = -> [ProjItem011]
  X = 148.5
  Y = 105
  spacingX = 15
  spacingY = 15
FEATURE [TechDraw::DrawPage] Page007  label="Laser5mmSemelle"
  KeepUpdated = true
  NextBalloonIndex = 1
  ProjectionType = 0
  Template = -> Template007
  TreeRank = 81
  Views = -> [ProjGroup011]
FEATURE [App::Link] Link075  label="Link075(Semelle)"
  AutoLinkLabel = true
  AutoPlacement = true
  LinkedObject = -> Body019
  ShowElement = false
  SyncGroupVisibility = false
  TreeRank = 94
  _LinkVersion = 1
FEATURE [Sketcher::SketchObject] Sketch074
  ArcFitTolerance = 1e-06
  AttachmentSupport = -> [XY_Plane047]
  ExternalBSplineMaxDegree = 5
  ExternalBSplineTolerance = 0.0001
  FullyConstrained = true
  InternalTolerance = 1e-06
  InvalidShape = false
  MakeInternals = true
  MapMode = 5
  Support = -> [XY_Plane047]
  TreeRank = 105
  ValidateShape = true
  sketch-geometry (1):
    g0: Circle CenterX=0 CenterY=0 CenterZ=0 NormalX=0 NormalY=0 NormalZ=1 AngleXU=0 Radius=10
  constraints (2):
    c: Coincident(g0,g-1)
    c: Diameter(g0) = 20
FEATURE [PartDesign::Pad] Pad043
  AddSubType = 0
  AlongSketchNormal = false
  AutoTaperInnerAngle = true
  CheckUpToFaceLimits = true
  ClaimChildren = false
  Direction = (0,0,1)
  Fit = 0
  FitJoin = 0
  InnerFit = 0
  InnerFitJoin = 0
  InvalidShape = false
  Length = 4
  Length2 = 100
  Linearize = true
  NewSolid = false
  Profile = -> Sketch074
  Refine = true
  Suppress = false
  TaperAngle = 10
  TaperInnerAngle = -10
  TaperInnerAngleRev = 0
  TreeRank = 106
  Type = 0
  ValidateShape = true
  _ProfileBasedVersion = 1
FEATURE [PartDesign::Pad] Pad044
  AddSubType = 0
  AlongSketchNormal = false
  AutoTaperInnerAngle = true
  BaseFeature = -> Pad043
  CheckUpToFaceLimits = true
  ClaimChildren = false
  Direction = (0,0,1)
  Fit = 0
  FitJoin = 0
  InnerFit = 0
  InnerFitJoin = 0
  InvalidShape = false
  Length = 2
  Length2 = 100
  Linearize = true
  NewSolid = false
  Profile = -> Pad043 [Face3]
  Refine = true
  Suppress = false
  TaperInnerAngle = 0
  TaperInnerAngleRev = 0
  TreeRank = 107
  Type = 0
  ValidateShape = true
  _ProfileBasedVersion = 1
FEATURE [Sketcher::SketchObject] Sketch075
  ArcFitTolerance = 1e-06
  AttachmentSupport = -> [Pad044]
  ExternalBSplineMaxDegree = 5
  ExternalBSplineTolerance = 0.0001
  FullyConstrained = true
  InternalTolerance = 1e-06
  InvalidShape = false
  MakeInternals = true
  MapMode = 5
  Placement = pos=(0,0,6) rot=(0,0,1;0rad)
  Support = -> [Pad044]
  TreeRank = 108
  ValidateShape = true
  sketch-geometry (1):
    g0: Circle CenterX=0 CenterY=0 CenterZ=0 NormalX=0 NormalY=0 NormalZ=1 AngleXU=0 Radius=35
  constraints (2):
    c: Coincident(g0,g-1)
    c: Diameter(g0) = 70
FEATURE [PartDesign::Pad] Pad045
  AddSubType = 0
  AlongSketchNormal = false
  AutoTaperInnerAngle = true
  BaseFeature = -> Pad044
  CheckUpToFaceLimits = true
  ClaimChildren = false
  Direction = (0,0,1)
  Fit = 0
  FitJoin = 0
  InnerFit = 0
  InnerFitJoin = 0
  InvalidShape = false
  Length = 15
  Length2 = 100
  Linearize = true
  NewSolid = false
  Profile = -> Sketch075
  Refine = true
  Suppress = false
  TaperAngle = 10
  TaperInnerAngle = -10
  TaperInnerAngleRev = 0
  TreeRank = 109
  Type = 0
  ValidateShape = true
  _ProfileBasedVersion = 1
FEATURE [Part::SubShapeBinder] Import002  label="Import002(Fillet011)"
  BindCopyOnChange = 0
  BindMode = 0
  ClaimChildren = false
  Context = -> Group002 [Body038.Import002.]
  EdgeTolerance = 1e-06
  FillStyle = 0
  Fuse = false
  InvalidShape = false
  MakeFace = false
  MergeEdges = true
  OffsetFill = false
  OffsetIntersection = false
  OffsetJoinType = 0
  OffsetOpenResult = false
  Outline = false
  PartialLoad = false
  Relative = true
  SplitEdges = false
  Support = -> [Link075[Fillet011.]]
  TightBound = false
  TreeRank = 110
  ValidateShape = true
  _Version = 8
FEATURE [Sketcher::SketchObject] Sketch076
  ArcFitTolerance = 1e-06
  AttachmentSupport = -> [YZ_Plane047]
  ExternalBSplineMaxDegree = 5
  ExternalBSplineTolerance = 0.0001
  ExternalGeometry = -> [Pad045]
  FullyConstrained = true
  InternalTolerance = 1e-06
  InvalidShape = false
  MakeInternals = true
  MapMode = 5
  Placement = pos=(0,0,0) rot=(0.57735,0.57735,0.57735;2.0944rad)
  Support = -> [YZ_Plane047]
  TreeRank = 111
  ValidateShape = true
  sketch-geometry (5):
    g0: LineSegment StartX=21 StartY=6 StartZ=0 EndX=29 EndY=6 EndZ=0
    g1: LineSegment StartX=29 StartY=6 StartZ=0 EndX=29 EndY=10 EndZ=0
    g2: LineSegment StartX=29 StartY=10 StartZ=0 EndX=21 EndY=10 EndZ=0
    g3: LineSegment StartX=21 StartY=10 StartZ=0 EndX=21 EndY=6 EndZ=0
    g4: LineSegment [constr] StartX=25 StartY=6 StartZ=0 EndX=25 EndY=10 EndZ=0
  constraints (15):
    c: Coincident(g0,g1)
    c: Coincident(g1,g2)
    c: Coincident(g2,g3)
    c: Coincident(g3,g0)
    c: Horizontal(g0)
    c: Horizontal(g2)
    c: Vertical(g1)
    c: Vertical(g3)
    c: PointOnObject(g4,g2)
    c: Vertical(g4)
    c: Symmetric(g0,g0,g4)
    c: DistanceX(g4) = 25
    c: DistanceX(g0,g0) = 8
    c: PointOnObject(g0,g-3)
    c: DistanceY(g1,g1) = 4
FEATURE [PartDesign::Groove] Groove
  AddSubType = 1
  Angle = 360
  Axis = (-2e-16,3e-16,1)
  Base = (0,0,0)
  BaseFeature = -> Pad045
  ClaimChildren = false
  Fit = 0
  FitJoin = 0
  InnerFit = 0
  InnerFitJoin = 0
  InvalidShape = false
  Linearize = true
  NewSolid = false
  Profile = -> Sketch076
  ReferenceAxis = -> Sketch076 [V_Axis]
  Refine = true
  Suppress = false
  TreeRank = 112
  ValidateShape = true
  _ProfileBasedVersion = 1
FEATURE [Sketcher::SketchObject] Sketch077
  ArcFitTolerance = 1e-06
  AttachmentSupport = -> [Groove]
  ExternalBSplineMaxDegree = 5
  ExternalBSplineTolerance = 0.0001
  FullyConstrained = true
  InternalTolerance = 1e-06
  InvalidShape = false
  MakeInternals = true
  MapMode = 5
  Placement = pos=(0,0,21) rot=(0,0,1;0rad)
  Support = -> [Groove]
  TreeRank = 113
  ValidateShape = true
  sketch-geometry (7):
    g0: Circle CenterX=-4.7166e-12 CenterY=11.3561 CenterZ=0 NormalX=0 NormalY=0 NormalZ=1 AngleXU=0 Radius=2.2
    g1: Circle CenterX=9.83464 CenterY=-5.67803 CenterZ=0 NormalX=0 NormalY=0 NormalZ=1 AngleXU=0 Radius=2.2
    g2: Circle CenterX=-9.83464 CenterY=-5.67803 CenterZ=0 NormalX=0 NormalY=0 NormalZ=1 AngleXU=0 Radius=2.2
    g3: Circle [constr] CenterX=7.482e-13 CenterY=1.30938e-11 CenterZ=0 NormalX=0 NormalY=0 NormalZ=1 AngleXU=0 Radius=11.3561
    g4: LineSegment [constr] StartX=-9.83464 StartY=-5.67803 StartZ=0 EndX=7.478e-13 EndY=1.30935e-11 EndZ=0
    g5: LineSegment [constr] StartX=7.482e-13 StartY=1.30938e-11 StartZ=0 EndX=9.83464 EndY=-5.67803 EndZ=0
    g6: LineSegment [constr] StartX=7.482e-13 StartY=1.30938e-11 StartZ=0 EndX=-4.7166e-12 EndY=11.3561 EndZ=0
  constraints (16):
    c: PointOnObject(g0,g-2)
    c: Coincident(g3,g-1)
    c: PointOnObject(g0,g3)
    c: PointOnObject(g1,g3)
    c: PointOnObject(g2,g3)
    c: Equal(g2,g1)
    c: Equal(g1,g0)
    c: Coincident(g4,g2)
    c: Coincident(g4,g3)
    c: Coincident(g5,g3)
    c: Coincident(g5,g1)
    c: Coincident(g6,g3)
    c: Coincident(g6,g0)
    c: Angle(g5,g6) = 2.0944
    c: Symmetric(g2,g1,g-2)
    c: Diameter(g1) = 4.4
FEATURE [PartDesign::Pocket] Pocket034
  AddSubType = 1
  AutoTaperInnerAngle = true
  BaseFeature = -> Groove
  CheckUpToFaceLimits = true
  ClaimChildren = false
  Fit = 0
  FitJoin = 0
  InnerFit = 0
  InnerFitJoin = 0
  InvalidShape = false
  Length = 10
  Length2 = 100
  Linearize = true
  NewSolid = false
  Profile = -> Sketch077
  Refine = true
  Suppress = false
  TaperInnerAngle = 0
  TaperInnerAngleRev = 0
  TreeRank = 114
  Type = 0
  ValidateShape = true
  _ProfileBasedVersion = 1
  _Version = 1
FEATURE [PartDesign::Fillet] Fillet023
  AddSubType = 0
  Base = -> Pocket034 [Edge3]
  BaseFeature = -> Pocket034
  InvalidShape = false
  NewSolid = false
  Radius = 14
  Refine = true
  SupportTransform = false
  Suppress = false
  TreeRank = 115
  ValidateShape = true
FEATURE [PartDesign::Chamfer] Chamfer025
  AddSubType = 0
  Angle = 45
  Base = -> Fillet023 [Edge3]
  BaseFeature = -> Fillet023
  ChamferType = 0
  FlipDirection = false
  InvalidShape = false
  NewSolid = false
  Refine = true
  Size = 2
  Size2 = 1
  SupportTransform = false
  Suppress = false
  TreeRank = 116
  ValidateShape = true
FEATURE [PartDesign::Fillet] Fillet024
  AddSubType = 0
  Base = -> Chamfer025 [Edge13,Edge11]
  BaseFeature = -> Chamfer025
  InvalidShape = false
  NewSolid = false
  Radius = 2
  Refine = true
  SupportTransform = false
  Suppress = false
  TreeRank = 117
  ValidateShape = true
FEATURE [PartDesign::Chamfer] Chamfer026
  AddSubType = 0
  Angle = 45
  Base = -> Fillet024 [Edge18,Edge3,Edge15]
  BaseFeature = -> Fillet024
  ChamferType = 0
  FlipDirection = false
  InvalidShape = false
  NewSolid = false
  Refine = true
  Size = 1
  Size2 = 1
  SupportTransform = false
  Suppress = false
  TreeRank = 118
  ValidateShape = true
FEATURE [PartDesign::SubShapeBinder] Binder005  label="Binder005(Chamfer026)"
  BindCopyOnChange = 0
  BindMode = 0
  ClaimChildren = false
  Context = -> Group002 [Part013.Body039.Binder005.]
  EdgeTolerance = 1e-06
  FillStyle = 0
  Fuse = false
  InvalidShape = false
  MakeFace = true
  MergeEdges = true
  OffsetFill = false
  OffsetIntersection = false
  OffsetJoinType = 0
  OffsetOpenResult = false
  Outline = false
  PartialLoad = false
  Relative = true
  SplitEdges = false
  Support = -> [Body038[Chamfer026.Face17]]
  TightBound = false
  TreeRank = 133
  ValidateShape = true
  _Version = 8
FEATURE [Sketcher::SketchObject] Sketch078
  ArcFitTolerance = 1e-06
  AttachmentSupport = -> [Binder005]
  ExternalBSplineMaxDegree = 5
  ExternalBSplineTolerance = 0.0001
  FullyConstrained = true
  InternalTolerance = 1e-06
  InvalidShape = false
  MakeInternals = true
  MapMode = 5
  Placement = pos=(0,0,21) rot=(0,0,1;0rad)
  Support = -> [Binder005]
  TreeRank = 134
  ValidateShape = true
  sketch-geometry (12):
    g0: Circle CenterX=2.0355e-12 CenterY=-3.998e-13 CenterZ=0 NormalX=0 NormalY=0 NormalZ=1 AngleXU=0 Radius=85
    g1: Circle CenterX=2.0355e-12 CenterY=11.355 CenterZ=0 NormalX=0 NormalY=0 NormalZ=1 AngleXU=0 Radius=1.6
    g2: Circle CenterX=9.83372 CenterY=-5.6775 CenterZ=0 NormalX=0 NormalY=0 NormalZ=1 AngleXU=0 Radius=1.6
    g3: Circle CenterX=-9.83372 CenterY=-5.6775 CenterZ=0 NormalX=0 NormalY=0 NormalZ=1 AngleXU=0 Radius=1.6
    g4: Circle [constr] CenterX=2.0355e-12 CenterY=-3.998e-13 CenterZ=0 NormalX=0 NormalY=0 NormalZ=1 AngleXU=0 Radius=11.355
    g5: LineSegment [constr] StartX=2.0355e-12 StartY=11.355 StartZ=0 EndX=2.0355e-12 EndY=-3.997e-13 EndZ=0
    g6: LineSegment [constr] StartX=2.0355e-12 StartY=-3.998e-13 StartZ=0 EndX=-9.83372 EndY=-5.6775 EndZ=0
    g7: LineSegment [constr] StartX=2.0355e-12 StartY=-3.998e-13 StartZ=0 EndX=9.83372 EndY=-5.6775 EndZ=0
    g8: Circle CenterX=-3.78e-14 CenterY=60 CenterZ=0 NormalX=0 NormalY=0 NormalZ=1 AngleXU=0 Radius=1.6
    g9: Circle [constr] CenterX=2.0355e-12 CenterY=-3.998e-13 CenterZ=0 NormalX=0 NormalY=0 NormalZ=1 AngleXU=0 Radius=60
    g10: Circle CenterX=51.9615 CenterY=-30 CenterZ=0 NormalX=0 NormalY=0 NormalZ=1 AngleXU=0 Radius=1.6
    g11: Circle CenterX=-51.9615 CenterY=-30 CenterZ=0 NormalX=0 NormalY=0 NormalZ=1 AngleXU=0 Radius=1.6
  constraints (29):
    c: Coincident(g0,g-1)
    c: Diameter(g0) = 170
    c: Equal(g3,g2)
    c: Equal(g3,g1)
    c: Diameter(g3) = 3.2
    c: Coincident(g4,g0)
    c: PointOnObject(g1,g4)
    c: Diameter(g4) = 22.71
    c: Coincident(g5,g1)
    c: Coincident(g5,g0)
    c: Vertical(g5)
    c: Coincident(g6,g0)
    c: Coincident(g6,g3)
    c: Coincident(g7,g0)
    c: Coincident(g7,g2)
    c: Angle(g7,g5) = 2.0944
    c: Symmetric(g3,g2,g-2)
    c: PointOnObject(g2,g4)
    c: PointOnObject(g8,g-2)
    c: DistanceY(g8) = 60
    c: Equal(g8,g1)
    c: Coincident(g9,g0)
    c: PointOnObject(g8,g9)
    c: PointOnObject(g10,g9)
    c: PointOnObject(g11,g9)
    c: Equal(g11,g10)
    c: Equal(g10,g8)
    c: PointOnObject(g10,g7)
    c: PointOnObject(g11,g6)
FEATURE [PartDesign::Pad] Pad046
  AddSubType = 0
  AlongSketchNormal = false
  AutoTaperInnerAngle = true
  CheckUpToFaceLimits = true
  ClaimChildren = false
  Direction = (0,0,1)
  Fit = 0
  FitJoin = 0
  InnerFit = 0
  InnerFitJoin = 0
  InvalidShape = false
  Length = 3
  Length2 = 100
  Linearize = true
  NewSolid = false
  Profile = -> Sketch078
  Refine = true
  Suppress = false
  TaperInnerAngle = 0
  TaperInnerAngleRev = 0
  TreeRank = 135
  Type = 0
  ValidateShape = true
  _ProfileBasedVersion = 1
FEATURE [Sketcher::SketchObject] Sketch079
  ArcFitTolerance = 1e-06
  AttachmentSupport = -> [Chamfer026]
  ExternalBSplineMaxDegree = 5
  ExternalBSplineTolerance = 0.0001
  FullyConstrained = false
  InternalTolerance = 1e-06
  InvalidShape = false
  MakeInternals = true
  MapMode = 5
  Placement = pos=(0,0,21) rot=(0,0,1;0rad)
  Support = -> [Chamfer026]
  TreeRank = 136
  ValidateShape = true
  sketch-geometry (4):
    g0: ArcOfCircle CenterX=1.25182e-10 CenterY=4.9383e-12 CenterZ=0 NormalX=0 NormalY=0 NormalZ=1 AngleXU=0 Radius=34.3525 StartAngle=1.11893 EndAngle=2.02267
    g1: ArcOfCircle CenterX=1.25182e-10 CenterY=4.9383e-12 CenterZ=0 NormalX=0 NormalY=0 NormalZ=1 AngleXU=0 Radius=82.5 StartAngle=1.51015 EndAngle=1.63144
    g2: LineSegment StartX=-15 StartY=30.9046 StartZ=0 EndX=-5 EndY=82.3483 EndZ=0
    g3: LineSegment StartX=5 StartY=82.3483 StartZ=0 EndX=15 EndY=30.9046 EndZ=0
  constraints (11):
    c: Coincident(g0,g-1)
    c: Coincident(g1,g0)
    c: Symmetric(g1,g1,g-2)
    c: Symmetric(g0,g0,g-2)
    c: Coincident(g2,g0)
    c: Coincident(g2,g1)
    c: Coincident(g3,g1)
    c: Coincident(g3,g0)
    c: Diameter(g1) = 165
    c: DistanceX(g1,g1) = 10
    c: DistanceX(g0,g0) = 30
FEATURE [PartDesign::Pad] Pad047
  AddSubType = 0
  AlongSketchNormal = false
  AutoTaperInnerAngle = true
  BaseFeature = -> Chamfer026
  CheckUpToFaceLimits = true
  ClaimChildren = false
  Direction = (0,0,1)
  Fit = 0
  FitJoin = 0
  InnerFit = 0
  InnerFitJoin = 0
  InvalidShape = false
  Length = 10
  Length2 = 100
  Linearize = true
  NewSolid = false
  Profile = -> Sketch079
  Refine = true
  Reversed = true
  Suppress = false
  TaperInnerAngle = 0
  TaperInnerAngleRev = 0
  TreeRank = 137
  Type = 0
  ValidateShape = true
  _ProfileBasedVersion = 1
FEATURE [PartDesign::Chamfer] Chamfer027
  AddSubType = 0
  Angle = 45
  Base = -> Pad047 [Edge37]
  BaseFeature = -> Pad047
  ChamferType = 1
  FlipDirection = false
  InvalidShape = false
  NewSolid = false
  Refine = true
  Size = 40
  Size2 = 8
  SupportTransform = false
  Suppress = false
  TreeRank = 138
  ValidateShape = true
FEATURE [PartDesign::Fillet] Fillet025
  AddSubType = 0
  Base = -> Chamfer027 [Edge3,Edge14]
  BaseFeature = -> Chamfer027
  InvalidShape = false
  NewSolid = false
  Radius = 10
  Refine = true
  SupportTransform = false
  Suppress = false
  TreeRank = 139
  ValidateShape = true
FEATURE [PartDesign::Fillet] Fillet026
  AddSubType = 0
  Base = -> Fillet025 [Edge25,Edge5]
  BaseFeature = -> Fillet025
  InvalidShape = false
  NewSolid = false
  Radius = 3
  Refine = true
  SupportTransform = false
  Suppress = false
  TreeRank = 140
  ValidateShape = true
FEATURE [PartDesign::Fillet] Fillet027
  AddSubType = 0
  Base = -> Fillet026 [Edge7]
  BaseFeature = -> Fillet026
  InvalidShape = false
  NewSolid = false
  Radius = 40
  Refine = true
  SupportTransform = false
  Suppress = false
  TreeRank = 141
  ValidateShape = true
FEATURE [PartDesign::PolarPattern] PolarPattern
  AddSubType = 0
  Angle = 360
  Axis = -> Sketch079 [N_Axis]
  BaseFeature = -> Fillet027
  CopyShape = false
  InvalidShape = false
  NewSolid = false
  Occurrences = 3
  OriginalSubs = -> [Pad047,Chamfer027,Fillet025,Fillet026,Fillet027]
  Originals = -> [Pad047,Chamfer027,Fillet025,Fillet026,Fillet027]
  ParallelTransform = true
  Refine = true
  SubTransform = true
  Suppress = false
  TreeRank = 142
  ValidateShape = true
  _Version = 3
FEATURE [Sketcher::SketchObject] Sketch080
  ArcFitTolerance = 1e-06
  AttachmentSupport = -> [PolarPattern]
  ExternalBSplineMaxDegree = 5
  ExternalBSplineTolerance = 0.0001
  FullyConstrained = true
  InternalTolerance = 1e-06
  InvalidShape = false
  MakeInternals = true
  MapMode = 5
  Placement = pos=(0,0,21) rot=(0,0,1;0rad)
  Support = -> [PolarPattern]
  TreeRank = 143
  ValidateShape = true
  sketch-geometry (1):
    g0: Circle CenterX=0 CenterY=60 CenterZ=0 NormalX=0 NormalY=0 NormalZ=1 AngleXU=0 Radius=2.2
  constraints (3):
    c: PointOnObject(g0,g-2)
    c: Diameter(g0) = 4.4
    c: DistanceY(g-1,g0) = 60
FEATURE [PartDesign::Pocket] Pocket035
  AddSubType = 1
  AutoTaperInnerAngle = true
  BaseFeature = -> PolarPattern
  CheckUpToFaceLimits = true
  ClaimChildren = false
  Fit = 0
  FitJoin = 0
  InnerFit = 0
  InnerFitJoin = 0
  InvalidShape = false
  Length = 5
  Length2 = 100
  Linearize = true
  NewSolid = false
  Profile = -> Sketch080
  Refine = true
  Suppress = false
  TaperInnerAngle = 0
  TaperInnerAngleRev = 0
  TreeRank = 144
  Type = 1
  ValidateShape = true
  _ProfileBasedVersion = 1
  _Version = 1
FEATURE [PartDesign::PolarPattern] PolarPattern016
  AddSubType = 0
  Angle = 360
  Axis = -> Sketch080 [N_Axis]
  BaseFeature = -> Pocket035
  CopyShape = false
  InvalidShape = false
  NewSolid = false
  Occurrences = 3
  OriginalSubs = -> [Pocket035]
  Originals = -> [Pocket035]
  ParallelTransform = true
  Refine = true
  SubTransform = true
  Suppress = false
  TreeRank = 145
  ValidateShape = true
  _Version = 3
FEATURE [PartDesign::Chamfer] Chamfer028
  AddSubType = 0
  Angle = 45
  Base = -> PolarPattern016 [Edge11,Edge114,Edge108]
  BaseFeature = -> PolarPattern016
  ChamferType = 0
  FlipDirection = false
  InvalidShape = false
  NewSolid = false
  Refine = true
  Size = 1
  Size2 = 1
  SupportTransform = false
  Suppress = false
  TreeRank = 146
  ValidateShape = true
FEATURE [PartDesign::Chamfer] Chamfer029
  AddSubType = 0
  Angle = 45
  Base = -> Chamfer028 [Face11]
  BaseFeature = -> Chamfer028
  ChamferType = 0
  FlipDirection = false
  InvalidShape = false
  NewSolid = false
  Refine = true
  Size = 0.4
  Size2 = 1
  SupportTransform = false
  Suppress = false
  TreeRank = 147
  ValidateShape = true
FEATURE [PartDesign::Body] Body038  label="PlugRobot"
  AutoGroupSolids = false
  ClaimAllChildren = false
  ExportMode = 0
  Group = -> [Sketch074,Pad043,Pad044,Sketch075,Pad045,Import002,Sketch076,Groove,Sketch077,Pocket034,Fillet023,Chamfer025,Fillet024,Chamfer026,Sketch079,Pad047,Chamfer027,Fillet025,Fillet026,Fillet027,PolarPattern,Sketch080,Pocket035,PolarPattern016,Chamfer028,Chamfer029]
  InvalidShape = false
  Origin = -> Origin059
  SingleSolid = true
  Tip = -> Chamfer029
  TreeRank = 104
  ValidateShape = true
  _ExportChildren = -> [Pad043,Pad044,Pad045,Import002,Groove,Pocket034,Fillet023,Chamfer025,Fillet024,Chamfer026,Pad047,Chamfer027,Fillet025,Fillet026,Fillet027,PolarPattern,Pocket035,PolarPattern016,Chamfer028,Chamfer029]
  _GroupVersion = 1
FEATURE [Sketcher::SketchObject] Sketch081
  ArcFitTolerance = 1e-06
  AttachmentSupport = -> [Pad046]
  ExternalBSplineMaxDegree = 5
  ExternalBSplineTolerance = 0.0001
  FullyConstrained = true
  InternalTolerance = 1e-06
  InvalidShape = false
  MakeInternals = true
  MapMode = 5
  Placement = pos=(0,0,24) rot=(0,0,1;0rad)
  Support = -> [Pad046]
  TreeRank = 148
  ValidateShape = true
  sketch-geometry (6):
    g0: LineSegment StartX=-40 StartY=-75 StartZ=0 EndX=-34.2265 EndY=-65 EndZ=0
    g1: ArcOfCircle CenterX=3.0925e-12 CenterY=-211.043 CenterZ=0 NormalX=0 NormalY=0 NormalZ=1 AngleXU=0 Radius=150 StartAngle=1.34059 EndAngle=1.801
    g2: ArcOfCircle CenterX=3.8288e-12 CenterY=2.3123e-12 CenterZ=0 NormalX=0 NormalY=0 NormalZ=1 AngleXU=0 Radius=85 StartAngle=4.22243 EndAngle=5.20235
    g3: LineSegment StartX=34.2265 StartY=-65 StartZ=0 EndX=40 EndY=-75 EndZ=0
    g4: LineSegment [constr] StartX=-40 StartY=-75 StartZ=0 EndX=-8.3276e-12 EndY=-5.71797 EndZ=0
    g5: LineSegment [constr] StartX=-8.3245e-12 StartY=-5.71797 StartZ=0 EndX=40 EndY=-75 EndZ=0
  constraints (18):
    c: PointOnObject(g1,g-2)
    c: Coincident(g1,g0)
    c: Coincident(g2,g-1)
    c: Coincident(g2,g0)
    c: Coincident(g3,g1)
    c: Coincident(g3,g2)
    c: Equal(g3,g0)
    c: Angle(g0,g3) = 1.0472
    c: Diameter(g1) = 300
    c: DistanceY(g0) = -65
    c: Diameter(g2) = 170
    c: Coincident(g4,g0)
    c: PointOnObject(g4,g-2)
    c: Coincident(g5,g4)
    c: Coincident(g5,g2)
    c: PointOnObject(g1,g5)
    c: PointOnObject(g0,g4)
    c: DistanceX(g0,g2) = 80
FEATURE [PartDesign::Pocket] Pocket036
  AddSubType = 1
  AutoTaperInnerAngle = true
  BaseFeature = -> Pad046
  CheckUpToFaceLimits = true
  ClaimChildren = false
  Fit = 0
  FitJoin = 0
  InnerFit = 0
  InnerFitJoin = 0
  InvalidShape = false
  Length = 5
  Length2 = 100
  Linearize = true
  NewSolid = false
  Profile = -> Sketch081
  Refine = true
  Suppress = false
  TaperInnerAngle = 0
  TaperInnerAngleRev = 0
  TreeRank = 149
  Type = 1
  ValidateShape = true
  _ProfileBasedVersion = 1
  _Version = 1
FEATURE [PartDesign::Fillet] Fillet028
  AddSubType = 0
  Base = -> Pocket036 [Edge25,Edge14,Edge26,Edge13]
  BaseFeature = -> Pocket036
  InvalidShape = false
  NewSolid = false
  Radius = 7
  Refine = true
  SupportTransform = false
  Suppress = false
  TreeRank = 150
  ValidateShape = true
FEATURE [PartDesign::PolarPattern] PolarPattern017
  AddSubType = 0
  Angle = 360
  Axis = -> Sketch081 [N_Axis]
  BaseFeature = -> Fillet028
  CopyShape = false
  InvalidShape = false
  NewSolid = false
  Occurrences = 3
  OriginalSubs = -> [Pocket036,Fillet028]
  Originals = -> [Pocket036,Fillet028]
  ParallelTransform = true
  Refine = true
  SubTransform = true
  Suppress = false
  TreeRank = 151
  ValidateShape = true
  _Version = 3
FEATURE [PartDesign::Body] Body039  label="Plate"
  AutoGroupSolids = false
  ClaimAllChildren = false
  ExportMode = 0
  Group = -> [Binder005,Sketch078,Pad046,Sketch081,Pocket036,Fillet028,PolarPattern017]
  InvalidShape = false
  Origin = -> Origin061
  SingleSolid = true
  Tip = -> PolarPattern017
  TreeRank = 132
  ValidateShape = true
  _ExportChildren = -> [Binder005,Pad046,Pocket036,Fillet028,PolarPattern017]
  _GroupVersion = 1
FEATURE [App::Part] Part013  label="RobotStand"
  ClaimAllChildren = false
  ExportMode = 1
  Group = -> [Body038,Body039]
  Origin = -> Origin060
  Placement = pos=(0,1e-15,8) rot=(1,0,0;3.14159rad)
  TreeRank = 122
  _ExportChildren = -> [Body038,Body039]
  _GroupVersion = 1
FEATURE [App::DocumentObjectGroup] Group002  label="Parts"
  ClaimAllChildren = true
  ExportMode = 1
  Group = -> [Part,Part007,Body024,Part004,Part005,Part008,Part009,Part006,Part010,Body029,Part011,Part012,Part013]
  TreeRank = 0
  _GroupVersion = 1
FEATURE [TechDraw::DrawSVGTemplate] Template008
  Height = 210
  Orientation = 1
  TreeRank = 153
  Width = 297
FEATURE [TechDraw::DrawProjGroupItem] ProjItem012  label="Front013"
  CoarseView = false
  Direction = (0,0,-1)
  Focus = 100
  HardHidden = false
  IsoCount = 0
  IsoHidden = false
  IsoVisible = false
  LockPosition = true
  Perspective = false
  Rotation = 0
  RotationVector = (1,0,0)
  ScaleType = 2
  SeamHidden = false
  SeamVisible = true
  SmoothHidden = false
  SmoothVisible = true
  Source = -> [PolarPattern017]
  TreeRank = 156
  Type = 0
  X = 0
  XDirection = (1,0,0)
  Y = 0
FEATURE [TechDraw::DrawProjGroup] ProjGroup012
  Anchor = -> ProjItem012
  AutoDistribute = true
  LockPosition = false
  ProjectionType = 0
  Rotation = 0
  ScaleType = 0
  Source = -> [PolarPattern017]
  TreeRank = 157
  Views = -> [ProjItem012]
  X = 87.444
  Y = 129.768
  spacingX = 15
  spacingY = 15
FEATURE [TechDraw::DrawPage] Page008  label="Maser3mmPlateStandRobot"
  KeepUpdated = true
  NextBalloonIndex = 1
  ProjectionType = 0
  Template = -> Template008
  TreeRank = 154
  Views = -> [ProjGroup012]
FEATURE [App::DocumentObjectGroup] Group  label="Laser"
  ClaimAllChildren = true
  ExportMode = 1
  Group = -> [Page,Page001,Page002,Page003,Page004,Page005,Page007,Page008]
  TreeRank = 0
  _GroupVersion = 1

RESOLVED EXTERNAL PARTS (link-assembly join: the EXTERNAL_REF files above that resolve inside this repo's crawl, each included once):
---- part generic-hardware.FCStd = doc fcstd_4d7483fc6a56 (179892 chars; too large to inline — full recipe in that document) ----
